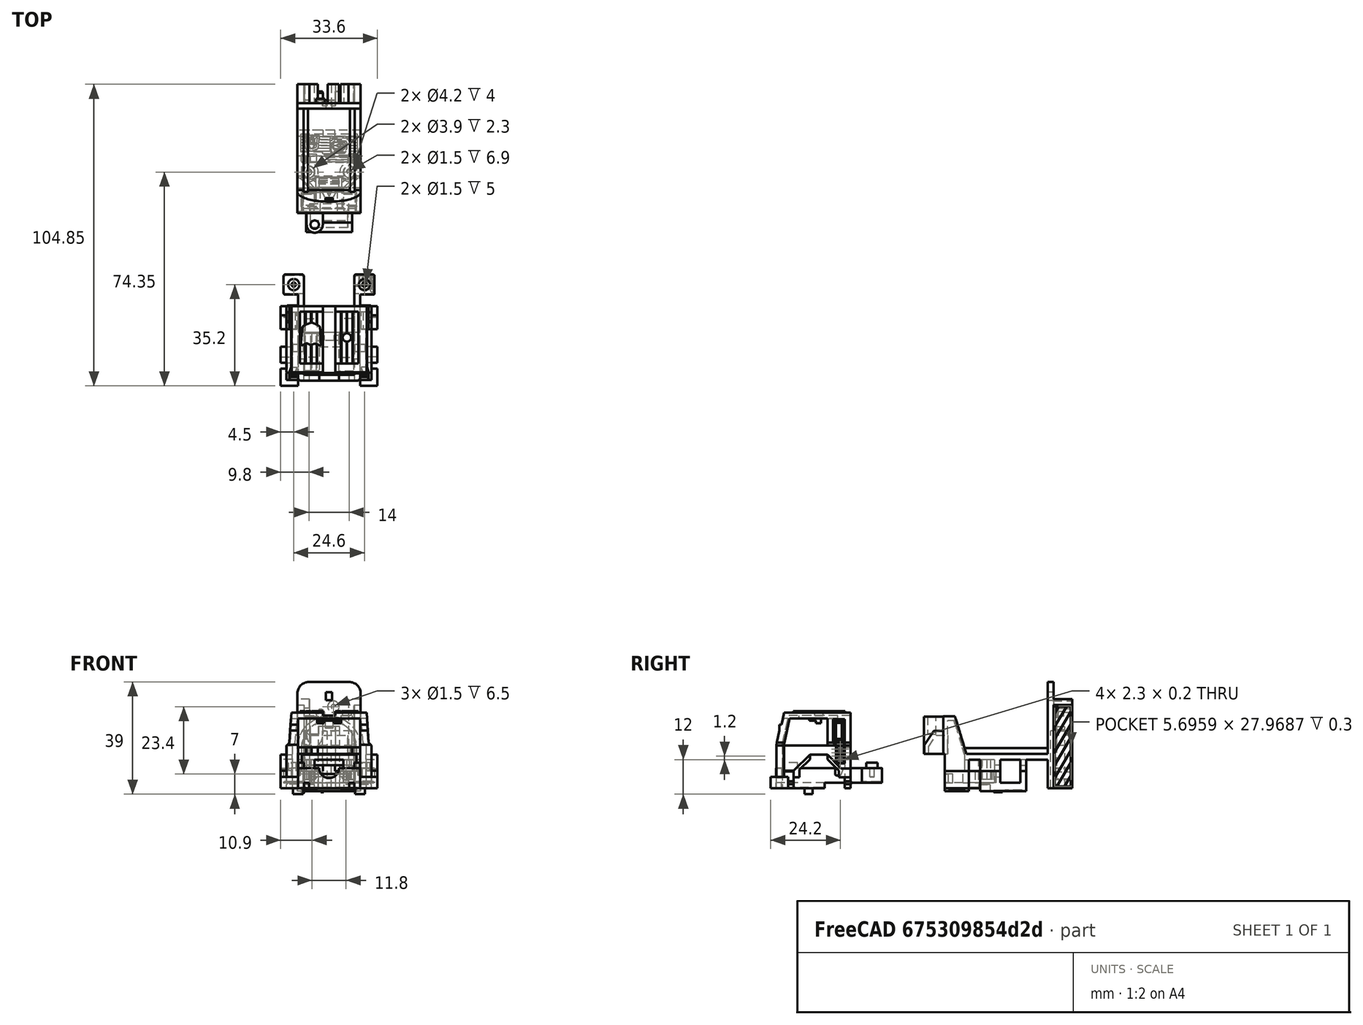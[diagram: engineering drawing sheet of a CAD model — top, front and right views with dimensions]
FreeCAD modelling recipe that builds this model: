
FCSTD DOCUMENT  (FreeCAD 1.0R39319 (Git))
Label: Stickered_Parts
License: All rights reserved
LicenseURL: https://en.wikipedia.org/wiki/All_rights_reserved
objects: Sketcher::SketchObject×30, PartDesign::Pocket×22, PartDesign::Body×12, Image::ImagePlane×8, PartDesign::SubShapeBinder×8, PartDesign::Pad×8, Part::Feature×4, PartDesign::FeatureBase×4, Mesh::Feature×1, App::Part×1
note: 182 computed .brp shape members not serialized (recipe doc carries the construction recipe); baked Part::Feature solids carry a one-line shape summary decoded from their .brp

FEATURE [Part::Feature] Part__Feature  label="Cab"
  shape: bbox 33.6 x 27.95 x 26.8 mm, 325 faces (baked)
FEATURE [Image::ImagePlane] Sticker1
  Placement = pos=(3.1,-61,11) rot=(0,0,1;3.14159rad)
  XSize = 17.2965
  YSize = 14.868
FEATURE [PartDesign::FeatureBase] BaseFeature
  BaseFeature = -> Part__Feature
  Suppressed = false
FEATURE [Sketcher::SketchObject] Sketch
  ArcFitTolerance = 1e-06
  AttachmentOffset = pos=(9.6,-133,0) rot=(0,0,1;3.14159rad)
  AttachmentSupport = -> [BaseFeature]
  FullyConstrained = false
  MakeInternals = false
  MapMode = 5
  Placement = pos=(9.6,-133,15.8) rot=(0,0,1;3.14159rad)
  sketch-geometry (55):
    g0-g23: Circle [constr] x24 (B-spline internal-alignment scaffolding for g24; pole/knot coordinates omitted)
    g24: BSplineCurve PolesCount=28 KnotsCount=26 Degree=3 IsPeriodic=0
    g25-g48: GeomPoint [constr] x24 (B-spline internal-alignment scaffolding for g24; pole/knot coordinates omitted)
    g49: Circle [constr] CenterX=7.95561 CenterY=-71.4183 CenterZ=0 NormalX=0 NormalY=0 NormalZ=1 AngleXU=0 Radius=1
    g50: GeomPoint [constr] X=8.29878 Y=-66.6782 Z=0
    g51: Circle [constr] CenterX=8.16417 CenterY=-68.0435 CenterZ=0 NormalX=0 NormalY=0 NormalZ=1 AngleXU=0 Radius=1
    g52: Circle [constr] CenterX=8.36822 CenterY=-65.9535 CenterZ=0 NormalX=0 NormalY=0 NormalZ=1 AngleXU=0 Radius=1
    g53: Circle [constr] CenterX=8.41747 CenterY=-65.4884 CenterZ=0 NormalX=0 NormalY=0 NormalZ=1 AngleXU=0 Radius=1
    g54: GeomPoint [constr] X=8.36699 Y=-65.9691 Z=0
  constraints (15):
    c: Weight(g0) = 1
    c: Equal(g0, g1-g23) x23
    c: InternalAlignment(g0-g23 -> g24) x24
    c: InternalAlignment(g25-g48 -> g24) x24
    c: Coincident(g23,g0)
    c: InternalAlignment(g49,g24)
    c: Equal(g49,g0)
    c: InternalAlignment(g50,g24)
    c: InternalAlignment(g51,g24)
    c: Equal(g51,g0)
    c: InternalAlignment(g52,g24)
    c: Equal(g52,g0)
    c: InternalAlignment(g53,g24)
    c: Equal(g53,g0)
    c: InternalAlignment(g54,g24)
FEATURE [PartDesign::Pocket] Pocket
  BaseFeature = -> BaseFeature
  Direction = (5.8e-15,0,-1)
  Length = 0.3
  Length2 = 5
  Profile = -> Sketch
  ReferenceAxis = -> Sketch [N_Axis]
  Refine = true
  Suppressed = false
  Type = 0
FEATURE [PartDesign::Body] Body  label="Cab_Stickered1"
  AllowCompound = false
  BaseFeature = -> Part__Feature
  Group = -> [BaseFeature,Sketch,Pocket]
  Origin = -> Origin
  Tip = -> Pocket
FEATURE [Part::Feature] Part__Feature001  label="Rear_Torso"
  shape: bbox 22 x 51.6 x 37 mm, 145 faces (baked)
FEATURE [Image::ImagePlane] Sticker002
  Placement = pos=(19,17.35,3.5) rot=(0,1,0;1.5708rad)
  XSize = 29.34
  YSize = 11.4
FEATURE [PartDesign::FeatureBase] BaseFeature001
  BaseFeature = -> Part__Feature001
  Suppressed = false
FEATURE [Sketcher::SketchObject] Sketch001
  ArcFitTolerance = 1e-06
  AttachmentSupport = -> [BaseFeature001]
  FullyConstrained = false
  MakeInternals = false
  MapMode = 5
  Placement = pos=(19.8,-2.42e-14,8.7e-15) rot=(0.57735,0.57735,0.57735;2.0944rad)
  sketch-geometry (4):
    g0: LineSegment StartX=16.8703 StartY=17.597 StartZ=0 EndX=16.8703 EndY=-10.3717 EndZ=0
    g1: LineSegment StartX=16.8703 StartY=-10.3717 StartZ=0 EndX=22.5662 EndY=-10.3717 EndZ=0
    g2: LineSegment StartX=22.5662 StartY=-10.3717 StartZ=0 EndX=22.5662 EndY=17.597 EndZ=0
    g3: LineSegment StartX=22.5662 StartY=17.597 StartZ=0 EndX=16.8703 EndY=17.597 EndZ=0
  constraints (8):
    c: Coincident(g0,g1)
    c: Coincident(g1,g2)
    c: Coincident(g2,g3)
    c: Coincident(g3,g0)
    c: Vertical(g0)
    c: Vertical(g2)
    c: Horizontal(g1)
    c: Horizontal(g3)
FEATURE [PartDesign::Pocket] Pocket001
  BaseFeature = -> BaseFeature001
  Direction = (-1,1e-15,1e-16)
  Length = 0.3
  Length2 = 5
  Profile = -> Sketch001
  ReferenceAxis = -> Sketch001 [N_Axis]
  Refine = true
  Suppressed = false
  Type = 0
FEATURE [Sketcher::SketchObject] Sketch002
  ArcFitTolerance = 1e-06
  AttachmentSupport = -> [Pocket001]
  FullyConstrained = false
  MakeInternals = false
  MapMode = 5
  Placement = pos=(2.2,-2.1e-15,1.8e-15) rot=(0.57735,-0.57735,-0.57735;2.0944rad)
  sketch-geometry (4):
    g0: LineSegment StartX=-22.5917 StartY=8.98465 StartZ=0 EndX=-22.5917 EndY=-10.3482 EndZ=0
    g1: LineSegment StartX=-22.5917 StartY=-10.3482 StartZ=0 EndX=-16.9211 EndY=-10.3482 EndZ=0
    g2: LineSegment StartX=-16.9211 StartY=-10.3482 StartZ=0 EndX=-16.9211 EndY=8.98465 EndZ=0
    g3: LineSegment StartX=-16.9211 StartY=8.98465 StartZ=0 EndX=-22.5917 EndY=8.98465 EndZ=0
  constraints (8):
    c: Coincident(g0,g1)
    c: Coincident(g1,g2)
    c: Coincident(g2,g3)
    c: Coincident(g3,g0)
    c: Vertical(g0)
    c: Vertical(g2)
    c: Horizontal(g1)
    c: Horizontal(g3)
FEATURE [PartDesign::Pocket] Pocket002
  BaseFeature = -> Pocket001
  Direction = (1,0,0)
  Length = 0.3
  Length2 = 5
  Profile = -> Sketch002
  ReferenceAxis = -> Sketch002 [N_Axis]
  Refine = true
  Suppressed = false
  Type = 0
FEATURE [PartDesign::Body] Body001  label="Rear_Torso_Stickered"
  AllowCompound = false
  BaseFeature = -> Part__Feature001
  Group = -> [BaseFeature001,Sketch001,Pocket001,Sketch002,Pocket002]
  Origin = -> Origin001
  Tip = -> Pocket002
FEATURE [Mesh::Feature] Cab_Sticker  label="Mixmaster_Sticker1"
FEATURE [App::Part] Part  label="Cab_Stickered"
  Group = -> [Sticker1,Part__Feature,Body]
  Origin = -> Origin002
FEATURE [PartDesign::SubShapeBinder] Binder
  BindCopyOnChange = 0
  BindMode = 0
  ClaimChildren = false
  Context = -> Body002 [Binder.]
  Fuse = false
  MakeFace = true
  OffsetFill = false
  OffsetIntersection = false
  OffsetJoinType = 0
  OffsetOpenResult = false
  PartialLoad = false
  Refine = true
  Relative = true
  Support = -> [Body001[Pocket002.Face153]]
  _Version = 2
FEATURE [Sketcher::SketchObject] Sketch003
  ArcFitTolerance = 1e-06
  AttachmentSupport = -> [Binder]
  ExternalGeometry = -> [Binder]
  FullyConstrained = true
  MakeInternals = false
  MapMode = 5
  Placement = pos=(19.5,-1.21e-14,0) rot=(0.57735,0.57735,0.57735;2.0944rad)
  sketch-geometry (4):
    g0: LineSegment StartX=16.9203 StartY=17.547 StartZ=0 EndX=16.9203 EndY=-10.3217 EndZ=0
    g1: LineSegment StartX=16.9203 StartY=-10.3217 StartZ=0 EndX=22.5162 EndY=-10.3217 EndZ=0
    g2: LineSegment StartX=22.5162 StartY=-10.3217 StartZ=0 EndX=22.5162 EndY=17.547 EndZ=0
    g3: LineSegment StartX=22.5162 StartY=17.547 StartZ=0 EndX=16.9203 EndY=17.547 EndZ=0
  constraints (12):
    c: Coincident(g0,g1)
    c: Coincident(g1,g2)
    c: Coincident(g2,g3)
    c: Coincident(g3,g0)
    c: Vertical(g0)
    c: Vertical(g2)
    c: Horizontal(g1)
    c: Horizontal(g3)
    c: DistanceX(g1,g-6) = 0.05
    c: DistanceX(g-6,g0) = 0.05
    c: DistanceY(g-6,g0) = 0.05
    c: DistanceY(g0,g-5) = 0.05
FEATURE [PartDesign::Pad] Pad
  Direction = (1,0,0)
  Length = 0.3
  Length2 = 10
  Profile = -> Sketch003
  ReferenceAxis = -> Sketch003 [N_Axis]
  Refine = true
  Suppressed = false
  Type = 0
FEATURE [Sketcher::SketchObject] Sketch004
  ArcFitTolerance = 1e-06
  AttachmentSupport = -> [Pad]
  ExternalGeometry = -> [Pad]
  FullyConstrained = false
  MakeInternals = false
  MapMode = 5
  Placement = pos=(19.8,0,0) rot=(0.57735,0.57735,0.57735;2.0944rad)
  sketch-geometry (48):
    g0: ArcOfCircle CenterX=18.3173 CenterY=17.547 CenterZ=0 NormalX=0 NormalY=0 NormalZ=-1 AngleXU=-1.04214 Radius=0.0145147 StartAngle=1.5708 EndAngle=4.71239
    g1: LineSegment StartX=18.3299 StartY=17.5397 StartZ=0 EndX=17.8642 EndY=16.7425 EndZ=0
    g2: LineSegment StartX=17.8642 StartY=16.7425 StartZ=0 EndX=16.9329 EndY=15.148 EndZ=0
    g3: ArcOfCircle CenterX=16.9203 CenterY=15.1554 CenterZ=0 NormalX=0 NormalY=0 NormalZ=-1 AngleXU=2.09946 Radius=0.0145147 StartAngle=1.5708 EndAngle=4.71239
    g4: LineSegment StartX=17.8391 StartY=16.7571 StartZ=0 EndX=16.9078 EndY=15.1627 EndZ=0
    g5: LineSegment StartX=18.3048 StartY=17.5543 StartZ=0 EndX=17.8391 EndY=16.7571 EndZ=0
    g6: ArcOfCircle CenterX=16.9203 CenterY=10.4908 CenterZ=0 NormalX=0 NormalY=0 NormalZ=-1 AngleXU=2.09946 Radius=0.0109509 StartAngle=1.5708 EndAngle=4.71239
    g7: LineSegment StartX=16.9109 StartY=10.4963 StartZ=0 EndX=18.2848 EndY=12.8484 EndZ=0
    g8: LineSegment StartX=18.2848 StartY=12.8484 StartZ=0 EndX=21.0325 EndY=17.5525 EndZ=0
    g9: ArcOfCircle CenterX=21.042 CenterY=17.547 CenterZ=0 NormalX=0 NormalY=0 NormalZ=-1 AngleXU=-1.04214 Radius=0.0109509 StartAngle=1.5708 EndAngle=4.71239
    g10: LineSegment StartX=18.3037 StartY=12.8374 StartZ=0 EndX=21.0515 EndY=17.5415 EndZ=0
    g11: LineSegment StartX=16.9298 StartY=10.4853 StartZ=0 EndX=18.3037 EndY=12.8374 EndZ=0
    g12: ArcOfCircle CenterX=22.5162 CenterY=15.7222 CenterZ=0 NormalX=0 NormalY=0 NormalZ=-1 AngleXU=-1.04214 Radius=0.0134354 StartAngle=1.5708 EndAngle=4.71239
    g13: LineSegment StartX=22.5278 StartY=15.7154 StartZ=0 EndX=20.6625 EndY=12.5221 EndZ=0
    g14: LineSegment StartX=20.6625 StartY=12.5221 StartZ=0 EndX=16.9319 EndY=6.13545 EndZ=0
    g15: ArcOfCircle CenterX=16.9203 CenterY=6.14222 CenterZ=0 NormalX=0 NormalY=0 NormalZ=-1 AngleXU=2.09946 Radius=0.0134354 StartAngle=1.5708 EndAngle=4.71239
    g16: LineSegment StartX=20.6393 StartY=12.5357 StartZ=0 EndX=16.9087 EndY=6.149 EndZ=0
    g17: LineSegment StartX=22.5046 StartY=15.729 StartZ=0 EndX=20.6393 EndY=12.5357 EndZ=0
    g18: ArcOfCircle CenterX=16.9203 CenterY=1.66014 CenterZ=0 NormalX=0 NormalY=0 NormalZ=-1 AngleXU=2.09946 Radius=0.0160115 StartAngle=1.5708 EndAngle=4.71239
    g19: LineSegment StartX=16.9065 StartY=1.66822 StartZ=0 EndX=18.7718 EndY=4.86155 EndZ=0
    g20: LineSegment StartX=18.7718 StartY=4.86155 StartZ=0 EndX=22.5024 EndY=11.2482 EndZ=0
    g21: ArcOfCircle CenterX=22.5162 CenterY=11.2401 CenterZ=0 NormalX=0 NormalY=0 NormalZ=-1 AngleXU=-1.04214 Radius=0.0160115 StartAngle=1.5708 EndAngle=4.71239
    g22: LineSegment StartX=18.7994 StartY=4.8454 StartZ=0 EndX=22.53 EndY=11.2321 EndZ=0
    g23: LineSegment StartX=16.9342 StartY=1.65207 StartZ=0 EndX=18.7994 EndY=4.8454 EndZ=0
    g24: ArcOfCircle CenterX=22.5162 CenterY=6.66465 CenterZ=0 NormalX=0 NormalY=0 NormalZ=-1 AngleXU=-1.04214 Radius=0.0135921 StartAngle=1.5708 EndAngle=4.71239
    g25: LineSegment StartX=22.5279 StartY=6.6578 StartZ=0 EndX=20.6626 EndY=3.46446 EndZ=0
    g26: LineSegment StartX=20.6626 StartY=3.46446 StartZ=0 EndX=16.9321 EndY=-2.9222 EndZ=0
    g27: ArcOfCircle CenterX=16.9203 CenterY=-2.91535 CenterZ=0 NormalX=0 NormalY=0 NormalZ=-1 AngleXU=2.09946 Radius=0.0135921 StartAngle=1.5708 EndAngle=4.71239
    g28: LineSegment StartX=20.6392 StartY=3.47818 StartZ=0 EndX=16.9086 EndY=-2.90849 EndZ=0
    g29: LineSegment StartX=22.5045 StartY=6.67151 StartZ=0 EndX=20.6392 EndY=3.47818 EndZ=0
    g30: ArcOfCircle CenterX=16.9203 CenterY=-7.40363 CenterZ=0 NormalX=0 NormalY=0 NormalZ=-1 AngleXU=2.09946 Radius=0.0209294 StartAngle=1.5708 EndAngle=4.71239
    g31: LineSegment StartX=16.9023 StartY=-7.39308 StartZ=0 EndX=18.7675 EndY=-4.19974 EndZ=0
    g32: LineSegment StartX=18.7675 StartY=-4.19974 StartZ=0 EndX=22.4981 EndY=2.18692 EndZ=0
    g33: ArcOfCircle CenterX=22.5162 CenterY=2.17637 CenterZ=0 NormalX=0 NormalY=0 NormalZ=-1 AngleXU=-1.04214 Radius=0.0209294 StartAngle=1.5708 EndAngle=4.71239
    g34: LineSegment StartX=18.8037 StartY=-4.22086 StartZ=0 EndX=22.5343 EndY=2.16581 EndZ=0
    g35: LineSegment StartX=16.9384 StartY=-7.41419 StartZ=0 EndX=18.8037 EndY=-4.22086 EndZ=0
    g36: ArcOfCircle CenterX=17.658 CenterY=-10.3217 CenterZ=0 NormalX=0 NormalY=0 NormalZ=-1 AngleXU=2.09946 Radius=0.0171942 StartAngle=1.5708 EndAngle=4.71239
    g37: LineSegment StartX=17.6431 StartY=-10.313 StartZ=0 EndX=19.2625 EndY=-7.54064 EndZ=0
    g38: LineSegment StartX=19.2625 StartY=-7.54064 StartZ=0 EndX=22.5013 EndY=-1.99585 EndZ=0
    g39: ArcOfCircle CenterX=22.5162 CenterY=-2.00452 CenterZ=0 NormalX=0 NormalY=0 NormalZ=-1 AngleXU=-1.04214 Radius=0.0171942 StartAngle=1.5708 EndAngle=4.71239
    g40: LineSegment StartX=19.2922 StartY=-7.55799 StartZ=0 EndX=22.531 EndY=-2.0132 EndZ=0
    g41: LineSegment StartX=17.6728 StartY=-10.3304 StartZ=0 EndX=19.2922 EndY=-7.55799 EndZ=0
    g42: ArcOfCircle CenterX=22.5162 CenterY=-6.55989 CenterZ=0 NormalX=0 NormalY=0 NormalZ=-1 AngleXU=-1.04214 Radius=0.013888 StartAngle=1.5708 EndAngle=4.71239
    g43: LineSegment StartX=22.5282 StartY=-6.56689 StartZ=0 EndX=21.7957 EndY=-7.82084 EndZ=0
    g44: LineSegment StartX=21.7957 StartY=-7.82084 StartZ=0 EndX=20.3308 EndY=-10.3287 EndZ=0
    g45: ArcOfCircle CenterX=20.3188 CenterY=-10.3217 CenterZ=0 NormalX=0 NormalY=0 NormalZ=-1 AngleXU=2.09946 Radius=0.013888 StartAngle=1.5708 EndAngle=4.71239
    g46: LineSegment StartX=21.7717 StartY=-7.80683 StartZ=0 EndX=20.3068 EndY=-10.3147 EndZ=0
    g47: LineSegment StartX=22.5042 StartY=-6.55289 StartZ=0 EndX=21.7717 EndY=-7.80683 EndZ=0
  constraints (48):
    c: Tangent(g0,g1) = 1.5708
    c: Tangent(g0,g5) = -1.5708
    c: Coincident(g1,g2)
    c: Tangent(g2,g3) = 1.5708
    c: Tangent(g3,g4) = -1.5708
    c: Coincident(g4,g5)
    c: Tangent(g6,g7) = 1.5708
    c: Tangent(g6,g11) = -1.5708
    c: Coincident(g7,g8)
    c: Tangent(g8,g9) = 1.5708
    c: Tangent(g9,g10) = -1.5708
    c: Coincident(g10,g11)
    c: Tangent(g12,g13) = 1.5708
    c: Tangent(g12,g17) = -1.5708
    c: Coincident(g13,g14)
    c: Tangent(g14,g15) = 1.5708
    c: Tangent(g15,g16) = -1.5708
    c: Coincident(g16,g17)
    c: Tangent(g18,g19) = 1.5708
    c: Tangent(g18,g23) = -1.5708
    c: Coincident(g19,g20)
    c: Tangent(g20,g21) = 1.5708
    c: Tangent(g21,g22) = -1.5708
    c: Coincident(g22,g23)
    c: Tangent(g24,g25) = 1.5708
    c: Tangent(g24,g29) = -1.5708
    c: Coincident(g25,g26)
    c: Tangent(g26,g27) = 1.5708
    c: Tangent(g27,g28) = -1.5708
    c: Coincident(g28,g29)
    c: Tangent(g30,g31) = 1.5708
    c: Tangent(g30,g35) = -1.5708
    c: Coincident(g31,g32)
    c: Tangent(g32,g33) = 1.5708
    c: Tangent(g33,g34) = -1.5708
    c: Coincident(g34,g35)
    c: Tangent(g36,g37) = 1.5708
    c: Tangent(g36,g41) = -1.5708
    c: Coincident(g37,g38)
    c: Tangent(g38,g39) = 1.5708
    c: Tangent(g39,g40) = -1.5708
    c: Coincident(g40,g41)
    c: Tangent(g42,g43) = 1.5708
    c: Tangent(g42,g47) = -1.5708
    c: Coincident(g43,g44)
    c: Tangent(g44,g45) = 1.5708
    c: Tangent(g45,g46) = -1.5708
    c: Coincident(g46,g47)
FEATURE [PartDesign::Pocket] Pocket003
  BaseFeature = -> Pad
  Direction = (-1,0,0)
  Length = 0.15
  Length2 = 5
  Profile = -> Sketch004
  ReferenceAxis = -> Sketch004 [N_Axis]
  Refine = true
  Suppressed = false
  Type = 0
FEATURE [PartDesign::Body] Body002  label="Mikmaster_Sticker2"
  AllowCompound = false
  Group = -> [Binder,Sketch003,Pad,Sketch004,Pocket003]
  Origin = -> Origin003
  Tip = -> Pocket003
FEATURE [PartDesign::SubShapeBinder] Binder001
  BindCopyOnChange = 0
  BindMode = 0
  ClaimChildren = false
  Context = -> Body003 [Binder001.]
  Fuse = false
  MakeFace = true
  OffsetFill = false
  OffsetIntersection = false
  OffsetJoinType = 0
  OffsetOpenResult = false
  PartialLoad = false
  Refine = true
  Relative = true
  Support = -> [Body001[Pocket002.Face151]]
  _Version = 2
FEATURE [Sketcher::SketchObject] Sketch005
  ArcFitTolerance = 1e-06
  AttachmentSupport = -> [Binder001]
  ExternalGeometry = -> [Binder001]
  FullyConstrained = true
  MakeInternals = false
  MapMode = 5
  Placement = pos=(2.5,0,0) rot=(0.57735,-0.57735,-0.57735;2.0944rad)
  sketch-geometry (4):
    g0: LineSegment StartX=-16.9711 StartY=-10.2982 StartZ=0 EndX=-16.9711 EndY=8.93465 EndZ=0
    g1: LineSegment StartX=-16.9711 StartY=8.93465 StartZ=0 EndX=-22.5417 EndY=8.93465 EndZ=0
    g2: LineSegment StartX=-22.5417 StartY=8.93465 StartZ=0 EndX=-22.5417 EndY=-10.2982 EndZ=0
    g3: LineSegment StartX=-22.5417 StartY=-10.2982 StartZ=0 EndX=-16.9711 EndY=-10.2982 EndZ=0
  constraints (12):
    c: Coincident(g0,g1)
    c: Coincident(g1,g2)
    c: Coincident(g2,g3)
    c: Coincident(g3,g0)
    c: Vertical(g0)
    c: Vertical(g2)
    c: Horizontal(g1)
    c: Horizontal(g3)
    c: DistanceY(g1,g-4) = 0.05
    c: DistanceY(g-6,g2) = 0.05
    c: DistanceX(g-6,g2) = 0.05
    c: DistanceX(g0,g-6) = 0.05
FEATURE [PartDesign::Pad] Pad001
  Direction = (-1,0,0)
  Length = 0.3
  Length2 = 10
  Profile = -> Sketch005
  ReferenceAxis = -> Sketch005 [N_Axis]
  Refine = true
  Suppressed = false
  Type = 0
FEATURE [Sketcher::SketchObject] Sketch006
  ArcFitTolerance = 1e-06
  AttachmentSupport = -> [Pad001]
  ExternalGeometry = -> [Pad001]
  FullyConstrained = false
  MakeInternals = false
  MapMode = 5
  Placement = pos=(2.2,0,0) rot=(0.57735,-0.57735,-0.57735;2.0944rad)
  sketch-geometry (36):
    g0: ArcOfCircle CenterX=-16.9711 CenterY=6.33799 CenterZ=0 NormalX=0 NormalY=0 NormalZ=-1 AngleXU=1.03621 Radius=0.0132627 StartAngle=1.5708 EndAngle=4.71239
    g1: LineSegment StartX=-16.9825 StartY=6.33124 StartZ=0 EndX=-17.495 EndY=7.19679 EndZ=0
    g2: LineSegment StartX=-17.495 StartY=7.19679 StartZ=0 EndX=-18.52 EndY=8.92789 EndZ=0
    g3: ArcOfCircle CenterX=-18.5086 CenterY=8.93464 CenterZ=0 NormalX=0 NormalY=0 NormalZ=-1 AngleXU=-2.10538 Radius=0.0132627 StartAngle=1.5708 EndAngle=4.71239
    g4: LineSegment StartX=-17.4722 StartY=7.2103 StartZ=0 EndX=-18.4972 EndY=8.9414 EndZ=0
    g5: LineSegment StartX=-16.9597 StartY=6.34475 StartZ=0 EndX=-17.4722 EndY=7.2103 EndZ=0
    g6: ArcOfCircle CenterX=-16.9711 CenterY=1.64099 CenterZ=0 NormalX=0 NormalY=0 NormalZ=-1 AngleXU=1.04711 Radius=0.0110148 StartAngle=1.5708 EndAngle=4.71239
    g7: LineSegment StartX=-16.9807 StartY=1.63549 StartZ=0 EndX=-18.3846 EndY=4.0667 EndZ=0
    g8: LineSegment StartX=-18.3846 StartY=4.0667 StartZ=0 EndX=-21.1925 EndY=8.92914 EndZ=0
    g9: ArcOfCircle CenterX=-21.183 CenterY=8.93464 CenterZ=0 NormalX=0 NormalY=0 NormalZ=-1 AngleXU=-2.09448 Radius=0.0110148 StartAngle=1.5708 EndAngle=4.71239
    g10: LineSegment StartX=-18.3655 StartY=4.07772 StartZ=0 EndX=-21.1734 EndY=8.94015 EndZ=0
    g11: LineSegment StartX=-16.9616 StartY=1.6465 StartZ=0 EndX=-18.3655 EndY=4.07772 EndZ=0
    g12: ArcOfCircle CenterX=-16.9711 CenterY=-2.62735 CenterZ=0 NormalX=0 NormalY=0 NormalZ=-1 AngleXU=1.03412 Radius=0.00589792 StartAngle=1.5708 EndAngle=4.71239
    g13: LineSegment StartX=-16.9762 StartY=-2.63036 StartZ=0 EndX=-18.833 EndY=0.490791 EndZ=0
    g14: LineSegment StartX=-18.833 StartY=0.490791 StartZ=0 EndX=-22.5468 EndY=6.7331 EndZ=0
    g15: ArcOfCircle CenterX=-22.5417 CenterY=6.73611 CenterZ=0 NormalX=0 NormalY=0 NormalZ=-1 AngleXU=-2.10748 Radius=0.00589792 StartAngle=1.5708 EndAngle=4.71239
    g16: LineSegment StartX=-18.8229 StartY=0.496822 StartZ=0 EndX=-22.5366 EndY=6.73913 EndZ=0
    g17: LineSegment StartX=-16.9661 StartY=-2.62433 StartZ=0 EndX=-18.8229 EndY=0.496822 EndZ=0
    g18: ArcOfCircle CenterX=-16.9711 CenterY=-7.3636 CenterZ=0 NormalX=0 NormalY=0 NormalZ=-1 AngleXU=1.0451 Radius=0.00620277 StartAngle=1.5708 EndAngle=4.71239
    g19: LineSegment StartX=-16.9765 StartY=-7.36671 StartZ=0 EndX=-18.8333 EndY=-4.16605 EndZ=0
    g20: LineSegment StartX=-18.8333 StartY=-4.16605 StartZ=0 EndX=-22.547 EndY=2.23528 EndZ=0
    g21: ArcOfCircle CenterX=-22.5417 CenterY=2.23839 CenterZ=0 NormalX=0 NormalY=0 NormalZ=-1 AngleXU=-2.09649 Radius=0.00620277 StartAngle=1.5708 EndAngle=4.71239
    g22: LineSegment StartX=-18.8226 StartY=-4.15982 StartZ=0 EndX=-22.5363 EndY=2.2415 EndZ=0
    g23: LineSegment StartX=-16.9658 StartY=-7.36048 StartZ=0 EndX=-18.8226 EndY=-4.15982 EndZ=0
    g24: ArcOfCircle CenterX=-17.6283 CenterY=-10.2982 CenterZ=0 NormalX=0 NormalY=0 NormalZ=-1 AngleXU=1.03582 Radius=0.0159745 StartAngle=1.5708 EndAngle=4.71239
    g25: LineSegment StartX=-17.6421 StartY=-10.3064 StartZ=0 EndX=-19.2799 EndY=-7.5428 EndZ=0
    g26: LineSegment StartX=-19.2799 StartY=-7.5428 StartZ=0 EndX=-22.5554 EndY=-2.01561 EndZ=0
    g27: ArcOfCircle CenterX=-22.5417 CenterY=-2.00747 CenterZ=0 NormalX=0 NormalY=0 NormalZ=-1 AngleXU=-2.10578 Radius=0.0159745 StartAngle=1.5708 EndAngle=4.71239
    g28: LineSegment StartX=-19.2524 StartY=-7.52651 StartZ=0 EndX=-22.5279 EndY=-1.99932 EndZ=0
    g29: LineSegment StartX=-17.6146 StartY=-10.2901 StartZ=0 EndX=-19.2524 EndY=-7.52651 EndZ=0
    g30: ArcOfCircle CenterX=-20.3185 CenterY=-10.2982 CenterZ=0 NormalX=0 NormalY=0 NormalZ=-1 AngleXU=1.039 Radius=0.0166288 StartAngle=1.5708 EndAngle=4.71239
    g31: LineSegment StartX=-20.3328 StartY=-10.3067 StartZ=0 EndX=-21.0739 EndY=-9.04709 EndZ=0
    g32: LineSegment StartX=-21.0739 StartY=-9.04709 StartZ=0 EndX=-22.556 EndY=-6.52793 EndZ=0
    g33: ArcOfCircle CenterX=-22.5417 CenterY=-6.51949 CenterZ=0 NormalX=0 NormalY=0 NormalZ=-1 AngleXU=-2.1026 Radius=0.0166288 StartAngle=1.5708 EndAngle=4.71239
    g34: LineSegment StartX=-21.0452 StartY=-9.03023 StartZ=0 EndX=-22.5274 EndY=-6.51106 EndZ=0
    g35: LineSegment StartX=-20.3042 StartY=-10.2898 StartZ=0 EndX=-21.0452 EndY=-9.03023 EndZ=0
  constraints (36):
    c: Tangent(g0,g1) = 1.5708
    c: Tangent(g0,g5) = -1.5708
    c: Coincident(g1,g2)
    c: Tangent(g2,g3) = 1.5708
    c: Tangent(g3,g4) = -1.5708
    c: Coincident(g4,g5)
    c: Tangent(g6,g7) = 1.5708
    c: Tangent(g6,g11) = -1.5708
    c: Coincident(g7,g8)
    c: Tangent(g8,g9) = 1.5708
    c: Tangent(g9,g10) = -1.5708
    c: Coincident(g10,g11)
    c: Tangent(g12,g13) = 1.5708
    c: Tangent(g12,g17) = -1.5708
    c: Coincident(g13,g14)
    c: Tangent(g14,g15) = 1.5708
    c: Tangent(g15,g16) = -1.5708
    c: Coincident(g16,g17)
    c: Tangent(g18,g19) = 1.5708
    c: Tangent(g18,g23) = -1.5708
    c: Coincident(g19,g20)
    c: Tangent(g20,g21) = 1.5708
    c: Tangent(g21,g22) = -1.5708
    c: Coincident(g22,g23)
    c: Tangent(g24,g25) = 1.5708
    c: Tangent(g24,g29) = -1.5708
    c: Coincident(g25,g26)
    c: Tangent(g26,g27) = 1.5708
    c: Tangent(g27,g28) = -1.5708
    c: Coincident(g28,g29)
    c: Tangent(g30,g31) = 1.5708
    c: Tangent(g30,g35) = -1.5708
    c: Coincident(g31,g32)
    c: Tangent(g32,g33) = 1.5708
    c: Tangent(g33,g34) = -1.5708
    c: Coincident(g34,g35)
FEATURE [PartDesign::Pocket] Pocket004
  BaseFeature = -> Pad001
  Direction = (1,0,0)
  Length = 0.15
  Length2 = 5
  Profile = -> Sketch006
  ReferenceAxis = -> Sketch006 [N_Axis]
  Refine = true
  Suppressed = false
  Type = 0
FEATURE [PartDesign::Body] Body003  label="Mikmaster_Sticker3"
  AllowCompound = false
  Group = -> [Binder001,Sketch005,Pad001,Sketch006,Pocket004]
  Origin = -> Origin004
  Tip = -> Pocket004
FEATURE [Part::Feature] Part__Feature002  label="Front Feet"
  shape: bbox 31.6 x 36.9 x 11 mm, 86 faces (baked)
FEATURE [Image::ImagePlane] Sticker4
  Placement = pos=(5.1,-70.2,0) rot=(0,0,-1;1.5708rad)
  XSize = 13.8574
  YSize = 5.58085
FEATURE [Image::ImagePlane] Sticker5
  Placement = pos=(23.3,-46.7,0) rot=(0,0,1;0rad)
  XSize = 7.32421
  YSize = 7.51695
FEATURE [PartDesign::FeatureBase] BaseFeature002
  BaseFeature = -> Part__Feature002
  Suppressed = false
FEATURE [Sketcher::SketchObject] Sketch007
  ArcFitTolerance = 1e-06
  AttachmentSupport = -> [BaseFeature002]
  ExternalGeometry = -> [BaseFeature002]
  FullyConstrained = true
  MakeInternals = false
  MapMode = 5
  Placement = pos=(1.023e-13,0,-11) rot=(1,0,0;3.14159rad)
  sketch-geometry (36):
    g0: LineSegment StartX=14.4 StartY=76.75 StartZ=0 EndX=14.4 EndY=64.05 EndZ=0
    g1: LineSegment StartX=14.9 StartY=63.55 StartZ=0 EndX=19 EndY=63.55 EndZ=0
    g2: LineSegment StartX=19.5 StartY=64.05 StartZ=0 EndX=19.5 EndY=76.75 EndZ=0
    g3: LineSegment StartX=19.5 StartY=76.75 StartZ=0 EndX=14.4 EndY=76.75 EndZ=0
    g4: LineSegment StartX=2.5 StartY=76.75 StartZ=0 EndX=2.5 EndY=64.05 EndZ=0
    g5: LineSegment StartX=3 StartY=63.55 StartZ=0 EndX=7.1 EndY=63.55 EndZ=0
    g6: LineSegment StartX=7.6 StartY=64.05 StartZ=0 EndX=7.6 EndY=76.75 EndZ=0
    g7: LineSegment StartX=7.6 StartY=76.75 StartZ=0 EndX=2.5 EndY=76.75 EndZ=0
    g8: ArcOfCircle CenterX=14.9 CenterY=64.05 CenterZ=0 NormalX=0 NormalY=0 NormalZ=1 AngleXU=0 Radius=0.5 StartAngle=3.14159 EndAngle=4.71239
    g9: GeomPoint [constr] X=14.4 Y=63.55 Z=0
    g10: ArcOfCircle CenterX=19 CenterY=64.05 CenterZ=0 NormalX=0 NormalY=0 NormalZ=1 AngleXU=0 Radius=0.5 StartAngle=4.71239 EndAngle=6.28319
    g11: GeomPoint [constr] X=19.5 Y=63.55 Z=0
    g12: ArcOfCircle CenterX=3 CenterY=64.05 CenterZ=0 NormalX=0 NormalY=0 NormalZ=1 AngleXU=0 Radius=0.5 StartAngle=3.14159 EndAngle=4.71239
    g13: GeomPoint [constr] X=2.5 Y=63.55 Z=0
    g14: ArcOfCircle CenterX=7.1 CenterY=64.05 CenterZ=0 NormalX=0 NormalY=0 NormalZ=1 AngleXU=0 Radius=0.5 StartAngle=4.71239 EndAngle=6.28319
    g15: GeomPoint [constr] X=7.6 Y=63.55 Z=0
    g16: LineSegment StartX=20.05 StartY=49.9 StartZ=0 EndX=20.05 EndY=43.9 EndZ=0
    g17: LineSegment StartX=20.55 StartY=43.4 StartZ=0 EndX=26.05 EndY=43.4 EndZ=0
    g18: LineSegment StartX=26.55 StartY=43.9 StartZ=0 EndX=26.55 EndY=49.4 EndZ=0
    g19: LineSegment StartX=26.05 StartY=49.9 StartZ=0 EndX=20.05 EndY=49.9 EndZ=0
    g20: ArcOfCircle CenterX=26.05 CenterY=49.4 CenterZ=0 NormalX=0 NormalY=0 NormalZ=1 AngleXU=0 Radius=0.5 StartAngle=-2.7e-15 EndAngle=1.5708
    g21: GeomPoint [constr] X=26.55 Y=49.9 Z=0
    g22: ArcOfCircle CenterX=26.05 CenterY=43.9 CenterZ=0 NormalX=0 NormalY=0 NormalZ=1 AngleXU=0 Radius=0.5 StartAngle=4.71239 EndAngle=6.28319
    g23: GeomPoint [constr] X=26.55 Y=43.4 Z=0
    g24: ArcOfCircle CenterX=20.55 CenterY=43.9 CenterZ=0 NormalX=0 NormalY=0 NormalZ=1 AngleXU=0 Radius=0.5 StartAngle=3.14159 EndAngle=4.71239
    g25: GeomPoint [constr] X=20.05 Y=43.4 Z=0
    g26: LineSegment StartX=-4.55 StartY=49.4 StartZ=0 EndX=-4.55 EndY=43.9 EndZ=0
    g27: LineSegment StartX=-4.05 StartY=43.4 StartZ=0 EndX=1.45 EndY=43.4 EndZ=0
    g28: LineSegment StartX=1.95 StartY=43.9 StartZ=0 EndX=1.95 EndY=49.9 EndZ=0
    g29: LineSegment StartX=1.95 StartY=49.9 StartZ=0 EndX=-4.05 EndY=49.9 EndZ=0
    g30: ArcOfCircle CenterX=1.45 CenterY=43.9 CenterZ=0 NormalX=0 NormalY=0 NormalZ=1 AngleXU=0 Radius=0.5 StartAngle=4.71239 EndAngle=6.28319
    g31: GeomPoint [constr] X=1.95 Y=43.4 Z=0
    g32: ArcOfCircle CenterX=-4.05 CenterY=43.9 CenterZ=0 NormalX=0 NormalY=0 NormalZ=1 AngleXU=0 Radius=0.5 StartAngle=3.14159 EndAngle=4.71239
    g33: GeomPoint [constr] X=-4.55 Y=43.4 Z=0
    g34: ArcOfCircle CenterX=-4.05 CenterY=49.4 CenterZ=0 NormalX=0 NormalY=0 NormalZ=1 AngleXU=0 Radius=0.5 StartAngle=1.5708 EndAngle=3.14159
    g35: GeomPoint [constr] X=-4.55 Y=49.9 Z=0
  constraints (88):
    c: Coincident(g2,g3)
    c: Coincident(g3,g0)
    c: Vertical(g0)
    c: Vertical(g2)
    c: Horizontal(g1)
    c: Horizontal(g3)
    c: DistanceX(g11,g-4) = 0.3
    c: DistanceY(g-4,g11) = 0.4
    c: DistanceX(g9,g11) = 5.1
    c: DistanceY(g9,g0) = 13.2
    c: Coincident(g6,g7)
    c: Coincident(g7,g4)
    c: Vertical(g4)
    c: Vertical(g6)
    c: Horizontal(g5)
    c: Horizontal(g7)
    c: DistanceY(g15,g6) = 13.2
    c: DistanceY(g-5,g13) = 0.4
    c: DistanceX(g13,g15) = 5.1
    c: PointOnObject(g9,g0)
    c: PointOnObject(g9,g1)
    c: Tangent(g0,g8) = -1.5708
    c: Tangent(g1,g8) = -1.5708
    c: PointOnObject(g11,g1)
    c: PointOnObject(g11,g2)
    c: Tangent(g1,g10) = -1.5708
    c: Tangent(g2,g10) = -1.5708
    c: Radius(g10) = 0.5
    c: Radius(g8) = 0.5
    c: DistanceX(g-5,g13) = 0.3
    c: PointOnObject(g13,g4)
    c: PointOnObject(g13,g5)
    c: Tangent(g4,g12) = -1.5708
    c: Tangent(g5,g12) = -1.5708
    c: PointOnObject(g15,g5)
    c: PointOnObject(g15,g6)
    c: Tangent(g5,g14) = -1.5708
    c: Tangent(g6,g14) = -1.5708
    c: Radius(g14) = 0.5
    c: Radius(g12) = 0.5
    c: Coincident(g19,g16)
    c: Vertical(g16)
    c: Vertical(g18)
    c: Horizontal(g17)
    c: Horizontal(g19)
    c: PointOnObject(g21,g18)
    c: PointOnObject(g21,g19)
    c: Tangent(g18,g20) = -1.5708
    c: Tangent(g19,g20) = -1.5708
    c: PointOnObject(g23,g17)
    c: PointOnObject(g23,g18)
    c: Tangent(g17,g22) = -1.5708
    c: Tangent(g18,g22) = -1.5708
    c: PointOnObject(g25,g16)
    c: PointOnObject(g25,g17)
    c: Tangent(g16,g24) = -1.5708
    c: Tangent(g17,g24) = -1.5708
    c: Radius(g24) = 0.5
    c: Radius(g22) = 0.5
    c: Radius(g20) = 0.5
    c: DistanceX(g-4,g16) = 0.25
    c: DistanceX(g18,g-7) = 0.25
    c: DistanceY(g19,g-8) = 0.25
    c: DistanceY(g-6,g17) = 0.25
    c: Coincident(g28,g29)
    c: Vertical(g26)
    c: Vertical(g28)
    c: Horizontal(g27)
    c: Horizontal(g29)
    c: PointOnObject(g31,g27)
    c: PointOnObject(g31,g28)
    c: Tangent(g27,g30) = -1.5708
    c: Tangent(g28,g30) = -1.5708
    c: PointOnObject(g33,g26)
    c: PointOnObject(g33,g27)
    c: Tangent(g26,g32) = -1.5708
    c: Tangent(g27,g32) = -1.5708
    c: PointOnObject(g35,g26)
    c: PointOnObject(g35,g29)
    c: Tangent(g26,g34) = -1.5708
    c: Tangent(g29,g34) = -1.5708
    c: Radius(g34) = 0.5
    c: Radius(g32) = 0.5
    c: Radius(g30) = 0.5
    c: DistanceY(g29,g-11) = 0.25
    c: DistanceY(g-9,g27) = 0.25
    c: DistanceX(g-10,g26) = 0.25
    c: DistanceX(g28,g-5) = 0.25
FEATURE [PartDesign::Pocket] Pocket005
  BaseFeature = -> BaseFeature002
  Direction = (-9.3e-15,0,1)
  Length = 0.3
  Length2 = 5
  Profile = -> Sketch007
  ReferenceAxis = -> Sketch007 [N_Axis]
  Refine = true
  Suppressed = false
  Type = 0
FEATURE [Sketcher::SketchObject] Sketch008
  ArcFitTolerance = 1e-06
  AttachmentSupport = -> [Pocket005]
  ExternalGeometry = -> [Pocket005]
  FullyConstrained = true
  MakeInternals = false
  MapMode = 5
  Placement = pos=(8.4e-14,0,-9) rot=(1,0,0;3.14159rad)
  sketch-geometry (20):
    g0: LineSegment StartX=20.05 StartY=49.9 StartZ=0 EndX=20.05 EndY=43.9 EndZ=0
    g1: LineSegment StartX=20.55 StartY=43.4 StartZ=0 EndX=26.05 EndY=43.4 EndZ=0
    g2: LineSegment StartX=26.55 StartY=43.9 StartZ=0 EndX=26.55 EndY=49.4 EndZ=0
    g3: LineSegment StartX=26.05 StartY=49.9 StartZ=0 EndX=20.05 EndY=49.9 EndZ=0
    g4: LineSegment StartX=-4.55 StartY=49.4 StartZ=0 EndX=-4.55 EndY=43.9 EndZ=0
    g5: LineSegment StartX=-4.05 StartY=43.4 StartZ=0 EndX=1.45 EndY=43.4 EndZ=0
    g6: LineSegment StartX=1.95 StartY=43.9 StartZ=0 EndX=1.95 EndY=49.9 EndZ=0
    g7: LineSegment StartX=1.95 StartY=49.9 StartZ=0 EndX=-4.05 EndY=49.9 EndZ=0
    g8: ArcOfCircle CenterX=-4.05 CenterY=49.4 CenterZ=0 NormalX=0 NormalY=0 NormalZ=1 AngleXU=0 Radius=0.5 StartAngle=1.5708 EndAngle=3.14159
    g9: GeomPoint [constr] X=-4.55 Y=49.9 Z=0
    g10: ArcOfCircle CenterX=-4.05 CenterY=43.9 CenterZ=0 NormalX=0 NormalY=0 NormalZ=1 AngleXU=0 Radius=0.5 StartAngle=3.14159 EndAngle=4.71239
    g11: GeomPoint [constr] X=-4.55 Y=43.4 Z=0
    g12: ArcOfCircle CenterX=1.45 CenterY=43.9 CenterZ=0 NormalX=0 NormalY=0 NormalZ=1 AngleXU=0 Radius=0.5 StartAngle=4.71239 EndAngle=6.28319
    g13: GeomPoint [constr] X=1.95 Y=43.4 Z=0
    g14: ArcOfCircle CenterX=20.55 CenterY=43.9 CenterZ=0 NormalX=0 NormalY=0 NormalZ=1 AngleXU=0 Radius=0.5 StartAngle=3.14159 EndAngle=4.71239
    g15: GeomPoint [constr] X=20.05 Y=43.4 Z=0
    g16: ArcOfCircle CenterX=26.05 CenterY=43.9 CenterZ=0 NormalX=0 NormalY=0 NormalZ=1 AngleXU=0 Radius=0.5 StartAngle=4.71239 EndAngle=6.28319
    g17: GeomPoint [constr] X=26.55 Y=43.4 Z=0
    g18: ArcOfCircle CenterX=26.05 CenterY=49.4 CenterZ=0 NormalX=0 NormalY=0 NormalZ=1 AngleXU=0 Radius=0.5 StartAngle=6.4e-15 EndAngle=1.5708
    g19: GeomPoint [constr] X=26.55 Y=49.9 Z=0
  constraints (48):
    c: Coincident(g3,g0)
    c: Vertical(g0)
    c: Vertical(g2)
    c: Horizontal(g1)
    c: Horizontal(g3)
    c: Coincident(g6,g7)
    c: Vertical(g4)
    c: Vertical(g6)
    c: Horizontal(g5)
    c: Horizontal(g7)
    c: PointOnObject(g9,g4)
    c: PointOnObject(g9,g7)
    c: Tangent(g4,g8) = -1.5708
    c: Tangent(g7,g8) = -1.5708
    c: PointOnObject(g11,g4)
    c: PointOnObject(g11,g5)
    c: Tangent(g4,g10) = -1.5708
    c: Tangent(g5,g10) = -1.5708
    c: PointOnObject(g13,g5)
    c: PointOnObject(g13,g6)
    c: Tangent(g5,g12) = -1.5708
    c: Tangent(g6,g12) = -1.5708
    c: PointOnObject(g15,g0)
    c: PointOnObject(g15,g1)
    c: Tangent(g0,g14) = -1.5708
    c: Tangent(g1,g14) = -1.5708
    c: PointOnObject(g17,g1)
    c: PointOnObject(g17,g2)
    c: Tangent(g1,g16) = -1.5708
    c: Tangent(g2,g16) = -1.5708
    c: PointOnObject(g19,g2)
    c: PointOnObject(g19,g3)
    c: Tangent(g2,g18) = -1.5708
    c: Tangent(g3,g18) = -1.5708
    c: Radius(g16) = 0.5
    c: Radius(g14) = 0.5
    c: Radius(g18) = 0.5
    c: Radius(g12) = 0.5
    c: Radius(g10) = 0.5
    c: Radius(g8) = 0.5
    c: DistanceY(g-9,g1) = 0.25
    c: DistanceY(g3,g-7) = 0.25
    c: DistanceY(g7,g-5) = 0.25
    c: DistanceY(g-3,g5) = 0.25
    c: DistanceX(g-4,g4) = 0.25
    c: DistanceX(g6,g-10) = 0.25
    c: DistanceX(g-6,g0) = 0.25
    c: DistanceX(g2,g-8) = 0.25
FEATURE [PartDesign::Pocket] Pocket006
  BaseFeature = -> Pocket005
  Direction = (-9.3e-15,0,1)
  Length = 0.3
  Length2 = 5
  Profile = -> Sketch008
  ReferenceAxis = -> Sketch008 [N_Axis]
  Refine = true
  Suppressed = false
  Type = 0
FEATURE [PartDesign::Body] Body004  label="Front_Feet_Stickered"
  AllowCompound = false
  BaseFeature = -> Part__Feature002
  Group = -> [BaseFeature002,Sketch007,Pocket005,Sketch008,Pocket006]
  Origin = -> Origin005
  Tip = -> Pocket006
FEATURE [PartDesign::SubShapeBinder] Binder002
  BindCopyOnChange = 0
  BindMode = 0
  ClaimChildren = false
  Context = -> Body005 [Binder002.]
  Fuse = false
  MakeFace = true
  OffsetFill = false
  OffsetIntersection = false
  OffsetJoinType = 0
  OffsetOpenResult = false
  PartialLoad = false
  Refine = true
  Relative = true
  Support = -> [Body004[Pocket006.Face112]]
  _Version = 2
FEATURE [Sketcher::SketchObject] Sketch009
  ArcFitTolerance = 1e-06
  AttachmentSupport = -> [Binder002]
  ExternalGeometry = -> [Binder002]
  FullyConstrained = true
  MakeInternals = false
  MapMode = 5
  Placement = pos=(8.11e-14,0,-8.7) rot=(1,0,0;3.14159rad)
  sketch-geometry (10):
    g0: LineSegment StartX=20.1 StartY=49.85 StartZ=0 EndX=20.1 EndY=43.95 EndZ=0
    g1: LineSegment StartX=20.6 StartY=43.45 StartZ=0 EndX=26 EndY=43.45 EndZ=0
    g2: LineSegment StartX=26.5 StartY=43.95 StartZ=0 EndX=26.5 EndY=49.35 EndZ=0
    g3: LineSegment StartX=26 StartY=49.85 StartZ=0 EndX=20.1 EndY=49.85 EndZ=0
    g4: ArcOfCircle CenterX=26 CenterY=49.35 CenterZ=0 NormalX=0 NormalY=0 NormalZ=1 AngleXU=0 Radius=0.5 StartAngle=-4.4e-15 EndAngle=1.5708
    g5: GeomPoint [constr] X=26.5 Y=49.85 Z=0
    g6: ArcOfCircle CenterX=26 CenterY=43.95 CenterZ=0 NormalX=0 NormalY=0 NormalZ=1 AngleXU=0 Radius=0.5 StartAngle=4.71239 EndAngle=6.28319
    g7: GeomPoint [constr] X=26.5 Y=43.45 Z=0
    g8: ArcOfCircle CenterX=20.6 CenterY=43.95 CenterZ=0 NormalX=0 NormalY=0 NormalZ=1 AngleXU=0 Radius=0.5 StartAngle=3.14159 EndAngle=4.71239
    g9: GeomPoint [constr] X=20.1 Y=43.45 Z=0
  constraints (24):
    c: Coincident(g3,g0)
    c: Vertical(g0)
    c: Vertical(g2)
    c: Horizontal(g1)
    c: Horizontal(g3)
    c: PointOnObject(g5,g2)
    c: PointOnObject(g5,g3)
    c: Tangent(g2,g4) = -1.5708
    c: Tangent(g3,g4) = -1.5708
    c: PointOnObject(g7,g1)
    c: PointOnObject(g7,g2)
    c: Tangent(g1,g6) = -1.5708
    c: Tangent(g2,g6) = -1.5708
    c: PointOnObject(g9,g0)
    c: PointOnObject(g9,g1)
    c: Tangent(g0,g8) = -1.5708
    c: Tangent(g1,g8) = -1.5708
    c: Radius(g8) = 0.5
    c: Radius(g6) = 0.5
    c: Radius(g4) = 0.5
    c: DistanceY(g-6,g1) = 0.05
    c: DistanceY(g0,g-5) = 0.05
    c: DistanceX(g-5,g0) = 0.05
    c: DistanceX(g2,g-4) = 0.05
FEATURE [PartDesign::Pad] Pad002
  Direction = (9.3e-15,0,-1)
  Length = 0.3
  Length2 = 10
  Profile = -> Sketch009
  ReferenceAxis = -> Sketch009 [N_Axis]
  Refine = true
  Suppressed = false
  Type = 0
FEATURE [Sketcher::SketchObject] Sketch010
  ArcFitTolerance = 1e-06
  AttachmentSupport = -> [Pad002]
  ExternalGeometry = -> [Pad002]
  FullyConstrained = false
  MakeInternals = false
  MapMode = 5
  Placement = pos=(8.43e-14,0,-9) rot=(1,0,0;3.14159rad)
  sketch-geometry (83):
    g0: Circle CenterX=25.873 CenterY=48.7093 CenterZ=0 NormalX=0 NormalY=0 NormalZ=1 AngleXU=0 Radius=0.504766
    g1: Circle CenterX=25.873 CenterY=48.7093 CenterZ=0 NormalX=0 NormalY=0 NormalZ=1 AngleXU=0 Radius=0.514911
    g2: ArcOfCircle CenterX=20.1 CenterY=48.3907 CenterZ=0 NormalX=0 NormalY=0 NormalZ=-1 AngleXU=-3.14159 Radius=0.0038017 StartAngle=1.5708 EndAngle=4.71217
    g3: LineSegment StartX=24.9553 StartY=48.3956 StartZ=0 EndX=20.1 EndY=48.3945 EndZ=0
    g4: ArcOfCircle CenterX=24.8647 CenterY=46.9018 CenterZ=0 NormalX=0 NormalY=0 NormalZ=1 AngleXU=0 Radius=1.49652 StartAngle=0.124658 EndAngle=1.51027
    g5: ArcOfCircle CenterX=26.3454 CenterY=47.0873 CenterZ=0 NormalX=0 NormalY=0 NormalZ=-1 AngleXU=1.44615 Radius=0.00433199 StartAngle=1.57078 EndAngle=1.69577
    g6: LineSegment StartX=26.3487 StartY=44.0798 StartZ=0 EndX=26.3497 EndY=47.0873 EndZ=0
    g7: LineSegment StartX=26.4696 StartY=43.7703 StartZ=0 EndX=26.3487 EndY=44.0798 EndZ=0
    g8: ArcOfCircle CenterX=26.4661 CenterY=43.7689 CenterZ=0 NormalX=0 NormalY=0 NormalZ=-1 AngleXU=1.19836 Radius=0.00382092 StartAngle=1.57082 EndAngle=4.71239
    g9: LineSegment StartX=26.4625 StartY=43.7675 StartZ=0 EndX=26.3413 EndY=44.0777 EndZ=0
    g10: ArcOfCircle CenterX=26.3448 CenterY=44.0791 CenterZ=0 NormalX=0 NormalY=0 NormalZ=-1 AngleXU=-1.94324 Radius=0.0038017 StartAngle=1.5708 EndAngle=1.94324
    g11: LineSegment StartX=26.341 StartY=44.0791 StartZ=0 EndX=26.341 EndY=47.087 EndZ=0
    g12: ArcOfCircle CenterX=24.8647 CenterY=46.9018 CenterZ=0 NormalX=0 NormalY=0 NormalZ=1 AngleXU=0 Radius=1.48786 StartAngle=0.124804 EndAngle=1.51019
    g13: LineSegment StartX=24.9549 StartY=48.3869 StartZ=0 EndX=20.1 EndY=48.3869 EndZ=0
    g14: ArcOfCircle CenterX=25.6782 CenterY=46.2434 CenterZ=0 NormalX=0 NormalY=0 NormalZ=-1 AngleXU=1.15945 Radius=0.0038017 StartAngle=1.5708 EndAngle=1.67505
    g15: ArcOfCircle CenterX=24.1756 CenterY=45.5879 CenterZ=0 NormalX=0 NormalY=0 NormalZ=1 AngleXU=0 Radius=1.64323 StartAngle=0.411349 EndAngle=1.50814
    g16: LineSegment StartX=20.1 StartY=47.2279 StartZ=0 EndX=24.2785 EndY=47.2279 EndZ=0
    g17: ArcOfCircle CenterX=20.1 CenterY=47.2241 CenterZ=0 NormalX=0 NormalY=0 NormalZ=-1 AngleXU=-3.14159 Radius=0.0038017 StartAngle=1.5708 EndAngle=4.71239
    g18: LineSegment StartX=20.1 StartY=47.2203 StartZ=0 EndX=24.2781 EndY=47.2203 EndZ=0
    g19: ArcOfCircle CenterX=24.1756 CenterY=45.5879 CenterZ=0 NormalX=0 NormalY=0 NormalZ=1 AngleXU=0 Radius=1.63562 StartAngle=0.41147 EndAngle=1.50807
    g20: LineSegment StartX=25.6747 StartY=46.2421 StartZ=0 EndX=26.0588 EndY=45.0307 EndZ=0
    g21: ArcOfCircle CenterX=26.0625 CenterY=45.0318 CenterZ=0 NormalX=0 NormalY=0 NormalZ=-1 AngleXU=1.5708 Radius=0.0038017 StartAngle=1.5708 EndAngle=4.40529
    g22: LineSegment StartX=26.0663 StartY=45.0318 StartZ=0 EndX=26.0663 EndY=47.0161 EndZ=0
    g23: ArcOfCircle CenterX=26.0625 CenterY=47.0161 CenterZ=0 NormalX=0 NormalY=0 NormalZ=-1 AngleXU=1.43371 Radius=0.0038017 StartAngle=1.5708 EndAngle=1.70789
    g24: ArcOfCircle CenterX=24.708 CenterY=46.8292 CenterZ=0 NormalX=0 NormalY=0 NormalZ=1 AngleXU=0 Radius=1.37107 StartAngle=0.13709 EndAngle=1.48292
    g25: ArcOfCircle CenterX=24.828 CenterY=48.1912 CenterZ=0 NormalX=0 NormalY=0 NormalZ=-1 AngleXU=0 Radius=0.0038017 StartAngle=1.5708 EndAngle=1.65868
    g26: LineSegment StartX=24.828 StartY=48.195 StartZ=0 EndX=20.1 EndY=48.195 EndZ=0
    g27: ArcOfCircle CenterX=20.1 CenterY=48.1912 CenterZ=0 NormalX=0 NormalY=0 NormalZ=-1 AngleXU=-3.14159 Radius=0.0038017 StartAngle=1.5708 EndAngle=4.71239
    g28: LineSegment StartX=24.8279 StartY=48.1874 StartZ=0 EndX=20.1 EndY=48.1874 EndZ=0
    g29: ArcOfCircle CenterX=24.708 CenterY=46.8292 CenterZ=0 NormalX=0 NormalY=0 NormalZ=1 AngleXU=0 Radius=1.36347 StartAngle=0.137281 EndAngle=1.48279
    g30: LineSegment StartX=26.0587 StartY=45.0564 StartZ=0 EndX=26.0587 EndY=47.0158 EndZ=0
    g31: LineSegment StartX=25.6818 StartY=46.2446 StartZ=0 EndX=26.0587 EndY=45.0564 EndZ=0
    g32: LineSegment StartX=21.5447 StartY=43.45 StartZ=0 EndX=21.5447 EndY=47.0012 EndZ=0
    g33: ArcOfCircle CenterX=21.5485 CenterY=43.45 CenterZ=0 NormalX=0 NormalY=0 NormalZ=-1 AngleXU=1.5708 Radius=0.0038017 StartAngle=1.5708 EndAngle=4.71239
    g34: LineSegment StartX=21.5523 StartY=43.45 StartZ=0 EndX=21.5523 EndY=46.9974 EndZ=0
    g35: LineSegment StartX=21.5523 StartY=46.9974 StartZ=0 EndX=22.6188 EndY=46.9974 EndZ=0
    g36: LineSegment StartX=22.6188 StartY=46.9974 StartZ=0 EndX=22.6188 EndY=43.45 EndZ=0
    g37: ArcOfCircle CenterX=22.6226 CenterY=43.45 CenterZ=0 NormalX=0 NormalY=0 NormalZ=-1 AngleXU=1.5708 Radius=0.0038017 StartAngle=1.5708 EndAngle=4.71239
    g38: LineSegment StartX=22.6264 StartY=47.0012 StartZ=0 EndX=22.6264 EndY=43.45 EndZ=0
    g39: ArcOfCircle CenterX=22.6226 CenterY=47.0012 CenterZ=0 NormalX=0 NormalY=0 NormalZ=-1 AngleXU=0 Radius=0.0038017 StartAngle=1.5708 EndAngle=3.14159
    g40: LineSegment StartX=21.5485 StartY=47.005 StartZ=0 EndX=22.6226 EndY=47.005 EndZ=0
    g41: ArcOfCircle CenterX=21.5485 CenterY=47.0012 CenterZ=0 NormalX=0 NormalY=0 NormalZ=-1 AngleXU=-1.5708 Radius=0.0038017 StartAngle=1.5708 EndAngle=3.14159
    g42: LineSegment StartX=22.7972 StartY=43.4599 StartZ=0 EndX=22.7972 EndY=46.9987 EndZ=0
    g43: ArcOfCircle CenterX=22.801 CenterY=43.4599 CenterZ=0 NormalX=0 NormalY=0 NormalZ=-1 AngleXU=1.5708 Radius=0.0038017 StartAngle=1.5708 EndAngle=4.71239
    g44: LineSegment StartX=22.8048 StartY=43.4599 StartZ=0 EndX=22.8048 EndY=46.9949 EndZ=0
    g45: LineSegment StartX=22.8048 StartY=46.9949 StartZ=0 EndX=23.8716 EndY=46.9949 EndZ=0
    g46: LineSegment StartX=23.8716 StartY=46.9949 StartZ=0 EndX=23.8716 EndY=43.45 EndZ=0
    g47: ArcOfCircle CenterX=23.8755 CenterY=43.45 CenterZ=0 NormalX=0 NormalY=0 NormalZ=-1 AngleXU=1.5708 Radius=0.0038017 StartAngle=1.5708 EndAngle=4.71239
    g48: LineSegment StartX=23.8793 StartY=46.9987 StartZ=0 EndX=23.8793 EndY=43.45 EndZ=0
    g49: ArcOfCircle CenterX=23.8755 CenterY=46.9987 CenterZ=0 NormalX=0 NormalY=0 NormalZ=-1 AngleXU=0 Radius=0.0038017 StartAngle=1.5708 EndAngle=3.14159
    g50: LineSegment StartX=22.801 StartY=47.0025 StartZ=0 EndX=23.8755 EndY=47.0025 EndZ=0
    g51: ArcOfCircle CenterX=22.801 CenterY=46.9987 CenterZ=0 NormalX=0 NormalY=0 NormalZ=-1 AngleXU=-1.5708 Radius=0.0038017 StartAngle=1.5708 EndAngle=3.14159
    g52: LineSegment StartX=24.1784 StartY=46.9965 StartZ=0 EndX=24.6306 EndY=46.9414 EndZ=0
    g53: ArcOfCircle CenterX=24.1779 CenterY=46.9927 CenterZ=0 NormalX=0 NormalY=0 NormalZ=-1 AngleXU=-1.5708 Radius=0.0038017 StartAngle=1.5708 EndAngle=3.26281
    g54: LineSegment StartX=24.1741 StartY=43.45 StartZ=0 EndX=24.1741 EndY=46.9927 EndZ=0
    g55: ArcOfCircle CenterX=24.1779 CenterY=43.45 CenterZ=0 NormalX=0 NormalY=0 NormalZ=-1 AngleXU=1.5708 Radius=0.0038017 StartAngle=1.5708 EndAngle=4.71239
    g56: LineSegment StartX=24.1817 StartY=43.45 StartZ=0 EndX=24.1817 EndY=46.9884 EndZ=0
    g57: LineSegment StartX=24.1817 StartY=46.9884 StartZ=0 EndX=24.6292 EndY=46.9339 EndZ=0
    g58: ArcOfCircle CenterX=24.189 CenterY=45.8161 CenterZ=0 NormalX=0 NormalY=0 NormalZ=1 AngleXU=0 Radius=1.20138 StartAngle=0.492064 EndAngle=1.19567
    g59: LineSegment StartX=25.2479 StartY=46.3836 StartZ=0 EndX=25.2479 EndY=43.45 EndZ=0
    g60: ArcOfCircle CenterX=25.2517 CenterY=43.45 CenterZ=0 NormalX=0 NormalY=0 NormalZ=-1 AngleXU=1.5708 Radius=0.0038017 StartAngle=1.5708 EndAngle=4.71239
    g61: LineSegment StartX=25.2555 StartY=46.3846 StartZ=0 EndX=25.2555 EndY=43.45 EndZ=0
    g62: ArcOfCircle CenterX=25.2517 CenterY=46.3846 CenterZ=0 NormalX=0 NormalY=0 NormalZ=-1 AngleXU=1.07953 Radius=0.0038017 StartAngle=1.5708 EndAngle=2.06207
    g63: ArcOfCircle CenterX=24.189 CenterY=45.8161 CenterZ=0 NormalX=0 NormalY=0 NormalZ=1 AngleXU=0 Radius=1.20899 StartAngle=0.491271 EndAngle=1.19607
    g64: ArcOfCircle CenterX=24.6301 CenterY=46.9376 CenterZ=0 NormalX=0 NormalY=0 NormalZ=-1 AngleXU=0.121218 Radius=0.0038017 StartAngle=1.5708 EndAngle=1.8243
    g65: ArcOfCircle CenterX=25.4921 CenterY=43.45 CenterZ=0 NormalX=0 NormalY=0 NormalZ=-1 AngleXU=1.5708 Radius=0.0038017 StartAngle=1.5708 EndAngle=4.71239
    g66: LineSegment StartX=25.4959 StartY=43.45 StartZ=0 EndX=25.4959 EndY=45.716 EndZ=0
    g67: LineSegment StartX=25.4959 StartY=45.716 StartZ=0 EndX=25.8809 EndY=44.6345 EndZ=0
    g68: LineSegment StartX=25.8809 StartY=44.6345 StartZ=0 EndX=26.2733 EndY=43.5324 EndZ=0
    g69: ArcOfCircle CenterX=26.2769 CenterY=43.5337 CenterZ=0 NormalX=0 NormalY=0 NormalZ=-1 AngleXU=1.22877 Radius=0.0038017 StartAngle=1.5708 EndAngle=4.71239
    g70: LineSegment StartX=25.8881 StartY=44.6371 StartZ=0 EndX=26.2805 EndY=43.5349 EndZ=0
    g71: LineSegment StartX=25.4957 StartY=45.7392 StartZ=0 EndX=25.8881 EndY=44.6371 EndZ=0
    g72: ArcOfCircle CenterX=25.4921 CenterY=45.738 CenterZ=0 NormalX=0 NormalY=0 NormalZ=-1 AngleXU=-1.5708 Radius=0.0038017 StartAngle=1.5708 EndAngle=4.37037
    g73: LineSegment StartX=25.4883 StartY=43.45 StartZ=0 EndX=25.4883 EndY=45.738 EndZ=0
    g74: ArcOfCircle CenterX=20.103 CenterY=46.9936 CenterZ=0 NormalX=0 NormalY=0 NormalZ=-1 AngleXU=-3.14159 Radius=0.0038017 StartAngle=1.5708 EndAngle=4.71239
    g75: LineSegment StartX=21.365 StartY=46.9974 StartZ=0 EndX=20.103 EndY=46.9974 EndZ=0
    g76: ArcOfCircle CenterX=21.365 CenterY=46.9936 CenterZ=0 NormalX=0 NormalY=0 NormalZ=-1 AngleXU=0 Radius=0.0038017 StartAngle=1.5708 EndAngle=3.14159
    g77: LineSegment StartX=21.3688 StartY=45.2218 StartZ=0 EndX=21.3688 EndY=46.9936 EndZ=0
    g78: LineSegment StartX=21.3688 StartY=43.45 StartZ=0 EndX=21.3688 EndY=45.2218 EndZ=0
    g79: ArcOfCircle CenterX=21.365 CenterY=43.45 CenterZ=0 NormalX=0 NormalY=0 NormalZ=-1 AngleXU=1.5708 Radius=0.0038017 StartAngle=1.5708 EndAngle=4.71239
    g80: LineSegment StartX=21.3611 StartY=43.45 StartZ=0 EndX=21.3611 EndY=45.2218 EndZ=0
    g81: LineSegment StartX=21.3611 StartY=45.2218 StartZ=0 EndX=21.3611 EndY=46.9898 EndZ=0
    g82: LineSegment StartX=21.3611 StartY=46.9898 StartZ=0 EndX=20.103 EndY=46.9898 EndZ=0
  constraints (81):
    c: Tangent(g2,g3) = -1.5708
    c: Tangent(g2,g13) = 1.5708
    c: Tangent(g4,g5) = -1.5708
    c: Tangent(g5,g6) = -1.5708
    c: Coincident(g6,g7)
    c: Tangent(g7,g8) = -1.5708
    c: Tangent(g8,g9) = 1.5708
    c: Tangent(g9,g10) = 1.5708
    c: Tangent(g10,g11) = 1.5708
    c: Coincident(g11,g12)
    c: Coincident(g12,g13)
    c: Tangent(g14,g15) = -1.5708
    c: Tangent(g14,g31) = 1.5708
    c: Tangent(g16,g17) = 1.5708
    c: Tangent(g17,g18) = -1.5708
    c: Coincident(g18,g19)
    c: Coincident(g19,g20)
    c: Tangent(g20,g21) = -1.5708
    c: Tangent(g21,g22) = -1.5708
    c: Tangent(g22,g23) = -1.5708
    c: Tangent(g23,g24) = -1.5708
    c: Tangent(g24,g25) = -1.5708
    c: Tangent(g25,g26) = -1.5708
    c: Tangent(g26,g27) = -1.5708
    c: Tangent(g27,g28) = 1.5708
    c: Coincident(g28,g29)
    c: Coincident(g29,g30)
    c: Coincident(g30,g31)
    c: Tangent(g32,g33) = 1.5708
    c: Tangent(g32,g41) = 1.5708
    c: Tangent(g33,g34) = -1.5708
    c: Coincident(g34,g35)
    c: Coincident(g35,g36)
    c: Tangent(g36,g37) = -1.5708
    c: Tangent(g37,g38) = 1.5708
    c: Tangent(g38,g39) = 1.5708
    c: Tangent(g39,g40) = 1.5708
    c: Tangent(g40,g41) = 1.5708
    c: Tangent(g42,g43) = 1.5708
    c: Tangent(g42,g51) = 1.5708
    c: Tangent(g43,g44) = -1.5708
    c: Coincident(g44,g45)
    c: Coincident(g45,g46)
    c: Tangent(g46,g47) = -1.5708
    c: Tangent(g47,g48) = 1.5708
    c: Tangent(g48,g49) = 1.5708
    c: Tangent(g49,g50) = 1.5708
    c: Tangent(g50,g51) = 1.5708
    c: Tangent(g52,g53) = 1.5708
    c: Tangent(g52,g64) = 1.5708
    c: Tangent(g53,g54) = 1.5708
    c: Tangent(g54,g55) = 1.5708
    c: Tangent(g55,g56) = -1.5708
    c: Coincident(g56,g57)
    c: Coincident(g57,g58)
    c: Coincident(g58,g59)
    c: Tangent(g59,g60) = -1.5708
    c: Tangent(g60,g61) = 1.5708
    c: Tangent(g61,g62) = 1.5708
    c: Tangent(g62,g63) = -1.5708
    c: Tangent(g63,g64) = -1.5708
    c: Tangent(g65,g66) = -1.5708
    c: Tangent(g65,g73) = 1.5708
    c: Coincident(g66,g67)
    c: Coincident(g67,g68)
    c: Tangent(g68,g69) = -1.5708
    c: Tangent(g69,g70) = 1.5708
    c: Coincident(g70,g71)
    c: Tangent(g71,g72) = 1.5708
    c: Tangent(g72,g73) = 1.5708
    c: Tangent(g74,g75) = -1.5708
    c: Tangent(g74,g82) = 1.5708
    c: Tangent(g75,g76) = -1.5708
    c: Tangent(g76,g77) = -1.5708
    c: Coincident(g77,g78)
    c: Tangent(g78,g79) = -1.5708
    c: Tangent(g79,g80) = 1.5708
    c: Coincident(g80,g81)
    c: Coincident(g81,g82)
    c: Coincident(g4,g3)
    c: Coincident(g15,g16)
FEATURE [PartDesign::Pocket] Pocket007
  BaseFeature = -> Pad002
  Direction = (-9.4e-15,0,1)
  Length = 0.15
  Length2 = 5
  Profile = -> Sketch010
  ReferenceAxis = -> Sketch010 [N_Axis]
  Refine = true
  Suppressed = false
  Type = 0
FEATURE [PartDesign::Body] Body005  label="Mixmaster_Sticker4"
  AllowCompound = false
  Group = -> [Binder002,Sketch009,Pad002,Sketch010,Pocket007]
  Origin = -> Origin006
  Tip = -> Pocket007
FEATURE [PartDesign::SubShapeBinder] Binder003
  BindCopyOnChange = 0
  BindMode = 0
  ClaimChildren = false
  Context = -> Body006 [Binder003.]
  Fuse = false
  MakeFace = true
  OffsetFill = false
  OffsetIntersection = false
  OffsetJoinType = 0
  OffsetOpenResult = false
  PartialLoad = false
  Refine = true
  Relative = true
  Support = -> [Body004[Pocket006.Face102]]
  _Version = 2
FEATURE [Sketcher::SketchObject] Sketch011
  ArcFitTolerance = 1e-06
  AttachmentSupport = -> [Binder003]
  ExternalGeometry = -> [Binder003]
  FullyConstrained = true
  MakeInternals = false
  MapMode = 5
  Placement = pos=(9.94e-14,0,-10.7) rot=(1,0,0;3.14159rad)
  sketch-geometry (8):
    g0: LineSegment StartX=2.55 StartY=76.7 StartZ=0 EndX=2.55 EndY=64.05 EndZ=0
    g1: LineSegment StartX=3 StartY=63.6 StartZ=0 EndX=7.1 EndY=63.6 EndZ=0
    g2: LineSegment StartX=7.55 StartY=64.05 StartZ=0 EndX=7.55 EndY=76.7 EndZ=0
    g3: LineSegment StartX=7.55 StartY=76.7 StartZ=0 EndX=2.55 EndY=76.7 EndZ=0
    g4: ArcOfCircle CenterX=7.1 CenterY=64.05 CenterZ=0 NormalX=0 NormalY=0 NormalZ=1 AngleXU=0 Radius=0.45 StartAngle=4.71239 EndAngle=6.28319
    g5: GeomPoint [constr] X=7.55 Y=63.6 Z=0
    g6: ArcOfCircle CenterX=3 CenterY=64.05 CenterZ=0 NormalX=0 NormalY=0 NormalZ=1 AngleXU=0 Radius=0.45 StartAngle=3.14159 EndAngle=4.71239
    g7: GeomPoint [constr] X=2.55 Y=63.6 Z=0
  constraints (21):
    c: Coincident(g2,g3)
    c: Coincident(g3,g0)
    c: Vertical(g0)
    c: Vertical(g2)
    c: Horizontal(g1)
    c: Horizontal(g3)
    c: PointOnObject(g5,g1)
    c: PointOnObject(g5,g2)
    c: Tangent(g1,g4) = -1.5708
    c: Tangent(g2,g4) = -1.5708
    c: PointOnObject(g7,g0)
    c: PointOnObject(g7,g1)
    c: Tangent(g0,g6) = -1.5708
    c: Tangent(g1,g6) = -1.5708
    c: Radius(g6) = 0.45
    c: Radius(g4) = 0.45
    c: DistanceY(g-4,g1) = 0.05
    c: DistanceX(g-5,g0) = 0.05
    c: Radius(g-6) = 0.5
    c: DistanceX(g2,g-3) = 0.05
    c: DistanceY(g0,g-5) = 0.05
FEATURE [PartDesign::Pad] Pad003
  Direction = (9.3e-15,0,-1)
  Length = 0.3
  Length2 = 10
  Profile = -> Sketch011
  ReferenceAxis = -> Sketch011 [N_Axis]
  Refine = true
  Suppressed = false
  Type = 0
FEATURE [Sketcher::SketchObject] Sketch012
  ArcFitTolerance = 1e-06
  AttachmentSupport = -> [Pad003]
  ExternalGeometry = -> [Pad003]
  FullyConstrained = false
  MakeInternals = false
  MapMode = 5
  Placement = pos=(1.014e-13,0,-11) rot=(1,0,0;3.14159rad)
  sketch-geometry (24):
    g0: ArcOfCircle CenterX=4.73475 CenterY=76.7 CenterZ=0 NormalX=0 NormalY=0 NormalZ=-1 AngleXU=-1.5708 Radius=0.0027241 StartAngle=1.5708 EndAngle=4.71239
    g1: LineSegment StartX=4.73747 StartY=76.7 StartZ=0 EndX=4.73747 EndY=72.3333 EndZ=0
    g2: LineSegment StartX=4.73747 StartY=72.3333 StartZ=0 EndX=4.73747 EndY=63.6 EndZ=0
    g3: ArcOfCircle CenterX=4.73475 CenterY=63.6 CenterZ=0 NormalX=0 NormalY=0 NormalZ=-1 AngleXU=1.5708 Radius=0.0027241 StartAngle=1.5708 EndAngle=4.71239
    g4: LineSegment StartX=4.73202 StartY=72.3333 StartZ=0 EndX=4.73202 EndY=63.6 EndZ=0
    g5: LineSegment StartX=4.73202 StartY=76.7 StartZ=0 EndX=4.73202 EndY=72.3333 EndZ=0
    g6: ArcOfCircle CenterX=4.90103 CenterY=63.5924 CenterZ=0 NormalX=0 NormalY=0 NormalZ=-1 AngleXU=1.5708 Radius=0.00255024 StartAngle=1.5708 EndAngle=4.71239
    g7: LineSegment StartX=4.89848 StartY=63.5924 StartZ=0 EndX=4.89848 EndY=67.9616 EndZ=0
    g8: LineSegment StartX=4.89848 StartY=67.9616 StartZ=0 EndX=4.89848 EndY=76.7 EndZ=0
    g9: ArcOfCircle CenterX=4.90103 CenterY=76.7 CenterZ=0 NormalX=0 NormalY=0 NormalZ=-1 AngleXU=-1.5708 Radius=0.00255024 StartAngle=1.5708 EndAngle=4.71239
    g10: LineSegment StartX=4.90358 StartY=67.9616 StartZ=0 EndX=4.90358 EndY=76.7 EndZ=0
    g11: LineSegment StartX=4.90358 StartY=63.5924 StartZ=0 EndX=4.90358 EndY=67.9616 EndZ=0
    g12: ArcOfCircle CenterX=6.68963 CenterY=63.6 CenterZ=0 NormalX=0 NormalY=0 NormalZ=-1 AngleXU=1.5708 Radius=0.00187771 StartAngle=1.5708 EndAngle=4.71239
    g13: LineSegment StartX=6.68775 StartY=63.6 StartZ=0 EndX=6.68775 EndY=67.9667 EndZ=0
    g14: LineSegment StartX=6.68775 StartY=67.9667 StartZ=0 EndX=6.68775 EndY=76.7 EndZ=0
    g15: ArcOfCircle CenterX=6.68963 CenterY=76.7 CenterZ=0 NormalX=0 NormalY=0 NormalZ=-1 AngleXU=-1.5708 Radius=0.00187771 StartAngle=1.5708 EndAngle=4.71239
    g16: LineSegment StartX=6.69151 StartY=67.9667 StartZ=0 EndX=6.69151 EndY=76.7 EndZ=0
    g17: LineSegment StartX=6.69151 StartY=63.6 StartZ=0 EndX=6.69151 EndY=67.9667 EndZ=0
    g18: ArcOfCircle CenterX=6.53045 CenterY=76.7 CenterZ=0 NormalX=0 NormalY=0 NormalZ=-1 AngleXU=-1.5708 Radius=0.00187771 StartAngle=1.5708 EndAngle=4.71239
    g19: LineSegment StartX=6.53233 StartY=76.7 StartZ=0 EndX=6.53233 EndY=72.3333 EndZ=0
    g20: LineSegment StartX=6.53233 StartY=72.3333 StartZ=0 EndX=6.53233 EndY=63.6 EndZ=0
    g21: ArcOfCircle CenterX=6.53045 CenterY=63.6 CenterZ=0 NormalX=0 NormalY=0 NormalZ=-1 AngleXU=1.5708 Radius=0.00187771 StartAngle=1.5708 EndAngle=4.71239
    g22: LineSegment StartX=6.52857 StartY=72.3333 StartZ=0 EndX=6.52857 EndY=63.6 EndZ=0
    g23: LineSegment StartX=6.52857 StartY=76.7 StartZ=0 EndX=6.52857 EndY=72.3333 EndZ=0
  constraints (24):
    c: Tangent(g0,g1) = 1.5708
    c: Tangent(g0,g5) = -1.5708
    c: Coincident(g1,g2)
    c: Tangent(g2,g3) = 1.5708
    c: Tangent(g3,g4) = -1.5708
    c: Coincident(g4,g5)
    c: Tangent(g6,g7) = 1.5708
    c: Tangent(g6,g11) = -1.5708
    c: Coincident(g7,g8)
    c: Tangent(g8,g9) = 1.5708
    c: Tangent(g9,g10) = -1.5708
    c: Coincident(g10,g11)
    c: Tangent(g12,g13) = 1.5708
    c: Tangent(g12,g17) = -1.5708
    c: Coincident(g13,g14)
    c: Tangent(g14,g15) = 1.5708
    c: Tangent(g15,g16) = -1.5708
    c: Coincident(g16,g17)
    c: Tangent(g18,g19) = 1.5708
    c: Tangent(g18,g23) = -1.5708
    c: Coincident(g19,g20)
    c: Tangent(g20,g21) = 1.5708
    c: Tangent(g21,g22) = -1.5708
    c: Coincident(g22,g23)
FEATURE [PartDesign::Pocket] Pocket008
  BaseFeature = -> Pad003
  Direction = (-9.2e-15,0,1)
  Length = 0.15
  Length2 = 5
  Profile = -> Sketch012
  ReferenceAxis = -> Sketch012 [N_Axis]
  Refine = true
  Suppressed = false
  Type = 0
FEATURE [PartDesign::Body] Body006  label="Mixmaster_Sticker5"
  AllowCompound = false
  Group = -> [Binder003,Sketch011,Pad003,Sketch012,Pocket008]
  Origin = -> Origin007
  Tip = -> Pocket008
FEATURE [Part::Feature] Part__Feature003  label="Front Torso"
  shape: bbox 22 x 28.3 x 9.3 mm, 170 faces (baked)
FEATURE [PartDesign::FeatureBase] BaseFeature003
  BaseFeature = -> Part__Feature003
  Suppressed = false
FEATURE [Image::ImagePlane] Sticker003  label="FTS1"
  Placement = pos=(10.9,-11,0) rot=(0,0,1;3.14159rad)
  XSize = 20.16
  YSize = 4
FEATURE [Image::ImagePlane] Sticker2  label="FTS2"
  Placement = pos=(14.85,1,0) rot=(0,0,1;3.14159rad)
  XSize = 7.29539
  YSize = 6.76774
FEATURE [Image::ImagePlane] Sticker3  label="FTS3"
  Placement = pos=(5,2.6,0) rot=(0,0,1;0rad)
  XSize = 5.74113
  YSize = 6.5163
FEATURE [Image::ImagePlane] Sticker004  label="FTS4"
  Placement = pos=(11.05,-15.8,0) rot=(0,0,1;0rad)
  XSize = 5.8
  YSize = 4.91
FEATURE [Sketcher::SketchObject] Sketch013
  ArcFitTolerance = 1e-06
  AttachmentSupport = -> [BaseFeature003]
  ExternalGeometry = -> [BaseFeature003]
  FullyConstrained = true
  MakeInternals = false
  MapMode = 5
  Placement = pos=(1.11e-13,0,-12) rot=(1,0,0;3.14159rad)
  sketch-geometry (14):
    g0: LineSegment StartX=11.75 StartY=0.158333 StartZ=0 EndX=11.75 EndY=-3.2 EndZ=0
    g1: ArcOfCircle CenterX=12.5 CenterY=-3.2 CenterZ=0 NormalX=0 NormalY=0 NormalZ=1 AngleXU=0 Radius=0.75 StartAngle=3.14159 EndAngle=4.71239
    g2: ArcOfCircle CenterX=17.3 CenterY=-3.2 CenterZ=0 NormalX=0 NormalY=0 NormalZ=1 AngleXU=0 Radius=0.75 StartAngle=4.71239 EndAngle=6.28319
    g3: LineSegment StartX=12.5 StartY=-3.95 StartZ=0 EndX=17.3 EndY=-3.95 EndZ=0
    g4: LineSegment StartX=18.05 StartY=-3.2 StartZ=0 EndX=18.05 EndY=1 EndZ=0
    g5: ArcOfCircle CenterX=17.3 CenterY=1 CenterZ=0 NormalX=0 NormalY=0 NormalZ=1 AngleXU=0 Radius=0.75 StartAngle=0 EndAngle=1.5708
    g6: LineSegment StartX=17.3 StartY=1.75 StartZ=0 EndX=13.0405 EndY=1.75 EndZ=0
    g7: LineSegment StartX=13.0405 StartY=1.75 StartZ=0 EndX=11.75 EndY=0.158333 EndZ=0
    g8: LineSegment [constr] StartX=12.5 StartY=-3.2 StartZ=0 EndX=12.5 EndY=-3.95 EndZ=0
    g9: LineSegment [constr] StartX=12.5 StartY=-3.2 StartZ=0 EndX=11.75 EndY=-3.2 EndZ=0
    g10: LineSegment [constr] StartX=18.05 StartY=-3.2 StartZ=0 EndX=17.3 EndY=-3.2 EndZ=0
    g11: LineSegment [constr] StartX=17.3 StartY=-3.2 StartZ=0 EndX=17.3 EndY=-3.95 EndZ=0
    g12: LineSegment [constr] StartX=17.3 StartY=1.75 StartZ=0 EndX=17.3 EndY=1 EndZ=0
    g13: LineSegment [constr] StartX=17.3 StartY=1 StartZ=0 EndX=18.05 EndY=1 EndZ=0
  constraints (39):
    c: Vertical(g0)
    c: Coincident(g1,g0)
    c: Coincident(g3,g1)
    c: Coincident(g3,g2)
    c: Horizontal(g3)
    c: Coincident(g4,g2)
    c: Vertical(g4)
    c: Coincident(g5,g4)
    c: Coincident(g6,g5)
    c: Horizontal(g6)
    c: Coincident(g7,g6)
    c: Coincident(g7,g0)
    c: Radius(g1) = 0.75
    c: Coincident(g8,g1)
    c: Coincident(g8,g1)
    c: Coincident(g9,g1)
    c: Coincident(g9,g0)
    c: Horizontal(g9)
    c: Vertical(g8)
    c: DistanceX(g-7,g0) = 0.5
    c: Distance(g1,g-6) = 0.3
    c: Coincident(g10,g2)
    c: Coincident(g11,g2)
    c: Coincident(g11,g2)
    c: Horizontal(g10)
    c: Vertical(g11)
    c: Coincident(g10,g2)
    c: Radius(g2) = 0.75
    c: DistanceX(g2,g-6) = 0.5
    c: DistanceY(g5,g-5) = 0.3
    c: Coincident(g12,g5)
    c: Coincident(g12,g5)
    c: Coincident(g13,g5)
    c: Coincident(g13,g4)
    c: Vertical(g12)
    c: Horizontal(g13)
    c: Parallel(g-3,g7)
    c: Radius(g5) = 0.75
    c: DistanceX(g-4,g6) = 0.25
FEATURE [PartDesign::Pocket] Pocket009
  BaseFeature = -> BaseFeature003
  Direction = (-9.3e-15,0,1)
  Length = 0.3
  Length2 = 5
  Profile = -> Sketch013
  ReferenceAxis = -> Sketch013 [N_Axis]
  Refine = true
  Suppressed = false
  Type = 0
FEATURE [Sketcher::SketchObject] Sketch014
  ArcFitTolerance = 1e-06
  AttachmentSupport = -> [Pocket009]
  FullyConstrained = false
  MakeInternals = false
  MapMode = 5
  Placement = pos=(1.106e-13,0,-11.9) rot=(1,0,0;3.14159rad)
  sketch-geometry (45):
    g0-g22: Circle [constr] x23 (B-spline internal-alignment scaffolding for g23; pole/knot coordinates omitted)
    g23: BSplineCurve PolesCount=23 KnotsCount=21 Degree=3 IsPeriodic=0
    g24-g44: GeomPoint [constr] x21 (B-spline internal-alignment scaffolding for g23; pole/knot coordinates omitted)
  constraints (5):
    c: Weight(g0) = 1
    c: Equal(g0, g1-g22) x22
    c: InternalAlignment(g0-g22 -> g23) x23
    c: InternalAlignment(g24-g44 -> g23) x21
    c: Coincident(g22,g0)
FEATURE [PartDesign::Pocket] Pocket010
  BaseFeature = -> Pocket009
  Direction = (-9.3e-15,0,1)
  Length = 0.3
  Length2 = 5
  Profile = -> Sketch014
  ReferenceAxis = -> Sketch014 [N_Axis]
  Refine = true
  Suppressed = false
  Type = 0
FEATURE [Sketcher::SketchObject] Sketch015
  ArcFitTolerance = 1e-06
  AttachmentSupport = -> [Pocket010]
  ExternalGeometry = -> [Pocket010]
  FullyConstrained = true
  MakeInternals = false
  MapMode = 5
  Placement = pos=(1.114e-13,0,-12) rot=(1,0,0;3.14159rad)
  sketch-geometry (10):
    g0: ArcOfCircle CenterX=11 CenterY=17.2 CenterZ=0 NormalX=0 NormalY=0 NormalZ=1 AngleXU=0 Radius=0.9 StartAngle=0.522315 EndAngle=2.61928
    g1: LineSegment StartX=10.22 StartY=17.649 StartZ=0 EndX=8.33 EndY=14 EndZ=0
    g2: LineSegment StartX=11.78 StartY=17.649 StartZ=0 EndX=13.67 EndY=14 EndZ=0
    g3: LineSegment StartX=13.3 StartY=13.5 StartZ=0 EndX=8.7 EndY=13.5 EndZ=0
    g4: ArcOfCircle CenterX=8.7 CenterY=13.8869 CenterZ=0 NormalX=0 NormalY=0 NormalZ=1 AngleXU=0 Radius=0.3869 StartAngle=2.84494 EndAngle=4.71239
    g5: ArcOfCircle CenterX=13.3 CenterY=13.8869 CenterZ=0 NormalX=0 NormalY=0 NormalZ=1 AngleXU=0 Radius=0.3869 StartAngle=4.71239 EndAngle=6.57984
    g6: LineSegment [constr] StartX=8.7 StartY=13.8869 StartZ=0 EndX=8.7 EndY=13.5 EndZ=0
    g7: LineSegment [constr] StartX=13.3 StartY=13.8869 StartZ=0 EndX=13.3 EndY=13.5 EndZ=0
    g8: LineSegment [constr] StartX=10.22 StartY=17.649 StartZ=0 EndX=11.78 EndY=17.649 EndZ=0
    g9: LineSegment [constr] StartX=8.33 StartY=14 StartZ=0 EndX=13.67 EndY=14 EndZ=0
  constraints (30):
    c: Coincident(g1,g0)
    c: Coincident(g2,g0)
    c: Horizontal(g3)
    c: Coincident(g4,g1)
    c: Coincident(g4,g3)
    c: Coincident(g5,g3)
    c: Coincident(g5,g2)
    c: Coincident(g6,g4)
    c: Coincident(g6,g3)
    c: Coincident(g7,g5)
    c: Coincident(g7,g3)
    c: Coincident(g8,g0)
    c: Coincident(g8,g0)
    c: Coincident(g9,g1)
    c: Coincident(g9,g2)
    c: Horizontal(g9)
    c: Vertical(g6)
    c: Vertical(g7)
    c: Horizontal(g8)
    c: Radius(g0) = 0.9
    c: DistanceX(g-5,g3) = 0.7
    c: DistanceX(g3,g-4) = 0.7
    c: DistanceX(g-5,g-4) = 6
    c: DistanceX(g-5,g0) = 3
    c: DistanceX(g8,g8) = 1.56
    c: DistanceX(g9,g9) = 5.34
    c: DistanceY(g-5,g3) = 0.5
    c: DistanceY(g-5,g0) = 4.2
    c: DistanceY(g-4,g2) = 1
    c: DistanceX(g2,g-4) = 0.33
FEATURE [PartDesign::Pocket] Pocket011
  BaseFeature = -> Pocket010
  Direction = (-9.3e-15,0,1)
  Length = 0.3
  Length2 = 5
  Profile = -> Sketch015
  ReferenceAxis = -> Sketch015 [N_Axis]
  Refine = true
  Suppressed = false
  Type = 0
FEATURE [Sketcher::SketchObject] Sketch016
  ArcFitTolerance = 1e-06
  AttachmentSupport = -> [Pocket011]
  FullyConstrained = false
  MakeInternals = false
  MapMode = 5
  Placement = pos=(1.021e-13,0,-11) rot=(1,0,0;3.14159rad)
  sketch-geometry (55):
    g0-g24: Circle [constr] x25 (B-spline internal-alignment scaffolding for g25; pole/knot coordinates omitted)
    g25: BSplineCurve PolesCount=28 KnotsCount=26 Degree=3 IsPeriodic=0
    g26-g50: GeomPoint [constr] x25 (B-spline internal-alignment scaffolding for g25; pole/knot coordinates omitted)
    g51: Circle [constr] CenterX=3.9924 CenterY=12.5212 CenterZ=0 NormalX=0 NormalY=0 NormalZ=1 AngleXU=0 Radius=1
    g52: Circle [constr] CenterX=2.20859 CenterY=10.8676 CenterZ=0 NormalX=0 NormalY=0 NormalZ=1 AngleXU=0 Radius=1
    g53: Circle [constr] CenterX=1.12059 CenterY=9.90968 CenterZ=0 NormalX=0 NormalY=0 NormalZ=1 AngleXU=0 Radius=1
    g54: GeomPoint [constr] X=1.73499 Y=10.4508 Z=0
  constraints (13):
    c: Weight(g0) = 1
    c: Equal(g0, g1-g24) x24
    c: InternalAlignment(g0-g24 -> g25) x25
    c: InternalAlignment(g26-g50 -> g25) x25
    c: PointOnObject(g16,g14)
    c: Coincident(g24,g0)
    c: InternalAlignment(g51,g25)
    c: Equal(g51,g0)
    c: InternalAlignment(g52,g25)
    c: Equal(g52,g0)
    c: InternalAlignment(g53,g25)
    c: Equal(g53,g0)
    c: InternalAlignment(g54,g25)
FEATURE [PartDesign::Pocket] Pocket012
  BaseFeature = -> Pocket011
  Direction = (-9.3e-15,0,1)
  Length = 0.3
  Length2 = 5
  Profile = -> Sketch016
  ReferenceAxis = -> Sketch016 [N_Axis]
  Refine = true
  Suppressed = false
  Type = 0
FEATURE [PartDesign::Body] Body007  label="Front_Torso_Stickered"
  AllowCompound = false
  BaseFeature = -> Part__Feature003
  Group = -> [BaseFeature003,Sketch013,Pocket009,Sketch014,Pocket010,Sketch015,Pocket011,Sketch016,Pocket012]
  Origin = -> Origin008
  Tip = -> Pocket012
FEATURE [PartDesign::SubShapeBinder] Binder004
  BindCopyOnChange = 0
  BindMode = 0
  ClaimChildren = false
  Context = -> Body008 [Binder004.]
  Fuse = false
  MakeFace = true
  OffsetFill = false
  OffsetIntersection = false
  OffsetJoinType = 0
  OffsetOpenResult = false
  PartialLoad = false
  Refine = true
  Relative = true
  Support = -> [Body007[Pocket012.Face99]]
  _Version = 2
FEATURE [Sketcher::SketchObject] Sketch017
  ArcFitTolerance = 1e-06
  AttachmentSupport = -> [Binder004]
  FullyConstrained = false
  MakeInternals = false
  MapMode = 5
  Placement = pos=(9.93e-14,0,-10.7) rot=(1,0,0;3.14159rad)
  sketch-geometry (71):
    g0-g12: Circle [constr] x13 (B-spline internal-alignment scaffolding for g13; pole/knot coordinates omitted)
    g13: BSplineCurve PolesCount=36 KnotsCount=34 Degree=3 IsPeriodic=0
    g14-g35: GeomPoint [constr] x22 (B-spline internal-alignment scaffolding for g13; pole/knot coordinates omitted)
    g36: Circle [constr] CenterX=5.28856 CenterY=12.8117 CenterZ=0 NormalX=0 NormalY=0 NormalZ=1 AngleXU=0 Radius=1
    g37: Circle [constr] CenterX=7.09082 CenterY=12.8395 CenterZ=0 NormalX=0 NormalY=0 NormalZ=1 AngleXU=0 Radius=1
    g38: Circle [constr] CenterX=12.5195 CenterY=12.8094 CenterZ=0 NormalX=0 NormalY=0 NormalZ=1 AngleXU=0 Radius=1
    g39: GeomPoint [constr] X=7.57557 Y=12.8305 Z=0
    g40: Circle [constr] CenterX=14.8486 CenterY=12.7959 CenterZ=0 NormalX=0 NormalY=0 NormalZ=1 AngleXU=0 Radius=1
    g41: GeomPoint [constr] X=16.1871 Y=12.7907 Z=0
    g42: Circle [constr] CenterX=16.4566 CenterY=12.7877 CenterZ=0 NormalX=0 NormalY=0 NormalZ=1 AngleXU=0 Radius=1
    g43: Circle [constr] CenterX=17.385 CenterY=12.8042 CenterZ=0 NormalX=0 NormalY=0 NormalZ=1 AngleXU=0 Radius=1
    g44: Circle [constr] CenterX=17.6447 CenterY=12.638 CenterZ=0 NormalX=0 NormalY=0 NormalZ=1 AngleXU=0 Radius=1
    g45: GeomPoint [constr] X=16.9221 Y=12.7921 Z=0
    g46: GeomPoint [constr] X=19.0983 Y=11.3761 Z=0
    g47: Circle [constr] CenterX=17.7466 CenterY=12.6138 CenterZ=0 NormalX=0 NormalY=0 NormalZ=1 AngleXU=0 Radius=1
    g48: Circle [constr] CenterX=18.5018 CenterY=11.9181 CenterZ=0 NormalX=0 NormalY=0 NormalZ=1 AngleXU=0 Radius=1
    g49: GeomPoint [constr] X=18.3802 Y=12.0303 Z=0
    g50: Circle [constr] CenterX=19.1956 CenterY=11.2884 CenterZ=0 NormalX=0 NormalY=0 NormalZ=1 AngleXU=0 Radius=1
    g51: Circle [constr] CenterX=19.9575 CenterY=10.5926 CenterZ=0 NormalX=0 NormalY=0 NormalZ=1 AngleXU=0 Radius=1
    g52: GeomPoint [constr] X=20.1413 Y=10.4249 Z=0
    g53: Circle [constr] CenterX=20.3447 CenterY=10.2393 CenterZ=0 NormalX=0 NormalY=0 NormalZ=1 AngleXU=0 Radius=1
    g54: Circle [constr] CenterX=20.8315 CenterY=9.75469 CenterZ=0 NormalX=0 NormalY=0 NormalZ=1 AngleXU=0 Radius=1
    g55: Circle [constr] CenterX=20.6474 CenterY=9.42428 CenterZ=0 NormalX=0 NormalY=0 NormalZ=1 AngleXU=0 Radius=1
    g56: GeomPoint [constr] X=20.4676 Y=10.1152 Z=0
    g57: GeomPoint [constr] X=6.41821 Y=9.38868 Z=0
    g58: Circle [constr] CenterX=10.8629 CenterY=9.29987 CenterZ=0 NormalX=0 NormalY=0 NormalZ=1 AngleXU=0 Radius=1
    g59: Circle [constr] CenterX=8.22907 CenterY=9.45441 CenterZ=0 NormalX=0 NormalY=0 NormalZ=1 AngleXU=0 Radius=1
    g60: GeomPoint [constr] X=12.4549 Y=9.3346 Z=0
    g61: Circle [constr] CenterX=6.30432 CenterY=9.28511 CenterZ=0 NormalX=0 NormalY=0 NormalZ=1 AngleXU=0 Radius=1
    g62: Circle [constr] CenterX=5.7363 CenterY=9.6956 CenterZ=0 NormalX=0 NormalY=0 NormalZ=1 AngleXU=0 Radius=1
    g63: Circle [constr] CenterX=4.86375 CenterY=10.0525 CenterZ=0 NormalX=0 NormalY=0 NormalZ=1 AngleXU=0 Radius=1
    g64: GeomPoint [constr] X=5.65963 Y=9.71139 Z=0
    g65: Circle [constr] CenterX=13.9328 CenterY=9.35097 CenterZ=0 NormalX=0 NormalY=0 NormalZ=1 AngleXU=0 Radius=1
    g66: GeomPoint [constr] X=14.7771 Y=9.34856 Z=0
    g67: Circle [constr] CenterX=16.78 CenterY=9.9994 CenterZ=0 NormalX=0 NormalY=0 NormalZ=1 AngleXU=0 Radius=1
    g68: Circle [constr] CenterX=15.6147 CenterY=9.33878 CenterZ=0 NormalX=0 NormalY=0 NormalZ=1 AngleXU=0 Radius=1
    g69: Circle [constr] CenterX=14.997 CenterY=9.34803 CenterZ=0 NormalX=0 NormalY=0 NormalZ=1 AngleXU=0 Radius=1
    g70: GeomPoint [constr] X=15.1631 Y=9.35026 Z=0
  constraints (66):
    c: Weight(g0) = 1
    c: Equal(g0, g1-g7) x7
    c: Equal(g0, g9-g12) x4
    c: InternalAlignment(g0-g12 -> g13) x13
    c: InternalAlignment(g14-g34 -> g13) x21
    c: PointOnObject(g11,g8)
    c: Coincident(g12,g0)
    c: InternalAlignment(g35,g13)
    c: InternalAlignment(g36,g13)
    c: Equal(g36,g0)
    c: InternalAlignment(g37,g13)
    c: Equal(g37,g0)
    c: InternalAlignment(g38,g13)
    c: Equal(g38,g0)
    c: InternalAlignment(g39,g13)
    c: InternalAlignment(g40,g13)
    c: Equal(g40,g0)
    c: InternalAlignment(g41,g13)
    c: InternalAlignment(g42,g13)
    c: Equal(g42,g0)
    c: InternalAlignment(g43,g13)
    c: Equal(g43,g0)
    c: InternalAlignment(g44,g13)
    c: Equal(g44,g0)
    c: InternalAlignment(g45,g13)
    c: InternalAlignment(g46,g13)
    c: InternalAlignment(g47,g13)
    c: Equal(g47,g0)
    c: InternalAlignment(g48,g13)
    c: Equal(g48,g0)
    c: InternalAlignment(g49,g13)
    c: InternalAlignment(g50,g13)
    c: Equal(g50,g0)
    c: InternalAlignment(g51,g13)
    c: Equal(g51,g0)
    c: InternalAlignment(g52,g13)
    c: InternalAlignment(g53,g13)
    c: Equal(g53,g0)
    c: InternalAlignment(g54,g13)
    c: Equal(g54,g0)
    c: InternalAlignment(g55,g13)
    c: Equal(g55,g0)
    c: InternalAlignment(g56,g13)
    c: InternalAlignment(g57,g13)
    c: InternalAlignment(g58,g13)
    c: Equal(g58,g0)
    c: InternalAlignment(g59,g13)
    c: Equal(g59,g0)
    c: InternalAlignment(g60,g13)
    c: InternalAlignment(g61,g13)
    c: Equal(g61,g0)
    c: InternalAlignment(g62,g13)
    c: Equal(g62,g0)
    c: InternalAlignment(g63,g13)
    c: Equal(g63,g0)
    c: InternalAlignment(g64,g13)
    c: InternalAlignment(g65,g13)
    c: Equal(g65,g0)
    c: InternalAlignment(g66,g13)
    c: InternalAlignment(g67,g13)
    c: Equal(g67,g0)
    c: InternalAlignment(g68,g13)
    c: Equal(g68,g0)
    c: InternalAlignment(g69,g13)
    c: Equal(g69,g0)
    c: InternalAlignment(g70,g13)
FEATURE [PartDesign::Pad] Pad004
  Direction = (9.3e-15,0,-1)
  Length = 0.3
  Length2 = 10
  Profile = -> Sketch017
  ReferenceAxis = -> Sketch017 [N_Axis]
  Refine = true
  Suppressed = false
  Type = 0
FEATURE [Sketcher::SketchObject] Sketch018
  ArcFitTolerance = 1e-06
  AttachmentSupport = -> [Pad004]
  FullyConstrained = false
  MakeInternals = false
  MapMode = 5
  Placement = pos=(1.021e-13,0,-11) rot=(1,0,0;3.14159rad)
  sketch-geometry (60):
    g0: LineSegment StartX=14.4477 StartY=10.305 StartZ=0 EndX=14.4477 EndY=9.81898 EndZ=0
    g1: LineSegment StartX=14.4477 StartY=9.81898 StartZ=0 EndX=7.47834 EndY=9.81898 EndZ=0
    g2: LineSegment StartX=7.47834 StartY=9.81898 StartZ=0 EndX=7.47834 EndY=10.305 EndZ=0
    g3: LineSegment StartX=7.47834 StartY=10.305 StartZ=0 EndX=14.4477 EndY=10.305 EndZ=0
    g4: LineSegment StartX=7.4916 StartY=10.9714 StartZ=0 EndX=7.4916 EndY=10.4587 EndZ=0
    g5: LineSegment StartX=7.4916 StartY=10.4587 StartZ=0 EndX=14.4761 EndY=10.4587 EndZ=0
    g6: LineSegment StartX=14.4761 StartY=10.4587 StartZ=0 EndX=14.4761 EndY=10.9714 EndZ=0
    g7: LineSegment StartX=14.4761 StartY=10.9714 StartZ=0 EndX=7.4916 EndY=10.9714 EndZ=0
    g8: LineSegment StartX=14.4478 StartY=11.5771 StartZ=0 EndX=7.49572 EndY=11.5771 EndZ=0
    g9: LineSegment StartX=7.49572 StartY=11.5771 StartZ=0 EndX=7.49572 EndY=11.1376 EndZ=0
    g10: LineSegment StartX=7.49572 StartY=11.1376 StartZ=0 EndX=14.4478 EndY=11.1376 EndZ=0
    g11: LineSegment StartX=14.4478 StartY=11.1376 StartZ=0 EndX=14.4478 EndY=11.5771 EndZ=0
    g12: LineSegment StartX=14.4356 StartY=11.1498 StartZ=0 EndX=14.4356 EndY=11.5649 EndZ=0
    g13: LineSegment StartX=14.4356 StartY=11.5649 StartZ=0 EndX=7.508 EndY=11.5649 EndZ=0
    g14: LineSegment StartX=7.508 StartY=11.5649 StartZ=0 EndX=7.508 EndY=11.1498 EndZ=0
    g15: LineSegment StartX=7.508 StartY=11.1498 StartZ=0 EndX=14.4356 EndY=11.1498 EndZ=0
    g16: LineSegment StartX=7.50388 StartY=10.9591 StartZ=0 EndX=7.50388 EndY=10.471 EndZ=0
    g17: LineSegment StartX=7.50388 StartY=10.471 StartZ=0 EndX=14.4638 EndY=10.471 EndZ=0
    g18: LineSegment StartX=14.4638 StartY=10.471 StartZ=0 EndX=14.4638 EndY=10.9591 EndZ=0
    g19: LineSegment StartX=14.4638 StartY=10.9591 StartZ=0 EndX=7.50388 EndY=10.9591 EndZ=0
    g20: LineSegment StartX=14.46 StartY=10.305 StartZ=0 EndX=14.46 EndY=9.81898 EndZ=0
    g21: ArcOfCircle CenterX=14.4477 CenterY=9.81898 CenterZ=0 NormalX=0 NormalY=0 NormalZ=-1 AngleXU=1.5708 Radius=0.0122806 StartAngle=1.5708 EndAngle=3.14159
    g22: LineSegment StartX=14.4477 StartY=9.8067 StartZ=0 EndX=7.47834 EndY=9.8067 EndZ=0
    g23: ArcOfCircle CenterX=7.47834 CenterY=9.81898 CenterZ=0 NormalX=0 NormalY=0 NormalZ=-1 AngleXU=-3.14159 Radius=0.0122806 StartAngle=1.5708 EndAngle=3.14159
    g24: LineSegment StartX=7.46606 StartY=9.81898 StartZ=0 EndX=7.46606 EndY=10.305 EndZ=0
    g25: ArcOfCircle CenterX=7.47834 CenterY=10.305 CenterZ=0 NormalX=0 NormalY=0 NormalZ=-1 AngleXU=-1.5708 Radius=0.0122806 StartAngle=1.5708 EndAngle=3.14159
    g26: LineSegment StartX=7.47834 StartY=10.3173 StartZ=0 EndX=14.4477 EndY=10.3173 EndZ=0
    g27: ArcOfCircle CenterX=14.4477 CenterY=10.305 CenterZ=0 NormalX=0 NormalY=0 NormalZ=-1 AngleXU=0 Radius=0.0122806 StartAngle=1.5708 EndAngle=3.14159
    g28: LineSegment StartX=14.4466 StartY=12.8396 StartZ=0 EndX=14.4466 EndY=11.7489 EndZ=0
    g29: ArcOfCircle CenterX=14.4343 CenterY=12.8396 CenterZ=0 NormalX=0 NormalY=0 NormalZ=-1 AngleXU=-1.5708 Radius=0.0122806 StartAngle=1.5708 EndAngle=4.71239
    g30: LineSegment StartX=14.422 StartY=12.8396 StartZ=0 EndX=14.422 EndY=11.7612 EndZ=0
    g31: LineSegment StartX=14.422 StartY=11.7612 StartZ=0 EndX=7.52468 EndY=11.7612 EndZ=0
    g32: LineSegment StartX=7.52468 StartY=11.7612 StartZ=0 EndX=7.52468 EndY=12.8368 EndZ=0
    g33: ArcOfCircle CenterX=7.5124 CenterY=12.8368 CenterZ=0 NormalX=0 NormalY=0 NormalZ=-1 AngleXU=-1.5708 Radius=0.0122806 StartAngle=1.5708 EndAngle=4.71239
    g34: LineSegment StartX=7.50012 StartY=11.7489 StartZ=0 EndX=7.50012 EndY=12.8368 EndZ=0
    g35: ArcOfCircle CenterX=7.5124 CenterY=11.7489 CenterZ=0 NormalX=0 NormalY=0 NormalZ=-1 AngleXU=-3.14159 Radius=0.0122806 StartAngle=1.5708 EndAngle=3.14159
    g36: LineSegment StartX=14.4343 StartY=11.7366 StartZ=0 EndX=7.5124 EndY=11.7366 EndZ=0
    g37: ArcOfCircle CenterX=14.4343 CenterY=11.7489 CenterZ=0 NormalX=0 NormalY=0 NormalZ=-1 AngleXU=1.5708 Radius=0.0122806 StartAngle=1.5708 EndAngle=3.14159
    g38: LineSegment StartX=7.47481 StartY=9.32025 StartZ=0 EndX=7.47481 EndY=9.6376 EndZ=0
    g39: ArcOfCircle CenterX=7.48709 CenterY=9.32025 CenterZ=0 NormalX=0 NormalY=0 NormalZ=-1 AngleXU=1.5708 Radius=0.0122806 StartAngle=1.5708 EndAngle=4.71239
    g40: LineSegment StartX=7.49937 StartY=9.32025 StartZ=0 EndX=7.49937 EndY=9.62532 EndZ=0
    g41: LineSegment StartX=7.49937 StartY=9.62532 StartZ=0 EndX=14.4649 EndY=9.62532 EndZ=0
    g42: LineSegment StartX=14.4649 StartY=9.62532 StartZ=0 EndX=14.4649 EndY=9.31011 EndZ=0
    g43: ArcOfCircle CenterX=14.4771 CenterY=9.31011 CenterZ=0 NormalX=0 NormalY=0 NormalZ=-1 AngleXU=1.5708 Radius=0.0122806 StartAngle=1.5708 EndAngle=4.71239
    g44: LineSegment StartX=14.4894 StartY=9.6376 StartZ=0 EndX=14.4894 EndY=9.31011 EndZ=0
    g45: ArcOfCircle CenterX=14.4771 CenterY=9.6376 CenterZ=0 NormalX=0 NormalY=0 NormalZ=-1 AngleXU=0 Radius=0.0122806 StartAngle=1.5708 EndAngle=3.14159
    g46: LineSegment StartX=7.48709 StartY=9.64988 StartZ=0 EndX=14.4771 EndY=9.64988 EndZ=0
    g47: ArcOfCircle CenterX=7.48709 CenterY=9.6376 CenterZ=0 NormalX=0 NormalY=0 NormalZ=-1 AngleXU=-1.5708 Radius=0.0122806 StartAngle=1.5708 EndAngle=3.14159
    g48: ArcOfCircle CenterX=17.0353 CenterY=9.94517 CenterZ=0 NormalX=0 NormalY=0 NormalZ=-1 AngleXU=0.680774 Radius=0.0154749 StartAngle=1.5708 EndAngle=4.71239
    g49: LineSegment StartX=17.0256 StartY=9.93314 StartZ=0 EndX=16.5204 EndY=10.3423 EndZ=0
    g50: LineSegment StartX=16.5204 StartY=10.3423 StartZ=0 EndX=15.5099 EndY=11.1607 EndZ=0
    g51: ArcOfCircle CenterX=15.5197 CenterY=11.1728 CenterZ=0 NormalX=0 NormalY=0 NormalZ=-1 AngleXU=-2.46082 Radius=0.0154749 StartAngle=1.5708 EndAngle=4.71239
    g52: LineSegment StartX=16.5399 StartY=10.3664 StartZ=0 EndX=15.5294 EndY=11.1848 EndZ=0
    g53: LineSegment StartX=17.0451 StartY=9.9572 StartZ=0 EndX=16.5399 EndY=10.3664 EndZ=0
    g54: ArcOfCircle CenterX=6.45146 CenterY=11.156 CenterZ=0 NormalX=0 NormalY=0 NormalZ=-1 AngleXU=-0.677472 Radius=0.0154749 StartAngle=1.5708 EndAngle=4.71239
    g55: LineSegment StartX=6.46116 StartY=11.144 StartZ=0 EndX=5.95567 EndY=10.7373 EndZ=0
    g56: LineSegment StartX=5.95567 StartY=10.7373 StartZ=0 EndX=4.94471 EndY=9.924 EndZ=0
    g57: ArcOfCircle CenterX=4.93501 CenterY=9.93606 CenterZ=0 NormalX=0 NormalY=0 NormalZ=-1 AngleXU=2.46412 Radius=0.0154749 StartAngle=1.5708 EndAngle=4.71239
    g58: LineSegment StartX=5.93627 StartY=10.7614 StartZ=0 EndX=4.92531 EndY=9.94812 EndZ=0
    g59: LineSegment StartX=6.44176 StartY=11.1681 StartZ=0 EndX=5.93627 EndY=10.7614 EndZ=0
  constraints (72):
    c: Vertical(g0)
    c: Coincident(g1,g0)
    c: Horizontal(g1)
    c: Coincident(g2,g1)
    c: Vertical(g2)
    c: Coincident(g3,g2)
    c: Coincident(g3,g0)
    c: Horizontal(g3)
    c: Coincident(g4,g5)
    c: Coincident(g5,g6)
    c: Coincident(g6,g7)
    c: Coincident(g7,g4)
    c: Vertical(g4)
    c: Vertical(g6)
    c: Horizontal(g5)
    c: Horizontal(g7)
    c: Coincident(g8,g9)
    c: Coincident(g9,g10)
    c: Coincident(g10,g11)
    c: Coincident(g11,g8)
    c: Horizontal(g8)
    c: Horizontal(g10)
    c: Vertical(g9)
    c: Vertical(g11)
    c: Coincident(g12,g13)
    c: Coincident(g12,g15)
    c: Coincident(g13,g14)
    c: Coincident(g14,g15)
    c: Coincident(g16,g17)
    c: Coincident(g16,g19)
    c: Coincident(g17,g18)
    c: Coincident(g18,g19)
    c: Tangent(g20,g21) = 1.5708
    c: Tangent(g20,g27) = 1.5708
    c: Tangent(g21,g22) = 1.5708
    c: Tangent(g22,g23) = 1.5708
    c: Tangent(g23,g24) = 1.5708
    c: Tangent(g24,g25) = 1.5708
    c: Tangent(g25,g26) = 1.5708
    c: Tangent(g26,g27) = 1.5708
    c: Tangent(g28,g29) = 1.5708
    c: Tangent(g28,g37) = 1.5708
    c: Tangent(g29,g30) = -1.5708
    c: Coincident(g30,g31)
    c: Coincident(g31,g32)
    c: Tangent(g32,g33) = -1.5708
    c: Tangent(g33,g34) = 1.5708
    c: Tangent(g34,g35) = 1.5708
    c: Tangent(g35,g36) = 1.5708
    c: Tangent(g36,g37) = 1.5708
    c: Tangent(g38,g39) = 1.5708
    c: Tangent(g38,g47) = 1.5708
    c: Tangent(g39,g40) = -1.5708
    c: Coincident(g40,g41)
    c: Coincident(g41,g42)
    c: Tangent(g42,g43) = -1.5708
    c: Tangent(g43,g44) = 1.5708
    c: Tangent(g44,g45) = 1.5708
    c: Tangent(g45,g46) = 1.5708
    c: Tangent(g46,g47) = 1.5708
    c: Tangent(g48,g49) = 1.5708
    c: Tangent(g48,g53) = -1.5708
    c: Coincident(g49,g50)
    c: Tangent(g50,g51) = 1.5708
    c: Tangent(g51,g52) = -1.5708
    c: Coincident(g52,g53)
    c: Tangent(g54,g55) = 1.5708
    c: Tangent(g54,g59) = -1.5708
    c: Coincident(g55,g56)
    c: Tangent(g56,g57) = 1.5708
    c: Tangent(g57,g58) = -1.5708
    c: Coincident(g58,g59)
FEATURE [PartDesign::Pocket] Pocket013
  BaseFeature = -> Pad004
  Direction = (-9.3e-15,0,1)
  Length = 0.15
  Length2 = 5
  Profile = -> Sketch018
  ReferenceAxis = -> Sketch018 [N_Axis]
  Refine = true
  Suppressed = false
  Type = 0
FEATURE [Sketcher::SketchObject] Sketch019
  ArcFitTolerance = 1e-06
  AttachmentSupport = -> [Pocket013]
  FullyConstrained = false
  MakeInternals = false
  MapMode = 5
  Placement = pos=(1.021e-13,0,-11) rot=(1,0,0;3.14159rad)
  sketch-geometry (12):
    g0: ArcOfCircle CenterX=6.45108 CenterY=12.8571 CenterZ=0 NormalX=0 NormalY=0 NormalZ=-1 AngleXU=-1.5708 Radius=0.0138681 StartAngle=1.5708 EndAngle=4.71239
    g1: LineSegment StartX=6.46495 StartY=12.8571 StartZ=0 EndX=6.46495 EndY=11.6712 EndZ=0
    g2: LineSegment StartX=6.46495 StartY=11.6712 StartZ=0 EndX=6.46495 EndY=9.29935 EndZ=0
    g3: ArcOfCircle CenterX=6.45108 CenterY=9.29935 CenterZ=0 NormalX=0 NormalY=0 NormalZ=-1 AngleXU=1.5708 Radius=0.0138681 StartAngle=1.5708 EndAngle=4.71239
    g4: LineSegment StartX=6.43721 StartY=11.6712 StartZ=0 EndX=6.43721 EndY=9.29935 EndZ=0
    g5: LineSegment StartX=6.43721 StartY=12.8571 StartZ=0 EndX=6.43721 EndY=11.6712 EndZ=0
    g6: ArcOfCircle CenterX=15.5086 CenterY=12.8552 CenterZ=0 NormalX=0 NormalY=0 NormalZ=-1 AngleXU=-1.5708 Radius=0.0138681 StartAngle=1.5708 EndAngle=4.71239
    g7: LineSegment StartX=15.5224 StartY=12.8552 StartZ=0 EndX=15.5224 EndY=11.6711 EndZ=0
    g8: LineSegment StartX=15.5224 StartY=11.6711 StartZ=0 EndX=15.5224 EndY=9.30268 EndZ=0
    g9: ArcOfCircle CenterX=15.5086 CenterY=9.30268 CenterZ=0 NormalX=0 NormalY=0 NormalZ=-1 AngleXU=1.5708 Radius=0.0138681 StartAngle=1.5708 EndAngle=4.71239
    g10: LineSegment StartX=15.4947 StartY=11.6711 StartZ=0 EndX=15.4947 EndY=9.30268 EndZ=0
    g11: LineSegment StartX=15.4947 StartY=12.8552 StartZ=0 EndX=15.4947 EndY=11.6711 EndZ=0
  constraints (12):
    c: Tangent(g0,g1) = 1.5708
    c: Tangent(g0,g5) = -1.5708
    c: Coincident(g1,g2)
    c: Tangent(g2,g3) = 1.5708
    c: Tangent(g3,g4) = -1.5708
    c: Coincident(g4,g5)
    c: Tangent(g6,g7) = 1.5708
    c: Tangent(g6,g11) = -1.5708
    c: Coincident(g7,g8)
    c: Tangent(g8,g9) = 1.5708
    c: Tangent(g9,g10) = -1.5708
    c: Coincident(g10,g11)
FEATURE [PartDesign::Pocket] Pocket014
  BaseFeature = -> Pocket013
  Direction = (-9.3e-15,0,1)
  Length = 0.15
  Length2 = 5
  Profile = -> Sketch019
  ReferenceAxis = -> Sketch019 [N_Axis]
  Refine = true
  Suppressed = false
  Type = 0
FEATURE [PartDesign::Body] Body008  label="Mixmaster_Sticker6"
  AllowCompound = false
  Group = -> [Binder004,Sketch017,Pad004,Sketch018,Pocket013,Sketch019,Pocket014]
  Origin = -> Origin009
  Tip = -> Pocket014
FEATURE [PartDesign::SubShapeBinder] Binder005
  BindCopyOnChange = 0
  BindMode = 0
  ClaimChildren = false
  Context = -> Body009 [Binder005.]
  Fuse = false
  MakeFace = true
  OffsetFill = false
  OffsetIntersection = false
  OffsetJoinType = 0
  OffsetOpenResult = false
  PartialLoad = false
  Refine = true
  Relative = true
  Support = -> [Body007[Pocket012.Face201]]
  _Version = 2
FEATURE [Sketcher::SketchObject] Sketch020
  ArcFitTolerance = 1e-06
  AttachmentSupport = -> [Binder005]
  FullyConstrained = false
  MakeInternals = false
  MapMode = 5
  Placement = pos=(1.08e-13,0,-11.6) rot=(1,0,0;3.14159rad)
  sketch-geometry (61):
    g0-g17: Circle [constr] x18 (B-spline internal-alignment scaffolding for g18; pole/knot coordinates omitted)
    g18: BSplineCurve PolesCount=31 KnotsCount=29 Degree=3 IsPeriodic=0
    g19-g41: GeomPoint [constr] x23 (B-spline internal-alignment scaffolding for g18; pole/knot coordinates omitted)
    g42: Circle [constr] CenterX=7.24435 CenterY=-0.978281 CenterZ=0 NormalX=0 NormalY=0 NormalZ=1 AngleXU=0 Radius=1
    g43: GeomPoint [constr] X=7.3855 Y=-3.02527 Z=0
    g44: Circle [constr] CenterX=7.48894 CenterY=-3.9589 CenterZ=0 NormalX=0 NormalY=0 NormalZ=1 AngleXU=0 Radius=1
    g45: Circle [constr] CenterX=7.35974 CenterY=-2.89558 CenterZ=0 NormalX=0 NormalY=0 NormalZ=1 AngleXU=0 Radius=1
    g46: GeomPoint [constr] X=7.49456 Y=-4.11161 Z=0
    g47: Circle [constr] CenterX=7.51524 CenterY=-4.42192 CenterZ=0 NormalX=0 NormalY=0 NormalZ=1 AngleXU=0 Radius=1
    g48: GeomPoint [constr] X=7.55336 Y=-4.75985 Z=0
    g49: Circle [constr] CenterX=7.34662 CenterY=-5.42191 CenterZ=0 NormalX=0 NormalY=0 NormalZ=1 AngleXU=0 Radius=1
    g50: Circle [constr] CenterX=7.55541 CenterY=-5.20469 CenterZ=0 NormalX=0 NormalY=0 NormalZ=1 AngleXU=0 Radius=1
    g51: Circle [constr] CenterX=7.58303 CenterY=-5.00914 CenterZ=0 NormalX=0 NormalY=0 NormalZ=1 AngleXU=0 Radius=1
    g52: GeomPoint [constr] X=7.55773 Y=-5.12963 Z=0
    g53: Circle [constr] CenterX=2.40184 CenterY=-5.43704 CenterZ=0 NormalX=0 NormalY=0 NormalZ=1 AngleXU=0 Radius=1
    g54: Circle [constr] CenterX=2.83457 CenterY=-5.52942 CenterZ=0 NormalX=0 NormalY=0 NormalZ=1 AngleXU=0 Radius=1
    g55: Circle [constr] CenterX=3.19933 CenterY=-5.36019 CenterZ=0 NormalX=0 NormalY=0 NormalZ=1 AngleXU=0 Radius=1
    g56: GeomPoint [constr] X=2.93409 Y=-5.47155 Z=0
    g57: Circle [constr] CenterX=2.91089 CenterY=-0.618469 CenterZ=0 NormalX=0 NormalY=0 NormalZ=1 AngleXU=0 Radius=1
    g58: Circle [constr] CenterX=2.684 CenterY=-0.923846 CenterZ=0 NormalX=0 NormalY=0 NormalZ=1 AngleXU=0 Radius=1
    g59: Circle [constr] CenterX=2.6148 CenterY=-2.02775 CenterZ=0 NormalX=0 NormalY=0 NormalZ=1 AngleXU=0 Radius=1
    g60: GeomPoint [constr] X=2.74469 Y=-0.902397 Z=0
  constraints (37):
    c: Weight(g0) = 1
    c: Equal(g0, g1-g17) x17
    c: InternalAlignment(g0-g17 -> g18) x18
    c: InternalAlignment(g19-g41 -> g18) x23
    c: Coincident(g17,g0)
    c: InternalAlignment(g42,g18)
    c: Equal(g42,g0)
    c: InternalAlignment(g43,g18)
    c: InternalAlignment(g44,g18)
    c: Equal(g44,g0)
    c: InternalAlignment(g45,g18)
    c: Equal(g45,g0)
    c: InternalAlignment(g46,g18)
    c: InternalAlignment(g47,g18)
    c: Equal(g47,g0)
    c: InternalAlignment(g48,g18)
    c: InternalAlignment(g49,g18)
    c: Equal(g49,g0)
    c: InternalAlignment(g50,g18)
    c: Equal(g50,g0)
    c: InternalAlignment(g51,g18)
    c: Equal(g51,g0)
    c: InternalAlignment(g52,g18)
    c: InternalAlignment(g53,g18)
    c: Equal(g53,g0)
    c: InternalAlignment(g54,g18)
    c: Equal(g54,g0)
    c: InternalAlignment(g55,g18)
    c: Equal(g55,g0)
    c: InternalAlignment(g56,g18)
    c: InternalAlignment(g57,g18)
    c: Equal(g57,g0)
    c: InternalAlignment(g58,g18)
    c: Equal(g58,g0)
    c: InternalAlignment(g59,g18)
    c: Equal(g59,g0)
    c: InternalAlignment(g60,g18)
FEATURE [PartDesign::Pad] Pad005
  Direction = (9.3e-15,0,-1)
  Length = 0.3
  Length2 = 10
  Profile = -> Sketch020
  ReferenceAxis = -> Sketch020 [N_Axis]
  Refine = true
  Suppressed = false
  Type = 0
FEATURE [Sketcher::SketchObject] Sketch021
  ArcFitTolerance = 1e-06
  AttachmentSupport = -> [Pad005]
  FullyConstrained = false
  MakeInternals = false
  MapMode = 5
  Placement = pos=(1.109e-13,0,-11.9) rot=(1,0,0;3.14159rad)
  sketch-geometry (122):
    g0: LineSegment StartX=3.34387 StartY=-1.12498 StartZ=0 EndX=3.23147 EndY=-2.57289 EndZ=0
    g1: LineSegment StartX=3.23147 StartY=-2.57289 StartZ=0 EndX=4.67656 EndY=-0.485803 EndZ=0
    g2: LineSegment StartX=4.67656 StartY=-0.485803 StartZ=0 EndX=3.34387 EndY=-1.12498 EndZ=0
    g3: LineSegment StartX=5.11953 StartY=-0.489108 StartZ=0 EndX=6.66042 EndY=-2.55923 EndZ=0
    g4: LineSegment StartX=6.66042 StartY=-2.55923 StartZ=0 EndX=6.49843 EndY=-1.10802 EndZ=0
    g5: LineSegment StartX=6.49843 StartY=-1.10802 StartZ=0 EndX=5.11953 EndY=-0.489108 EndZ=0
    g6: LineSegment StartX=4.55449 StartY=-1.8659 StartZ=0 EndX=3.60575 EndY=-2.88075 EndZ=0
    g7: LineSegment StartX=3.60575 StartY=-2.88075 StartZ=0 EndX=4.82886 EndY=-2.45101 EndZ=0
    g8: LineSegment StartX=4.82886 StartY=-2.45101 StartZ=0 EndX=4.55449 EndY=-1.8659 EndZ=0
    g9: LineSegment StartX=5.35116 StartY=-1.85929 StartZ=0 EndX=5.07679 EndY=-2.45101 EndZ=0
    g10: LineSegment StartX=5.07679 StartY=-2.45101 StartZ=0 EndX=6.2999 EndY=-2.89728 EndZ=0
    g11: LineSegment StartX=6.2999 StartY=-2.89728 StartZ=0 EndX=5.35116 EndY=-1.85929 EndZ=0
    g12: LineSegment StartX=4.95432 StartY=-3.32494 StartZ=0 EndX=4.74276 EndY=-3.75137 EndZ=0
    g13: LineSegment StartX=4.74276 StartY=-3.75137 StartZ=0 EndX=5.21217 EndY=-3.75137 EndZ=0
    g14: LineSegment StartX=5.21217 StartY=-3.75137 StartZ=0 EndX=4.95432 EndY=-3.32494 EndZ=0
    g15: LineSegment StartX=4.76256 StartY=-3.73909 StartZ=0 EndX=5.19039 EndY=-3.73909 EndZ=0
    g16: LineSegment StartX=5.19039 StartY=-3.73909 StartZ=0 EndX=4.95539 EndY=-3.35043 EndZ=0
    g17: LineSegment StartX=4.95539 StartY=-3.35043 StartZ=0 EndX=4.76256 EndY=-3.73909 EndZ=0
    g18: LineSegment StartX=3.64891 StartY=-2.85257 StartZ=0 EndX=4.81197 EndY=-2.44393 EndZ=0
    g19: LineSegment StartX=4.81197 StartY=-2.44393 StartZ=0 EndX=4.55107 EndY=-1.88754 EndZ=0
    g20: LineSegment StartX=4.55107 StartY=-1.88754 StartZ=0 EndX=3.64891 EndY=-2.85257 EndZ=0
    g21: LineSegment StartX=5.09355 StartY=-2.44405 StartZ=0 EndX=6.25701 EndY=-2.86856 EndZ=0
    g22: LineSegment StartX=6.25701 StartY=-2.86856 StartZ=0 EndX=5.35454 EndY=-1.88119 EndZ=0
    g23: LineSegment StartX=5.35454 StartY=-1.88119 StartZ=0 EndX=5.09355 EndY=-2.44405 EndZ=0
    g24: LineSegment StartX=6.64318 StartY=-2.5155 StartZ=0 EndX=6.48701 EndY=-1.11635 EndZ=0
    g25: LineSegment StartX=6.48701 StartY=-1.11635 StartZ=0 EndX=5.15757 EndY=-0.519645 EndZ=0
    g26: LineSegment StartX=5.15757 StartY=-0.519645 StartZ=0 EndX=6.64318 EndY=-2.5155 EndZ=0
    g27: LineSegment StartX=4.64007 StartY=-0.516924 StartZ=0 EndX=3.35557 EndY=-1.133 EndZ=0
    g28: LineSegment StartX=3.35557 StartY=-1.133 StartZ=0 EndX=3.24723 EndY=-2.52855 EndZ=0
    g29: LineSegment StartX=3.24723 StartY=-2.52855 StartZ=0 EndX=4.64007 EndY=-0.516924 EndZ=0
    g30: LineSegment StartX=4.95165 StartY=-2.68886 StartZ=0 EndX=4.57003 EndY=-3.04882 EndZ=0
    g31: LineSegment StartX=4.57003 StartY=-3.04882 StartZ=0 EndX=4.40211 EndY=-4.76367 EndZ=0
    g32: LineSegment StartX=4.40211 StartY=-4.76367 StartZ=0 EndX=4.86222 EndY=-4.10058 EndZ=0
    g33: LineSegment StartX=4.86222 StartY=-4.10058 StartZ=0 EndX=5.05167 EndY=-4.10058 EndZ=0
    g34: LineSegment StartX=5.05167 StartY=-4.10058 StartZ=0 EndX=5.50676 EndY=-4.75884 EndZ=0
    g35: LineSegment StartX=5.50676 StartY=-4.75884 StartZ=0 EndX=5.34397 EndY=-3.04235 EndZ=0
    g36: LineSegment StartX=5.34397 StartY=-3.04235 StartZ=0 EndX=4.95165 EndY=-2.68886 EndZ=0
    g37: LineSegment StartX=4.40539 StartY=-4.76595 StartZ=0 EndX=4.8643 EndY=-4.10457 EndZ=0
    g38: LineSegment StartX=4.8643 StartY=-4.10457 StartZ=0 EndX=5.04958 EndY=-4.10457 EndZ=0
    g39: LineSegment StartX=5.04958 StartY=-4.10457 StartZ=0 EndX=5.50348 EndY=-4.76111 EndZ=0
    g40: ArcOfCircle CenterX=5.50676 CenterY=-4.75884 CenterZ=0 NormalX=0 NormalY=0 NormalZ=-1 AngleXU=1.47624 Radius=0.00398634 StartAngle=1.5708 EndAngle=4.20204
    g41: LineSegment StartX=5.51073 StartY=-4.75847 StartZ=0 EndX=5.34794 EndY=-3.04197 EndZ=0
    g42: ArcOfCircle CenterX=5.34397 CenterY=-3.04235 CenterZ=0 NormalX=0 NormalY=0 NormalZ=-1 AngleXU=0.733375 Radius=0.00398634 StartAngle=1.5708 EndAngle=2.31366
    g43: LineSegment StartX=5.34664 StartY=-3.03939 StartZ=0 EndX=4.95432 EndY=-2.6859 EndZ=0
    g44: ArcOfCircle CenterX=4.95165 CenterY=-2.68886 CenterZ=0 NormalX=0 NormalY=0 NormalZ=-1 AngleXU=-0.756209 Radius=0.00398634 StartAngle=1.5708 EndAngle=3.06038
    g45: LineSegment StartX=4.94891 StartY=-2.68596 StartZ=0 EndX=4.5673 EndY=-3.04592 EndZ=0
    g46: ArcOfCircle CenterX=4.57003 CenterY=-3.04882 CenterZ=0 NormalX=0 NormalY=0 NormalZ=-1 AngleXU=-1.47319 Radius=0.00398634 StartAngle=1.5708 EndAngle=2.28777
    g47: LineSegment StartX=4.56607 StartY=-3.04843 StartZ=0 EndX=4.39815 EndY=-4.76328 EndZ=0
    g48: ArcOfCircle CenterX=4.40211 CenterY=-4.76367 CenterZ=0 NormalX=0 NormalY=0 NormalZ=-1 AngleXU=2.1774 Radius=0.00398634 StartAngle=1.5708 EndAngle=4.20339
    g49: LineSegment StartX=4.90587 StartY=-0.44105 StartZ=0 EndX=3.15647 EndY=-2.86997 EndZ=0
    g50: LineSegment StartX=3.15647 StartY=-2.86997 StartZ=0 EndX=3.02005 EndY=-4.96098 EndZ=0
    g51: LineSegment StartX=3.02005 StartY=-4.96098 StartZ=0 EndX=3.31395 EndY=-4.47659 EndZ=0
    g52: LineSegment StartX=3.31395 StartY=-4.47659 StartZ=0 EndX=3.60242 EndY=-4.28247 EndZ=0
    g53: LineSegment StartX=3.60242 StartY=-4.28247 StartZ=0 EndX=4.36317 EndY=-3.99496 EndZ=0
    g54: LineSegment StartX=4.36317 StartY=-3.99496 StartZ=0 EndX=4.39945 EndY=-3.53415 EndZ=0
    g55: LineSegment StartX=4.39945 StartY=-3.53415 StartZ=0 EndX=3.81891 EndY=-3.84619 EndZ=0
    g56: LineSegment StartX=3.81891 StartY=-3.84619 StartZ=0 EndX=3.72457 EndY=-3.73371 EndZ=0
    g57: LineSegment StartX=3.72457 StartY=-3.73371 StartZ=0 EndX=4.40646 EndY=-3.39989 EndZ=0
    g58: LineSegment StartX=4.40646 StartY=-3.39989 StartZ=0 EndX=4.40646 EndY=-3.11901 EndZ=0
    g59: LineSegment StartX=4.40646 StartY=-3.11901 StartZ=0 EndX=3.80973 EndY=-3.42017 EndZ=0
    g60: LineSegment StartX=3.80973 StartY=-3.42017 StartZ=0 EndX=3.75556 EndY=-3.34269 EndZ=0
    g61: LineSegment StartX=3.75556 StartY=-3.34269 StartZ=0 EndX=4.57558 EndY=-2.91998 EndZ=0
    g62: LineSegment StartX=4.57558 StartY=-2.91998 StartZ=0 EndX=4.87856 EndY=-2.62608 EndZ=0
    g63: LineSegment StartX=4.87856 StartY=-2.62608 StartZ=0 EndX=5.02007 EndY=-2.62608 EndZ=0
    g64: LineSegment StartX=5.02007 StartY=-2.62608 StartZ=0 EndX=5.33755 EndY=-2.91273 EndZ=0
    g65: LineSegment StartX=5.33755 StartY=-2.91273 StartZ=0 EndX=6.15873 EndY=-3.33776 EndZ=0
    g66: LineSegment StartX=6.15873 StartY=-3.33776 StartZ=0 EndX=6.09341 EndY=-3.41577 EndZ=0
    g67: LineSegment StartX=6.09341 StartY=-3.41577 StartZ=0 EndX=5.49835 EndY=-3.12187 EndZ=0
    g68: LineSegment StartX=5.49835 StartY=-3.12187 StartZ=0 EndX=5.48565 EndY=-3.40126 EndZ=0
    g69: LineSegment StartX=5.48565 StartY=-3.40126 StartZ=0 EndX=6.1678 EndY=-3.74233 EndZ=0
    g70: LineSegment StartX=6.1678 StartY=-3.74233 StartZ=0 EndX=6.10067 EndY=-3.84392 EndZ=0
    g71: LineSegment StartX=6.10067 StartY=-3.84392 StartZ=0 EndX=5.51287 EndY=-3.54095 EndZ=0
    g72: LineSegment StartX=5.51287 StartY=-3.54095 StartZ=0 EndX=5.52919 EndY=-3.99995 EndZ=0
    g73: LineSegment StartX=5.52919 StartY=-3.99995 StartZ=0 EndX=6.28572 EndY=-4.28659 EndZ=0
    g74: LineSegment StartX=6.28572 StartY=-4.28659 StartZ=0 EndX=6.60337 EndY=-4.48864 EndZ=0
    g75: LineSegment StartX=6.60337 StartY=-4.48864 StartZ=0 EndX=6.88458 EndY=-4.9676 EndZ=0
    g76: LineSegment StartX=6.88458 StartY=-4.9676 StartZ=0 EndX=6.74487 EndY=-2.86374 EndZ=0
    g77: LineSegment StartX=6.74487 StartY=-2.86374 StartZ=0 EndX=4.90587 EndY=-0.44105 EndZ=0
    g78: LineSegment StartX=6.14866 StartY=-3.33978 StartZ=0 EndX=6.09173 EndY=-3.40778 EndZ=0
    g79: LineSegment StartX=6.09173 StartY=-3.40778 StartZ=0 EndX=5.5012 EndY=-3.11611 EndZ=0
    g80: ArcOfCircle CenterX=5.49835 CenterY=-3.12187 CenterZ=0 NormalX=0 NormalY=0 NormalZ=-1 AngleXU=-1.52537 Radius=0.00641869 StartAngle=1.5708 EndAngle=3.55493
    g81: LineSegment StartX=5.49194 StartY=-3.12158 StartZ=0 EndX=5.47924 EndY=-3.40096 EndZ=0
    g82: ArcOfCircle CenterX=5.48565 CenterY=-3.40126 CenterZ=0 NormalX=0 NormalY=0 NormalZ=-1 AngleXU=-2.67795 Radius=0.00641869 StartAngle=1.5708 EndAngle=2.72337
    g83: LineSegment StartX=5.48278 StartY=-3.407 StartZ=0 EndX=6.15845 EndY=-3.74483 EndZ=0
    g84: LineSegment StartX=6.15845 StartY=-3.74483 StartZ=0 EndX=6.09849 EndY=-3.83558 EndZ=0
    g85: LineSegment StartX=6.09849 StartY=-3.83558 StartZ=0 EndX=5.51581 EndY=-3.53524 EndZ=0
    g86: ArcOfCircle CenterX=5.51287 CenterY=-3.54095 CenterZ=0 NormalX=0 NormalY=0 NormalZ=-1 AngleXU=-1.60635 Radius=0.00641869 StartAngle=1.5708 EndAngle=3.65307
    g87: LineSegment StartX=5.50645 StartY=-3.54118 StartZ=0 EndX=5.52278 EndY=-4.00017 EndZ=0
    g88: ArcOfCircle CenterX=5.52919 CenterY=-3.99995 CenterZ=0 NormalX=0 NormalY=0 NormalZ=-1 AngleXU=-2.77941 Radius=0.00641869 StartAngle=1.5708 EndAngle=2.74385
    g89: LineSegment StartX=5.52692 StartY=-4.00595 StartZ=0 EndX=6.28283 EndY=-4.29236 EndZ=0
    g90: LineSegment StartX=6.28283 StartY=-4.29236 StartZ=0 EndX=6.59862 EndY=-4.49323 EndZ=0
    g91: LineSegment StartX=6.59862 StartY=-4.49323 StartZ=0 EndX=6.87904 EndY=-4.97085 EndZ=0
    g92: ArcOfCircle CenterX=6.88458 CenterY=-4.9676 CenterZ=0 NormalX=0 NormalY=0 NormalZ=-1 AngleXU=1.50449 Radius=0.00641869 StartAngle=1.5708 EndAngle=4.2478
    g93: LineSegment StartX=6.89098 StartY=-4.96717 StartZ=0 EndX=6.75127 EndY=-2.86332 EndZ=0
    g94: ArcOfCircle CenterX=6.74487 CenterY=-2.86374 CenterZ=0 NormalX=0 NormalY=0 NormalZ=-1 AngleXU=0.921515 Radius=0.00641869 StartAngle=1.5708 EndAngle=2.15377
    g95: LineSegment StartX=6.74998 StartY=-2.85986 StartZ=0 EndX=4.91098 EndY=-0.437169 EndZ=0
    g96: ArcOfCircle CenterX=4.90587 CenterY=-0.44105 CenterZ=0 NormalX=0 NormalY=0 NormalZ=-1 AngleXU=-0.946616 Radius=0.00641869 StartAngle=1.5708 EndAngle=3.43893
    g97: LineSegment StartX=4.90066 StartY=-0.437299 StartZ=0 EndX=3.15126 EndY=-2.86621 EndZ=0
    g98: ArcOfCircle CenterX=3.15647 CenterY=-2.86997 CenterZ=0 NormalX=0 NormalY=0 NormalZ=-1 AngleXU=-1.50565 Radius=0.00641869 StartAngle=1.5708 EndAngle=2.12983
    g99: LineSegment StartX=3.15006 StartY=-2.86955 StartZ=0 EndX=3.01365 EndY=-4.96056 EndZ=0
    g100: ArcOfCircle CenterX=3.02005 CenterY=-4.96098 CenterZ=0 NormalX=0 NormalY=0 NormalZ=-1 AngleXU=2.11616 Radius=0.00641869 StartAngle=1.5708 EndAngle=4.23217
    g101: LineSegment StartX=3.02554 StartY=-4.96431 StartZ=0 EndX=3.31871 EndY=-4.48112 EndZ=0
    g102: LineSegment StartX=3.31871 StartY=-4.48112 StartZ=0 EndX=3.60538 EndY=-4.28821 EndZ=0
    g103: LineSegment StartX=3.60538 StartY=-4.28821 StartZ=0 EndX=4.36544 EndY=-4.00096 EndZ=0
    g104: ArcOfCircle CenterX=4.36317 CenterY=-3.99496 CenterZ=0 NormalX=0 NormalY=0 NormalZ=-1 AngleXU=1.64937 Radius=0.00641869 StartAngle=1.5708 EndAngle=2.70168
    g105: LineSegment StartX=4.36957 StartY=-3.99546 StartZ=0 EndX=4.40585 EndY=-3.53465 EndZ=0
    g106: ArcOfCircle CenterX=4.39945 CenterY=-3.53415 CenterZ=0 NormalX=0 NormalY=0 NormalZ=-1 AngleXU=-0.493196 Radius=0.00641869 StartAngle=1.5708 EndAngle=3.71337
    g107: LineSegment StartX=4.39642 StartY=-3.52849 StartZ=0 EndX=3.82047 EndY=-3.83806 EndZ=0
    g108: LineSegment StartX=3.82047 StartY=-3.83806 StartZ=0 EndX=3.73476 EndY=-3.73587 EndZ=0
    g109: LineSegment StartX=3.73476 StartY=-3.73587 StartZ=0 EndX=4.40928 EndY=-3.40566 EndZ=0
    g110: ArcOfCircle CenterX=4.40646 CenterY=-3.39989 CenterZ=0 NormalX=0 NormalY=0 NormalZ=-1 AngleXU=1.5708 Radius=0.00641869 StartAngle=1.5708 EndAngle=2.68634
    g111: LineSegment StartX=4.41288 StartY=-3.39989 StartZ=0 EndX=4.41288 EndY=-3.11901 EndZ=0
    g112: ArcOfCircle CenterX=4.40646 CenterY=-3.11901 CenterZ=0 NormalX=0 NormalY=0 NormalZ=-1 AngleXU=-0.46739 Radius=0.00641869 StartAngle=1.5708 EndAngle=3.60898
    g113: LineSegment StartX=4.40357 StartY=-3.11328 StartZ=0 EndX=3.81181 EndY=-3.41193 EndZ=0
    g114: LineSegment StartX=3.81181 StartY=-3.41193 StartZ=0 EndX=3.76503 EndY=-3.34504 EndZ=0
    g115: LineSegment StartX=3.76503 StartY=-3.34504 StartZ=0 EndX=4.57852 EndY=-2.92569 EndZ=0
    g116: ArcOfCircle CenterX=4.57558 CenterY=-2.91998 CenterZ=0 NormalX=0 NormalY=0 NormalZ=-1 AngleXU=2.37139 Radius=0.00641869 StartAngle=1.5708 EndAngle=1.86504
    g117: LineSegment StartX=4.58005 StartY=-2.92459 StartZ=0 EndX=4.88116 EndY=-2.6325 EndZ=0
    g118: LineSegment StartX=4.88116 StartY=-2.6325 StartZ=0 EndX=5.0176 EndY=-2.6325 EndZ=0
    g119: LineSegment StartX=5.0176 StartY=-2.6325 StartZ=0 EndX=5.33325 EndY=-2.91749 EndZ=0
    g120: ArcOfCircle CenterX=5.33755 CenterY=-2.91273 CenterZ=0 NormalX=0 NormalY=0 NormalZ=-1 AngleXU=-2.66397 Radius=0.00641869 StartAngle=1.5708 EndAngle=1.82757
    g121: LineSegment StartX=5.3346 StartY=-2.91843 StartZ=0 EndX=6.14866 EndY=-3.33978 EndZ=0
  constraints (126):
    c: Coincident(g1,g0)
    c: Coincident(g2,g1)
    c: Coincident(g2,g0)
    c: Coincident(g4,g3)
    c: Coincident(g5,g4)
    c: Coincident(g5,g3)
    c: Coincident(g7,g6)
    c: Coincident(g8,g7)
    c: Coincident(g8,g6)
    c: Coincident(g10,g9)
    c: Coincident(g11,g10)
    c: Coincident(g11,g9)
    c: Coincident(g13,g12)
    c: Horizontal(g13)
    c: Coincident(g14,g13)
    c: Coincident(g14,g12)
    c: Coincident(g15,g16)
    c: Coincident(g15,g17)
    c: Coincident(g16,g17)
    c: Coincident(g18,g19)
    c: Coincident(g18,g20)
    c: Coincident(g19,g20)
    c: Coincident(g21,g22)
    c: Coincident(g21,g23)
    c: Coincident(g22,g23)
    c: Coincident(g24,g25)
    c: Coincident(g24,g26)
    c: Coincident(g25,g26)
    c: Coincident(g27,g28)
    c: Coincident(g27,g29)
    c: Coincident(g28,g29)
    c: Coincident(g31,g30)
    c: Coincident(g32,g31)
    c: Coincident(g33,g32)
    c: Horizontal(g33)
    c: Coincident(g34,g33)
    c: Coincident(g35,g34)
    c: Coincident(g36,g35)
    c: Coincident(g36,g30)
    c: Coincident(g37,g38)
    c: Tangent(g37,g48) = -1.5708
    c: Coincident(g38,g39)
    c: Tangent(g39,g40) = -1.5708
    c: Tangent(g40,g41) = -1.5708
    c: Tangent(g41,g42) = -1.5708
    c: Tangent(g42,g43) = -1.5708
    c: Tangent(g43,g44) = -1.5708
    c: Tangent(g44,g45) = -1.5708
    c: Tangent(g45,g46) = -1.5708
    c: Tangent(g46,g47) = -1.5708
    c: Tangent(g47,g48) = -1.5708
    c: Coincident(g50,g49)
    c: Coincident(g51,g50)
    c: Coincident(g52,g51)
    c: Coincident(g53,g52)
    c: Coincident(g54,g53)
    c: Coincident(g55,g54)
    c: Coincident(g56,g55)
    c: Coincident(g57,g56)
    c: Coincident(g58,g57)
    c: Vertical(g58)
    c: Coincident(g59,g58)
    c: Coincident(g60,g59)
    c: Coincident(g61,g60)
    c: Coincident(g62,g61)
    c: Coincident(g63,g62)
    c: Horizontal(g63)
    c: Coincident(g64,g63)
    c: Coincident(g65,g64)
    c: Coincident(g66,g65)
    c: Coincident(g67,g66)
    c: Coincident(g68,g67)
    c: Coincident(g69,g68)
    c: Coincident(g70,g69)
    c: Coincident(g71,g70)
    c: Coincident(g72,g71)
    c: Coincident(g73,g72)
    c: Coincident(g74,g73)
    c: Coincident(g75,g74)
    c: Coincident(g76,g75)
    c: Coincident(g77,g76)
    c: Coincident(g77,g49)
    c: Coincident(g78,g79)
    c: Coincident(g78,g121)
    c: Tangent(g79,g80) = -1.5708
    c: Tangent(g80,g81) = -1.5708
    c: Tangent(g81,g82) = -1.5708
    c: Tangent(g82,g83) = -1.5708
    c: Coincident(g83,g84)
    c: Coincident(g84,g85)
    c: Tangent(g85,g86) = -1.5708
    c: Tangent(g86,g87) = -1.5708
    c: Tangent(g87,g88) = -1.5708
    c: Tangent(g88,g89) = -1.5708
    c: Coincident(g89,g90)
    c: Coincident(g90,g91)
    c: Tangent(g91,g92) = -1.5708
    c: Tangent(g92,g93) = -1.5708
    c: Tangent(g93,g94) = -1.5708
    c: Tangent(g94,g95) = -1.5708
    c: Tangent(g95,g96) = -1.5708
    c: Tangent(g96,g97) = -1.5708
    c: Tangent(g97,g98) = -1.5708
    c: Tangent(g98,g99) = -1.5708
    c: Tangent(g99,g100) = -1.5708
    c: Tangent(g100,g101) = -1.5708
    c: Coincident(g101,g102)
    c: Coincident(g102,g103)
    c: Tangent(g103,g104) = -1.5708
    c: Tangent(g104,g105) = -1.5708
    c: Tangent(g105,g106) = -1.5708
    c: Tangent(g106,g107) = -1.5708
    c: Coincident(g107,g108)
    c: Coincident(g108,g109)
    c: Tangent(g109,g110) = -1.5708
    c: Tangent(g110,g111) = -1.5708
    c: Tangent(g111,g112) = -1.5708
    c: Tangent(g112,g113) = -1.5708
    c: Coincident(g113,g114)
    c: Coincident(g114,g115)
    c: Tangent(g115,g116) = -1.5708
    c: Tangent(g116,g117) = -1.5708
    c: Coincident(g117,g118)
    c: Coincident(g118,g119)
    c: Tangent(g119,g120) = -1.5708
    c: Tangent(g120,g121) = -1.5708
FEATURE [PartDesign::Pocket] Pocket015
  BaseFeature = -> Pad005
  Direction = (-9.3e-15,0,1)
  Length = 0.15
  Length2 = 5
  Profile = -> Sketch021
  ReferenceAxis = -> Sketch021 [N_Axis]
  Refine = true
  Suppressed = false
  Type = 0
FEATURE [PartDesign::Body] Body009  label="Mixmaster_Sticker7"
  AllowCompound = false
  Group = -> [Binder005,Sketch020,Pad005,Sketch021,Pocket015]
  Origin = -> Origin010
  Tip = -> Pocket015
FEATURE [PartDesign::SubShapeBinder] Binder006
  BindCopyOnChange = 0
  BindMode = 0
  ClaimChildren = false
  Context = -> Body010 [Binder006.]
  Fuse = false
  MakeFace = true
  OffsetFill = false
  OffsetIntersection = false
  OffsetJoinType = 0
  OffsetOpenResult = false
  PartialLoad = false
  Refine = true
  Relative = true
  Support = -> [Body007[Pocket012.Face74]]
  _Version = 2
FEATURE [Sketcher::SketchObject] Sketch022
  ArcFitTolerance = 1e-06
  AttachmentSupport = -> [Binder006]
  ExternalGeometry = -> [Binder006]
  FullyConstrained = true
  MakeInternals = false
  MapMode = 5
  Placement = pos=(1.073e-13,0,-11.7) rot=(1,0,0;3.14159rad)
  sketch-geometry (12):
    g0: LineSegment StartX=10.2716 StartY=17.64 StartZ=0 EndX=8.43639 EndY=14.0967 EndZ=0
    g1: LineSegment StartX=8.7 StartY=13.55 StartZ=0 EndX=13.3 EndY=13.55 EndZ=0
    g2: LineSegment StartX=13.5636 StartY=14.0967 StartZ=0 EndX=11.7284 EndY=17.64 EndZ=0
    g3: ArcOfCircle CenterX=11 CenterY=17.2 CenterZ=0 NormalX=0 NormalY=0 NormalZ=1 AngleXU=0 Radius=0.850939 StartAngle=0.543431 EndAngle=2.59816
    g4: ArcOfCircle CenterX=8.7 CenterY=13.8869 CenterZ=0 NormalX=0 NormalY=0 NormalZ=1 AngleXU=0 Radius=0.3369 StartAngle=2.46942 EndAngle=4.71239
    g5: ArcOfCircle CenterX=13.3 CenterY=13.8869 CenterZ=0 NormalX=0 NormalY=0 NormalZ=1 AngleXU=0 Radius=0.3369 StartAngle=4.71239 EndAngle=6.95536
    g6: LineSegment [constr] StartX=13.5636 StartY=14.0967 StartZ=0 EndX=8.43639 EndY=14.0967 EndZ=0
    g7: LineSegment [constr] StartX=10.2716 StartY=17.64 StartZ=0 EndX=11.7284 EndY=17.64 EndZ=0
    g8: LineSegment [constr] StartX=8.7 StartY=13.8869 StartZ=0 EndX=8.7 EndY=13.55 EndZ=0
    g9: LineSegment [constr] StartX=13.3 StartY=13.8869 StartZ=0 EndX=13.3 EndY=13.55 EndZ=0
    g10: LineSegment [constr] StartX=11.7743 StartY=17.5512 StartZ=0 EndX=11.8187 EndY=17.5742 EndZ=0
    g11: LineSegment [constr] StartX=10.1935 StartY=17.489 StartZ=0 EndX=10.1491 EndY=17.512 EndZ=0
  constraints (34):
    c: Horizontal(g1)
    c: Coincident(g3,g2)
    c: Coincident(g3,g0)
    c: Coincident(g4,g1)
    c: Coincident(g4,g0)
    c: Coincident(g5,g2)
    c: Coincident(g5,g1)
    c: Coincident(g6,g2)
    c: Coincident(g6,g0)
    c: Horizontal(g6)
    c: Coincident(g7,g0)
    c: Coincident(g7,g2)
    c: Horizontal(g7)
    c: Parallel(g2,g-3)
    c: Parallel(g0,g-4)
    c: Coincident(g4,g-7)
    c: Coincident(g-8,g5)
    c: Coincident(g3,g-5)
    c: Coincident(g8,g4)
    c: Coincident(g8,g1)
    c: Coincident(g9,g5)
    c: Coincident(g9,g1)
    c: Vertical(g9)
    c: DistanceY(g-7,g1) = 0.05
    c: PointOnObject(g10,g2)
    c: PointOnObject(g10,g-3)
    c: PointOnObject(g11,g0)
    c: PointOnObject(g11,g-4)
    c: Perpendicular(g11,g-4)
    c: Perpendicular(g10,g-3)
    c: Distance(g10) = 0.05
    c: Distance(g11,g0) = 0.17
    c: Distance(g10,g2) = 0.1
    c: DistanceY(g3,g0) = 0.44
FEATURE [PartDesign::Pad] Pad006
  Direction = (9.2e-15,0,-1)
  Length = 0.3
  Length2 = 10
  Profile = -> Sketch022
  ReferenceAxis = -> Sketch022 [N_Axis]
  Refine = true
  Suppressed = false
  Type = 0
FEATURE [Sketcher::SketchObject] Sketch023
  ArcFitTolerance = 1e-06
  AttachmentSupport = -> [Pad006]
  ExternalGeometry = -> [Pad006]
  FullyConstrained = false
  MakeInternals = false
  MapMode = 5
  Placement = pos=(1.098e-13,0,-12) rot=(1,0,0;3.14159rad)
  sketch-geometry (18):
    g0: ArcOfCircle CenterX=11.7636 CenterY=13.5088 CenterZ=0 NormalX=0 NormalY=0 NormalZ=-1 AngleXU=1.09289 Radius=0.00654463 StartAngle=1.5708 EndAngle=4.71239
    g1: LineSegment StartX=11.376 StartY=14.243 StartZ=0 EndX=11.7578 EndY=13.5058 EndZ=0
    g2: LineSegment StartX=11 StartY=14.9689 StartZ=0 EndX=11.376 EndY=14.243 EndZ=0
    g3: LineSegment StartX=10.2422 StartY=13.5058 StartZ=0 EndX=11 EndY=14.9689 EndZ=0
    g4: ArcOfCircle CenterX=10.2364 CenterY=13.5088 CenterZ=0 NormalX=0 NormalY=0 NormalZ=-1 AngleXU=2.0487 Radius=0.00654463 StartAngle=1.5708 EndAngle=4.71239
    g5: LineSegment StartX=10.2306 StartY=13.5118 StartZ=0 EndX=10.9942 EndY=14.9861 EndZ=0
    g6: ArcOfCircle CenterX=11 CenterY=14.9831 CenterZ=0 NormalX=0 NormalY=0 NormalZ=-1 AngleXU=-1.09289 Radius=0.00654463 StartAngle=1.5708 EndAngle=3.75658
    g7: LineSegment StartX=11.0058 StartY=14.9861 StartZ=0 EndX=11.3876 EndY=14.249 EndZ=0
    g8: LineSegment StartX=11.3876 StartY=14.249 StartZ=0 EndX=11.7694 EndY=13.5118 EndZ=0
    g9: ArcOfCircle CenterX=12.2636 CenterY=13.5088 CenterZ=0 NormalX=0 NormalY=0 NormalZ=-1 AngleXU=1.09289 Radius=0.00654463 StartAngle=1.5708 EndAngle=4.71239
    g10: LineSegment StartX=11.626 StartY=14.7256 StartZ=0 EndX=12.2578 EndY=13.5058 EndZ=0
    g11: LineSegment StartX=11 StartY=15.9343 StartZ=0 EndX=11.626 EndY=14.7256 EndZ=0
    g12: LineSegment StartX=9.7422 StartY=13.5058 StartZ=0 EndX=11 EndY=15.9343 EndZ=0
    g13: ArcOfCircle CenterX=9.73639 CenterY=13.5088 CenterZ=0 NormalX=0 NormalY=0 NormalZ=-1 AngleXU=2.0487 Radius=0.00654463 StartAngle=1.5708 EndAngle=4.71239
    g14: LineSegment StartX=9.73058 StartY=13.5118 StartZ=0 EndX=10.9942 EndY=15.9515 EndZ=0
    g15: ArcOfCircle CenterX=11 CenterY=15.9485 CenterZ=0 NormalX=0 NormalY=0 NormalZ=-1 AngleXU=-1.09289 Radius=0.00654463 StartAngle=1.5708 EndAngle=3.75658
    g16: LineSegment StartX=11.0058 StartY=15.9515 StartZ=0 EndX=11.6376 EndY=14.7317 EndZ=0
    g17: LineSegment StartX=11.6376 StartY=14.7317 StartZ=0 EndX=12.2694 EndY=13.5118 EndZ=0
  constraints (18):
    c: Tangent(g0,g1) = -1.5708
    c: Tangent(g0,g8) = 1.5708
    c: Coincident(g1,g2)
    c: Coincident(g2,g3)
    c: Tangent(g3,g4) = -1.5708
    c: Tangent(g4,g5) = 1.5708
    c: Tangent(g5,g6) = 1.5708
    c: Tangent(g6,g7) = 1.5708
    c: Coincident(g7,g8)
    c: Tangent(g9,g10) = -1.5708
    c: Tangent(g9,g17) = 1.5708
    c: Coincident(g10,g11)
    c: Coincident(g11,g12)
    c: Tangent(g12,g13) = -1.5708
    c: Tangent(g13,g14) = 1.5708
    c: Tangent(g14,g15) = 1.5708
    c: Tangent(g15,g16) = 1.5708
    c: Coincident(g16,g17)
FEATURE [PartDesign::Pocket] Pocket016
  BaseFeature = -> Pad006
  Direction = (-9.2e-15,0,1)
  Length = 0.15
  Length2 = 5
  Profile = -> Sketch023
  ReferenceAxis = -> Sketch023 [N_Axis]
  Refine = true
  Suppressed = false
  Type = 0
FEATURE [PartDesign::Body] Body010  label="Mixmaster_Sticker8"
  AllowCompound = false
  Group = -> [Binder006,Sketch022,Pad006,Sketch023,Pocket016]
  Origin = -> Origin011
  Tip = -> Pocket016
FEATURE [PartDesign::SubShapeBinder] Binder007
  BindCopyOnChange = 0
  BindMode = 0
  ClaimChildren = false
  Context = -> Body011 [Binder007.]
  Fuse = false
  MakeFace = true
  OffsetFill = false
  OffsetIntersection = false
  OffsetJoinType = 0
  OffsetOpenResult = false
  PartialLoad = false
  Refine = true
  Relative = true
  Support = -> [Body007[Pocket012.Face211]]
  _Version = 2
FEATURE [Sketcher::SketchObject] Sketch024
  ArcFitTolerance = 1e-06
  AttachmentSupport = -> [Binder007]
  ExternalGeometry = -> [Binder007]
  FullyConstrained = false
  MakeInternals = false
  MapMode = 5
  Placement = pos=(1.083e-13,0,-11.7) rot=(1,0,0;3.14159rad)
  sketch-geometry (14):
    g0: LineSegment StartX=12.5 StartY=-3.8726 StartZ=0 EndX=17.3 EndY=-3.8726 EndZ=0
    g1: LineSegment StartX=17.9726 StartY=-3.2 StartZ=0 EndX=17.9726 EndY=1 EndZ=0
    g2: LineSegment StartX=17.3 StartY=1.6726 StartZ=0 EndX=13.0931 EndY=1.6726 EndZ=0
    g3: LineSegment StartX=13.0931 StartY=1.6726 StartZ=0 EndX=11.8274 EndY=0.146316 EndZ=0
    g4: LineSegment StartX=11.8274 StartY=0.146316 StartZ=0 EndX=11.8274 EndY=-3.2 EndZ=0
    g5: ArcOfCircle CenterX=12.5 CenterY=-3.2 CenterZ=0 NormalX=0 NormalY=0 NormalZ=1 AngleXU=0 Radius=0.672602 StartAngle=3.14159 EndAngle=4.71239
    g6: ArcOfCircle CenterX=17.3 CenterY=-3.2 CenterZ=0 NormalX=0 NormalY=0 NormalZ=1 AngleXU=0 Radius=0.672602 StartAngle=4.71239 EndAngle=6.28319
    g7: ArcOfCircle CenterX=17.3 CenterY=1 CenterZ=0 NormalX=0 NormalY=0 NormalZ=1 AngleXU=0 Radius=0.672602 StartAngle=0 EndAngle=1.5708
    g8: LineSegment [constr] StartX=12.5 StartY=-3.8726 StartZ=0 EndX=12.5 EndY=-3.95 EndZ=0
    g9: LineSegment [constr] StartX=11.8274 StartY=-3.2 StartZ=0 EndX=11.75 EndY=-3.2 EndZ=0
    g10: LineSegment [constr] StartX=17.3 StartY=-3.8726 StartZ=0 EndX=17.3 EndY=-3.95 EndZ=0
    g11: LineSegment [constr] StartX=18.05 StartY=-3.2 StartZ=0 EndX=17.9726 EndY=-3.2 EndZ=0
    g12: LineSegment [constr] StartX=17.9726 StartY=1 StartZ=0 EndX=18.05 EndY=1 EndZ=0
    g13: LineSegment [constr] StartX=17.3 StartY=1.6726 StartZ=0 EndX=17.3 EndY=1.75 EndZ=0
  constraints (33):
    c: Horizontal(g0)
    c: Vertical(g1)
    c: Horizontal(g2)
    c: Coincident(g3,g2)
    c: Coincident(g4,g3)
    c: Vertical(g4)
    c: Coincident(g5,g4)
    c: Coincident(g5,g0)
    c: Coincident(g6,g0)
    c: Coincident(g6,g1)
    c: Coincident(g7,g2)
    c: Coincident(g7,g1)
    c: Coincident(g7,g-6)
    c: Coincident(g-4,g6)
    c: Coincident(g5,g-10)
    c: Coincident(g8,g0)
    c: Coincident(g8,g-10)
    c: Coincident(g9,g4)
    c: Coincident(g9,g-10)
    c: Coincident(g10,g0)
    c: Coincident(g10,g-5)
    c: Coincident(g11,g-4)
    c: Coincident(g11,g1)
    c: Coincident(g12,g1)
    c: Coincident(g12,g-6)
    c: Coincident(g13,g2)
    c: Coincident(g13,g-7)
    c: Vertical(g13)
    c: Horizontal(g12)
    c: Horizontal(g11)
    c: Vertical(g10)
    c: Vertical(g8)
    c: Horizontal(g9)
FEATURE [PartDesign::Pad] Pad007
  Direction = (9.3e-15,0,-1)
  Length = 0.3
  Length2 = 10
  Profile = -> Sketch024
  ReferenceAxis = -> Sketch024 [N_Axis]
  Refine = true
  Suppressed = false
  Type = 0
FEATURE [Sketcher::SketchObject] Sketch025
  ArcFitTolerance = 1e-06
  AttachmentOffset = pos=(0.5,0.5,0) rot=(0,0,1;0rad)
  AttachmentSupport = -> [Pad007]
  FullyConstrained = false
  MakeInternals = false
  MapMode = 5
  Placement = pos=(0.5,-0.5,-12) rot=(1,0,0;3.14159rad)
  sketch-geometry (40):
    g0: LineSegment StartX=12.6192 StartY=0.362747 StartZ=0 EndX=12.6192 EndY=-0.05384 EndZ=0
    g1: LineSegment StartX=12.6192 StartY=-0.05384 StartZ=0 EndX=13.8127 EndY=-0.05384 EndZ=0
    g2: LineSegment StartX=13.8127 StartY=-0.05384 StartZ=0 EndX=13.8127 EndY=0.362747 EndZ=0
    g3: LineSegment StartX=13.8127 StartY=0.362747 StartZ=0 EndX=12.6192 EndY=0.362747 EndZ=0
    g4: LineSegment StartX=14.064 StartY=0.360499 StartZ=0 EndX=14.064 EndY=-0.053873 EndZ=0
    g5: LineSegment StartX=14.064 StartY=-0.053873 StartZ=0 EndX=14.4156 EndY=-0.053873 EndZ=0
    g6: LineSegment StartX=14.4156 StartY=-0.053873 StartZ=0 EndX=14.4156 EndY=0.360499 EndZ=0
    g7: LineSegment StartX=14.4156 StartY=0.360499 StartZ=0 EndX=14.064 EndY=0.360499 EndZ=0
    g8: LineSegment StartX=14.6241 StartY=0.365185 StartZ=0 EndX=14.6241 EndY=-0.053618 EndZ=0
    g9: LineSegment StartX=14.6241 StartY=-0.053618 StartZ=0 EndX=14.9669 EndY=-0.053618 EndZ=0
    g10: LineSegment StartX=14.9669 StartY=-0.053618 StartZ=0 EndX=14.9669 EndY=0.365185 EndZ=0
    g11: LineSegment StartX=14.9669 StartY=0.365185 StartZ=0 EndX=14.6241 EndY=0.365185 EndZ=0
    g12: LineSegment StartX=15.176 StartY=0.350936 StartZ=0 EndX=15.176 EndY=-0.036534 EndZ=0
    g13: LineSegment StartX=15.176 StartY=-0.036534 StartZ=0 EndX=15.8144 EndY=-0.036534 EndZ=0
    g14: LineSegment StartX=15.8144 StartY=-0.036534 StartZ=0 EndX=15.5057 EndY=0.350936 EndZ=0
    g15: LineSegment StartX=15.5057 StartY=0.350936 StartZ=0 EndX=15.176 EndY=0.350936 EndZ=0
    g16: LineSegment StartX=15.7467 StartY=0.552788 StartZ=0 EndX=12.3521 EndY=0.552788 EndZ=0
    g17: LineSegment StartX=12.3521 StartY=0.552788 StartZ=0 EndX=12.3521 EndY=-0.2949 EndZ=0
    g18: LineSegment StartX=12.3521 StartY=-0.2949 StartZ=0 EndX=16.4223 EndY=-0.2949 EndZ=0
    g19: LineSegment StartX=16.4223 StartY=-0.2949 StartZ=0 EndX=15.7467 EndY=0.552788 EndZ=0
    g20: LineSegment StartX=14.6316 StartY=0.359369 StartZ=0 EndX=14.6316 EndY=-0.04604 EndZ=0
    g21: LineSegment StartX=14.6316 StartY=-0.04604 StartZ=0 EndX=14.9602 EndY=-0.04604 EndZ=0
    g22: LineSegment StartX=14.9602 StartY=-0.04604 StartZ=0 EndX=14.9602 EndY=0.358741 EndZ=0
    g23: LineSegment StartX=14.9602 StartY=0.358741 StartZ=0 EndX=14.6316 EndY=0.359369 EndZ=0
    g24: LineSegment StartX=15.1679 StartY=-0.041608 StartZ=0 EndX=15.8312 EndY=-0.041608 EndZ=0
    g25: LineSegment StartX=15.8312 StartY=-0.041608 StartZ=0 EndX=15.5135 EndY=0.357153 EndZ=0
    g26: LineSegment StartX=15.5135 StartY=0.357153 StartZ=0 EndX=15.1679 EndY=0.357153 EndZ=0
    g27: LineSegment StartX=15.1679 StartY=0.357153 StartZ=0 EndX=15.1679 EndY=-0.041608 EndZ=0
    g28: LineSegment StartX=12.6259 StartY=0.354045 StartZ=0 EndX=12.6259 EndY=-0.04692 EndZ=0
    g29: LineSegment StartX=12.6259 StartY=-0.04692 StartZ=0 EndX=13.803 EndY=-0.04692 EndZ=0
    g30: LineSegment StartX=13.803 StartY=-0.04692 StartZ=0 EndX=13.803 EndY=0.354045 EndZ=0
    g31: LineSegment StartX=13.803 StartY=0.354045 StartZ=0 EndX=12.6259 EndY=0.354045 EndZ=0
    g32: LineSegment StartX=14.0706 StartY=-0.043819 StartZ=0 EndX=14.406 EndY=-0.044948 EndZ=0
    g33: LineSegment StartX=14.406 StartY=-0.044948 StartZ=0 EndX=14.406 EndY=0.35603 EndZ=0
    g34: LineSegment StartX=14.406 StartY=0.35603 StartZ=0 EndX=14.0706 EndY=0.357159 EndZ=0
    g35: LineSegment StartX=14.0706 StartY=0.357159 StartZ=0 EndX=14.0706 EndY=-0.043819 EndZ=0
    g36: LineSegment StartX=16.4066 StartY=-0.286113 StartZ=0 EndX=15.7424 EndY=0.547403 EndZ=0
    g37: LineSegment StartX=15.7424 StartY=0.547403 StartZ=0 EndX=12.3669 EndY=0.547403 EndZ=0
    g38: LineSegment StartX=12.3669 StartY=0.547403 StartZ=0 EndX=12.3669 EndY=-0.286113 EndZ=0
    g39: LineSegment StartX=12.3669 StartY=-0.286113 StartZ=0 EndX=16.4066 EndY=-0.286113 EndZ=0
  constraints (67):
    c: Coincident(g0,g1)
    c: Coincident(g1,g2)
    c: Coincident(g2,g3)
    c: Coincident(g3,g0)
    c: Vertical(g0)
    c: Vertical(g2)
    c: Horizontal(g1)
    c: Horizontal(g3)
    c: Coincident(g4,g5)
    c: Coincident(g5,g6)
    c: Coincident(g6,g7)
    c: Coincident(g7,g4)
    c: Vertical(g4)
    c: Vertical(g6)
    c: Horizontal(g5)
    c: Horizontal(g7)
    c: Coincident(g8,g9)
    c: Coincident(g9,g10)
    c: Coincident(g10,g11)
    c: Coincident(g11,g8)
    c: Vertical(g8)
    c: Vertical(g10)
    c: Horizontal(g9)
    c: Horizontal(g11)
    c: Vertical(g12)
    c: Coincident(g13,g12)
    c: Horizontal(g13)
    c: Coincident(g14,g13)
    c: Coincident(g15,g14)
    c: Coincident(g15,g12)
    c: Horizontal(g15)
    c: Horizontal(g16)
    c: Coincident(g17,g16)
    c: Vertical(g17)
    c: Coincident(g18,g17)
    c: Horizontal(g18)
    c: Coincident(g19,g18)
    c: Coincident(g19,g16)
    c: Coincident(g20,g21)
    c: Coincident(g20,g23)
    c: Coincident(g21,g22)
    c: Coincident(g22,g23)
    c: Coincident(g24,g25)
    c: Coincident(g24,g27)
    c: Coincident(g25,g26)
    c: Coincident(g26,g27)
    c: Coincident(g28,g29)
    c: Coincident(g28,g31)
    c: Coincident(g29,g30)
    c: Coincident(g30,g31)
    c: Coincident(g32,g33)
    c: Coincident(g32,g35)
    c: Coincident(g33,g34)
    c: Coincident(g34,g35)
    c: Coincident(g36,g37)
    c: Coincident(g36,g39)
    c: Coincident(g37,g38)
    c: Coincident(g38,g39)
    c: Horizontal(g39)
    c: Horizontal(g37)
    c: Vertical(g38)
    c: Horizontal(g31)
    c: Horizontal(g29)
    c: Parallel(g14,g25)
    c: Parallel(g25,g36)
    c: Parallel(g36,g19)
    c: Horizontal(g21)
FEATURE [PartDesign::Pocket] Pocket017
  BaseFeature = -> Pad007
  Direction = (-9.3e-15,0,1)
  Length = 0.15
  Length2 = 5
  Profile = -> Sketch025
  ReferenceAxis = -> Sketch025 [N_Axis]
  Refine = true
  Suppressed = false
  Type = 0
FEATURE [Sketcher::SketchObject] Sketch026
  ArcFitTolerance = 1e-06
  AttachmentSupport = -> [Pocket017]
  FullyConstrained = false
  MakeInternals = false
  MapMode = 5
  Placement = pos=(1.111e-13,0,-12) rot=(1,0,0;3.14159rad)
  sketch-geometry (53):
    g0: ArcOfCircle CenterX=17.155 CenterY=-2.66563 CenterZ=0 NormalX=0 NormalY=0 NormalZ=-1 AngleXU=-1.37015 Radius=0.0476057 StartAngle=4.50024 EndAngle=4.67963
    g1: ArcOfCircle CenterX=16.5805 CenterY=-2.56827 CenterZ=0 NormalX=0 NormalY=0 NormalZ=1 AngleXU=0 Radius=0.630237 StartAngle=5.24949 EndAngle=6.11529
    g2: ArcOfCircle CenterX=16.5874 CenterY=-2.5797 CenterZ=0 NormalX=0 NormalY=0 NormalZ=1 AngleXU=0 Radius=0.616931 StartAngle=4.82845 EndAngle=5.24949
    g3: ArcOfCircle CenterX=16.6503 CenterY=-3.11954 CenterZ=0 NormalX=0 NormalY=0 NormalZ=-1 AngleXU=3.03912 Radius=0.0734384 StartAngle=1.5572 EndAngle=1.65545
    g4: LineSegment StartX=16.6516 StartY=-3.19296 StartZ=0 EndX=13.0046 EndY=-3.19296 EndZ=0
    g5: ArcOfCircle CenterX=13.0344 CenterY=-2.20182 CenterZ=0 NormalX=0 NormalY=0 NormalZ=1 AngleXU=0 Radius=0.991587 StartAngle=3.20327 EndAngle=4.68236
    g6: LineSegment StartX=12.0447 StartY=-1.43449 StartZ=0 EndX=12.0447 EndY=-2.26294 EndZ=0
    g7: ArcOfCircle CenterX=12.148 CenterY=-1.43449 CenterZ=0 NormalX=0 NormalY=0 NormalZ=-1 AngleXU=-1.5708 Radius=0.103323 StartAngle=1.5708 EndAngle=1.63337
    g8: ArcOfCircle CenterX=13.2865 CenterY=-1.50583 CenterZ=0 NormalX=0 NormalY=0 NormalZ=1 AngleXU=0 Radius=1.24404 StartAngle=1.62198 EndAngle=3.07902
    g9: ArcOfCircle CenterX=13.2293 CenterY=-0.389682 CenterZ=0 NormalX=0 NormalY=0 NormalZ=-1 AngleXU=-0.0575757 Radius=0.126435 StartAngle=1.57719 EndAngle=1.62837
    g10: LineSegment StartX=13.2293 StartY=-0.263247 StartZ=0 EndX=16.7672 EndY=-0.263247 EndZ=0
    g11: ArcOfCircle CenterX=16.7672 CenterY=-0.354282 CenterZ=0 NormalX=0 NormalY=0 NormalZ=-1 AngleXU=0 Radius=0.091035 StartAngle=1.5708 EndAngle=1.77768
    g12: ArcOfCircle CenterX=16.667 CenterY=-0.831287 CenterZ=0 NormalX=0 NormalY=0 NormalZ=1 AngleXU=0 Radius=0.578433 StartAngle=6.27958 EndAngle=7.6471
    g13: ArcOfCircle CenterX=17.181 CenterY=-0.833139 CenterZ=0 NormalX=0 NormalY=0 NormalZ=-1 AngleXU=1.52038 Radius=0.0645155 StartAngle=1.62482 EndAngle=1.64462
    g14: LineSegment StartX=17.2455 StartY=-0.834649 StartZ=0 EndX=17.2026 EndY=-2.66508 EndZ=0
    g15: ArcOfCircle CenterX=16.6559 CenterY=-0.828014 CenterZ=0 NormalX=0 NormalY=0 NormalZ=1 AngleXU=0 Radius=0.557378 StartAngle=0.0104819 EndAngle=1.38591
    g16: LineSegment StartX=17.2133 StartY=-0.822172 StartZ=0 EndX=17.1869 EndY=-2.6755 EndZ=0
    g17: ArcOfCircle CenterX=16.5945 CenterY=-2.5718 CenterZ=0 NormalX=0 NormalY=0 NormalZ=1 AngleXU=0 Radius=0.601362 StartAngle=5.24796 EndAngle=6.10987
    g18: ArcOfCircle CenterX=16.5944 CenterY=-2.57159 CenterZ=0 NormalX=0 NormalY=0 NormalZ=1 AngleXU=0 Radius=0.601604 StartAngle=4.83627 EndAngle=5.24796
    g19: LineSegment StartX=16.6687 StartY=-3.16859 StartZ=0 EndX=13.0073 EndY=-3.16859 EndZ=0
    g20: ArcOfCircle CenterX=13.0276 CenterY=-2.20345 CenterZ=0 NormalX=0 NormalY=0 NormalZ=1 AngleXU=0 Radius=0.965355 StartAngle=3.20039 EndAngle=4.69137
    g21: LineSegment StartX=12.0639 StartY=-1.42182 StartZ=0 EndX=12.0639 EndY=-2.26017 EndZ=0
    g22: ArcOfCircle CenterX=13.2766 CenterY=-1.49369 CenterZ=0 NormalX=0 NormalY=0 NormalZ=1 AngleXU=0 Radius=1.21487 StartAngle=1.61747 EndAngle=3.0824
    g23: LineSegment StartX=13.22 StartY=-0.280135 StartZ=0 EndX=16.7584 EndY=-0.280135 EndZ=0
    g24: ArcOfCircle CenterX=13.6099 CenterY=-1.84011 CenterZ=0 NormalX=0 NormalY=0 NormalZ=-1 AngleXU=0 Radius=0.00674837 StartAngle=1.5708 EndAngle=4.71239
    g25: LineSegment StartX=12.3893 StartY=-1.84686 StartZ=0 EndX=13.6099 EndY=-1.84686 EndZ=0
    g26: ArcOfCircle CenterX=13.3106 CenterY=-1.88137 CenterZ=0 NormalX=0 NormalY=0 NormalZ=1 AngleXU=0 Radius=0.921968 StartAngle=3.10415 EndAngle=4.61482
    g27: LineSegment StartX=14.9466 StartY=-2.79896 StartZ=0 EndX=13.2208 EndY=-2.79896 EndZ=0
    g28: LineSegment StartX=14.9466 StartY=-2.22184 StartZ=0 EndX=14.9466 EndY=-2.79896 EndZ=0
    g29: ArcOfCircle CenterX=14.9533 CenterY=-2.22184 CenterZ=0 NormalX=0 NormalY=0 NormalZ=-1 AngleXU=-1.5708 Radius=0.00674837 StartAngle=1.5708 EndAngle=4.71239
    g30: LineSegment StartX=14.96 StartY=-2.22184 StartZ=0 EndX=14.96 EndY=-2.8057 EndZ=0
    g31: ArcOfCircle CenterX=14.9533 CenterY=-2.8057 CenterZ=0 NormalX=0 NormalY=0 NormalZ=-1 AngleXU=1.5708 Radius=0.00674837 StartAngle=1.5708 EndAngle=3.14159
    g32: LineSegment StartX=14.9533 StartY=-2.81245 StartZ=0 EndX=13.2204 EndY=-2.81245 EndZ=0
    g33: ArcOfCircle CenterX=13.2204 CenterY=-2.8057 CenterZ=0 NormalX=0 NormalY=0 NormalZ=-1 AngleXU=-3.14159 Radius=0.00674837 StartAngle=1.5708 EndAngle=1.66801
    g34: ArcOfCircle CenterX=13.3106 CenterY=-1.88137 CenterZ=0 NormalX=0 NormalY=0 NormalZ=1 AngleXU=0 Radius=0.935464 StartAngle=3.09715 EndAngle=4.61518
    g35: ArcOfCircle CenterX=12.3828 CenterY=-1.84011 CenterZ=0 NormalX=0 NormalY=0 NormalZ=-1 AngleXU=-1.52635 Radius=0.00674837 StartAngle=1.5708 EndAngle=3.09715
    g36: LineSegment StartX=12.3828 StartY=-1.83336 StartZ=0 EndX=13.6099 EndY=-1.83336 EndZ=0
    g37: ArcOfCircle CenterX=14.9428 CenterY=-1.23077 CenterZ=0 NormalX=0 NormalY=0 NormalZ=-1 AngleXU=1.5708 Radius=0.00527407 StartAngle=1.5708 EndAngle=4.71239
    g38: LineSegment StartX=14.9375 StartY=-1.23077 StartZ=0 EndX=14.9375 EndY=-0.62167 EndZ=0
    g39: LineSegment StartX=14.9375 StartY=-0.62167 StartZ=0 EndX=13.2758 EndY=-0.62167 EndZ=0
    g40: ArcOfCircle CenterX=13.3658 CenterY=-1.6005 CenterZ=0 NormalX=0 NormalY=0 NormalZ=1 AngleXU=0 Radius=0.982959 StartAngle=1.66247 EndAngle=3.00961
    g41: LineSegment StartX=12.3914 StartY=-1.61904 StartZ=0 EndX=12.3914 EndY=-1.47115 EndZ=0
    g42: LineSegment StartX=13.6139 StartY=-1.61904 StartZ=0 EndX=12.3914 EndY=-1.61904 EndZ=0
    g43: ArcOfCircle CenterX=13.6139 CenterY=-1.62432 CenterZ=0 NormalX=0 NormalY=0 NormalZ=-1 AngleXU=0 Radius=0.00527407 StartAngle=1.5708 EndAngle=4.71239
    g44: LineSegment StartX=13.6139 StartY=-1.62959 StartZ=0 EndX=12.3861 EndY=-1.62959 EndZ=0
    g45: ArcOfCircle CenterX=12.3861 CenterY=-1.62432 CenterZ=0 NormalX=0 NormalY=0 NormalZ=-1 AngleXU=-3.14159 Radius=0.00527407 StartAngle=1.5708 EndAngle=3.14159
    g46: LineSegment StartX=12.3809 StartY=-1.62432 StartZ=0 EndX=12.3809 EndY=-1.4708 EndZ=0
    g47: ArcOfCircle CenterX=12.3861 CenterY=-1.4708 CenterZ=0 NormalX=0 NormalY=0 NormalZ=-1 AngleXU=-1.5708 Radius=0.00527407 StartAngle=1.5708 EndAngle=1.70242
    g48: ArcOfCircle CenterX=13.3658 CenterY=-1.6005 CenterZ=0 NormalX=0 NormalY=0 NormalZ=1 AngleXU=0 Radius=0.993507 StartAngle=1.66223 EndAngle=3.00997
    g49: ArcOfCircle CenterX=13.2756 CenterY=-0.616396 CenterZ=0 NormalX=0 NormalY=0 NormalZ=-1 AngleXU=-0.0914287 Radius=0.00527407 StartAngle=1.5708 EndAngle=1.66222
    g50: LineSegment StartX=14.9428 StartY=-0.611121 StartZ=0 EndX=13.2756 EndY=-0.611121 EndZ=0
    g51: ArcOfCircle CenterX=14.9428 CenterY=-0.616396 CenterZ=0 NormalX=0 NormalY=0 NormalZ=-1 AngleXU=0 Radius=0.00527407 StartAngle=1.5708 EndAngle=3.14159
    g52: LineSegment StartX=14.9481 StartY=-1.23077 StartZ=0 EndX=14.9481 EndY=-0.616396 EndZ=0
  constraints (61):
    c: Tangent(g0,g1) = -1.5708
    c: Coincident(g0,g14)
    c: Tangent(g1,g2) = -1.5708
    c: Tangent(g2,g3) = -1.5708
    c: Coincident(g3,g4)
    c: Tangent(g6,g7) = -1.5708
    c: Tangent(g7,g8) = -1.5708
    c: Tangent(g8,g9) = -1.5708
    c: Tangent(g9,g10) = 1.5708
    c: Tangent(g10,g11) = 1.5708
    c: Tangent(g11,g12) = -1.5708
    c: Tangent(g12,g13) = -1.5708
    c: Tangent(g13,g14) = 1.5708
    c: Coincident(g15,g16)
    c: Coincident(g15,g23)
    c: Coincident(g16,g17)
    c: Tangent(g17,g18) = -1.5708
    c: Coincident(g18,g19)
    c: Coincident(g19,g20)
    c: Coincident(g20,g21)
    c: Coincident(g21,g22)
    c: Coincident(g22,g23)
    c: Coincident(g5,g6)
    c: Coincident(g4,g5)
    c: Tangent(g24,g25) = -1.5708
    c: Tangent(g24,g36) = 1.5708
    c: Coincident(g25,g26)
    c: Coincident(g26,g27)
    c: Coincident(g27,g28)
    c: Tangent(g28,g29) = -1.5708
    c: Tangent(g29,g30) = 1.5708
    c: Tangent(g30,g31) = 1.5708
    c: Tangent(g31,g32) = 1.5708
    c: Tangent(g32,g33) = 1.5708
    c: Tangent(g33,g34) = -1.5708
    c: Tangent(g34,g35) = -1.5708
    c: Tangent(g35,g36) = 1.5708
    c: Tangent(g37,g38) = 1.5708
    c: Tangent(g37,g52) = -1.5708
    c: Coincident(g38,g39)
    c: Coincident(g39,g40)
    c: Coincident(g40,g41)
    c: Coincident(g41,g42)
    c: Tangent(g42,g43) = -1.5708
    c: Tangent(g43,g44) = 1.5708
    c: Tangent(g44,g45) = 1.5708
    c: Tangent(g45,g46) = 1.5708
    c: Tangent(g46,g47) = 1.5708
    c: Tangent(g47,g48) = -1.5708
    c: Tangent(g48,g49) = -1.5708
    c: Tangent(g49,g50) = -1.5708
    c: Tangent(g50,g51) = -1.5708
    c: Tangent(g51,g52) = -1.5708
    c: Vertical(g6)
    c: Vertical(g21)
    c: Horizontal(g19)
    c: Horizontal(g4)
    c: Horizontal(g32)
    c: Horizontal(g27)
    c: Horizontal(g23)
    c: Horizontal(g10)
FEATURE [PartDesign::Pocket] Pocket018
  BaseFeature = -> Pocket017
  Direction = (-9.3e-15,0,1)
  Length = 0.15
  Length2 = 5
  Profile = -> Sketch026
  ReferenceAxis = -> Sketch026 [N_Axis]
  Refine = true
  Suppressed = false
  Type = 0
FEATURE [Sketcher::SketchObject] Sketch027
  ArcFitTolerance = 1e-06
  AttachmentSupport = -> [Pocket018]
  FullyConstrained = false
  MakeInternals = false
  MapMode = 5
  Placement = pos=(1.111e-13,0,-12) rot=(1,0,0;3.14159rad)
  sketch-geometry (16):
    g0: ArcOfCircle CenterX=14.953 CenterY=-2.21267 CenterZ=0 NormalX=0 NormalY=0 NormalZ=-1 AngleXU=0 Radius=0.00429963 StartAngle=1.5708 EndAngle=4.71239
    g1: LineSegment StartX=14.8152 StartY=-2.21697 StartZ=0 EndX=14.953 EndY=-2.21697 EndZ=0
    g2: LineSegment StartX=14.6774 StartY=-2.21697 StartZ=0 EndX=14.8152 EndY=-2.21697 EndZ=0
    g3: ArcOfCircle CenterX=14.6568 CenterY=-0.55167 CenterZ=0 NormalX=0 NormalY=0 NormalZ=1 AngleXU=0 Radius=1.66543 StartAngle=4.0287 EndAngle=4.72478
    g4: ArcOfCircle CenterX=13.6075 CenterY=-1.83945 CenterZ=0 NormalX=0 NormalY=0 NormalZ=-1 AngleXU=-2.4579 Radius=0.00429979 StartAngle=1.5708 EndAngle=4.71239
    g5: ArcOfCircle CenterX=14.6568 CenterY=-0.55167 CenterZ=0 NormalX=0 NormalY=0 NormalZ=1 AngleXU=0 Radius=1.65683 StartAngle=4.0287 EndAngle=4.72479
    g6: LineSegment StartX=14.6773 StartY=-2.20837 StartZ=0 EndX=14.8152 EndY=-2.20837 EndZ=0
    g7: LineSegment StartX=14.8152 StartY=-2.20837 StartZ=0 EndX=14.953 EndY=-2.20837 EndZ=0
    g8: ArcOfCircle CenterX=14.9405 CenterY=-1.23634 CenterZ=0 NormalX=0 NormalY=0 NormalZ=-1 AngleXU=0 Radius=0.00430042 StartAngle=1.5708 EndAngle=4.71239
    g9: LineSegment StartX=14.6339 StartY=-1.24064 StartZ=0 EndX=14.9405 EndY=-1.24064 EndZ=0
    g10: ArcOfCircle CenterX=14.5945 CenterY=-2.6955 CenterZ=0 NormalX=0 NormalY=0 NormalZ=1 AngleXU=0 Radius=1.45539 StartAngle=1.54368 EndAngle=1.92951
    g11: ArcOfCircle CenterX=14.5945 CenterY=-2.6955 CenterZ=0 NormalX=0 NormalY=0 NormalZ=1 AngleXU=0 Radius=1.45539 StartAngle=1.92951 EndAngle=2.31525
    g12: ArcOfCircle CenterX=13.6054 CenterY=-1.62196 CenterZ=0 NormalX=0 NormalY=0 NormalZ=-1 AngleXU=2.39714 Radius=0.00429963 StartAngle=1.5708 EndAngle=4.71239
    g13: ArcOfCircle CenterX=14.5945 CenterY=-2.6955 CenterZ=0 NormalX=0 NormalY=0 NormalZ=1 AngleXU=0 Radius=1.46399 StartAngle=1.92951 EndAngle=2.31525
    g14: ArcOfCircle CenterX=14.5945 CenterY=-2.6955 CenterZ=0 NormalX=0 NormalY=0 NormalZ=1 AngleXU=0 Radius=1.46399 StartAngle=1.5438 EndAngle=1.92951
    g15: LineSegment StartX=14.634 StartY=-1.23204 StartZ=0 EndX=14.9405 EndY=-1.23204 EndZ=0
  constraints (16):
    c: Tangent(g0,g1) = -1.5708
    c: Tangent(g0,g7) = 1.5708
    c: Coincident(g1,g2)
    c: Coincident(g2,g3)
    c: Tangent(g3,g4) = -1.5708
    c: Tangent(g4,g5) = 1.5708
    c: Coincident(g6,g7)
    c: Tangent(g8,g9) = -1.5708
    c: Tangent(g8,g15) = 1.5708
    c: Tangent(g10,g11) = -1.5708
    c: Tangent(g11,g12) = 1.5708
    c: Tangent(g12,g13) = -1.5708
    c: Tangent(g13,g14) = -1.5708
    c: Coincident(g14,g15)
    c: Coincident(g6,g5)
    c: Coincident(g9,g10)
FEATURE [PartDesign::Pocket] Pocket019
  BaseFeature = -> Pocket018
  Direction = (-9.3e-15,0,1)
  Length = 0.15
  Length2 = 5
  Profile = -> Sketch027
  ReferenceAxis = -> Sketch027 [N_Axis]
  Refine = true
  Suppressed = false
  Type = 0
FEATURE [Sketcher::SketchObject] Sketch028
  ArcFitTolerance = 1e-06
  AttachmentSupport = -> [Pocket019]
  FullyConstrained = false
  MakeInternals = false
  MapMode = 5
  Placement = pos=(1.111e-13,0,-12) rot=(1,0,0;3.14159rad)
  sketch-geometry (16):
    g0: ArcOfCircle CenterX=13.8432 CenterY=-1.73243 CenterZ=0 NormalX=0 NormalY=0 NormalZ=1 AngleXU=0 Radius=0.0765003 StartAngle=2.4079 EndAngle=3.79146
    g1: ArcOfCircle CenterX=14.5819 CenterY=-2.98678 CenterZ=0 NormalX=0 NormalY=0 NormalZ=1 AngleXU=0 Radius=1.52883 StartAngle=1.516 EndAngle=2.11803
    g2: ArcOfCircle CenterX=14.5538 CenterY=-0.542503 CenterZ=0 NormalX=0 NormalY=0 NormalZ=1 AngleXU=0 Radius=1.45722 StartAngle=4.15444 EndAngle=4.78457
    g3: ArcOfCircle CenterX=16.0106 CenterY=-1.72944 CenterZ=0 NormalX=0 NormalY=0 NormalZ=1 AngleXU=0 Radius=0.0734189 StartAngle=5.2949 EndAngle=7.0739
    g4: ArcOfCircle CenterX=15.2911 CenterY=-2.91114 CenterZ=0 NormalX=0 NormalY=0 NormalZ=1 AngleXU=0 Radius=1.45505 StartAngle=1.01221 EndAngle=1.6463
    g5: ArcOfCircle CenterX=15.2302 CenterY=-0.256644 CenterZ=0 NormalX=0 NormalY=0 NormalZ=1 AngleXU=0 Radius=1.73989 StartAngle=4.68589 EndAngle=5.20367
    g6: LineSegment StartX=15.1813 StartY=-1.46024 StartZ=0 EndX=14.6656 EndY=-1.46024 EndZ=0
    g7: LineSegment StartX=15.1841 StartY=-1.99592 StartZ=0 EndX=14.6589 EndY=-1.99592 EndZ=0
    g8: ArcOfCircle CenterX=16.0106 CenterY=-1.72944 CenterZ=0 NormalX=0 NormalY=0 NormalZ=1 AngleXU=0 Radius=0.0794952 StartAngle=5.29495 EndAngle=7.0764
    g9: LineSegment StartX=15.1822 StartY=-1.45339 StartZ=0 EndX=14.6663 EndY=-1.45339 EndZ=0
    g10: ArcOfCircle CenterX=13.8432 CenterY=-1.73243 CenterZ=0 NormalX=0 NormalY=0 NormalZ=1 AngleXU=0 Radius=0.0804306 StartAngle=2.40576 EndAngle=3.79504
    g11: LineSegment StartX=15.1871 StartY=-2.00427 StartZ=0 EndX=14.6613 EndY=-2.00427 EndZ=0
    g12: ArcOfCircle CenterX=14.5836 CenterY=-2.97279 CenterZ=0 NormalX=0 NormalY=0 NormalZ=1 AngleXU=0 Radius=1.52164 StartAngle=1.51643 EndAngle=2.12443
    g13: ArcOfCircle CenterX=14.5863 CenterY=-0.444849 CenterZ=0 NormalX=0 NormalY=0 NormalZ=1 AngleXU=0 Radius=1.56122 StartAngle=4.16917 EndAngle=4.76044
    g14: ArcOfCircle CenterX=15.2714 CenterY=-2.98503 CenterZ=0 NormalX=0 NormalY=0 NormalZ=1 AngleXU=0 Radius=1.53423 StartAngle=1.02614 EndAngle=1.62895
    g15: ArcOfCircle CenterX=15.2129 CenterY=-0.203328 CenterZ=0 NormalX=0 NormalY=0 NormalZ=1 AngleXU=0 Radius=1.80112 StartAngle=4.69806 EndAngle=5.19847
  constraints (22):
    c: Coincident(g1,g0)
    c: Coincident(g2,g0)
    c: Coincident(g4,g3)
    c: Coincident(g5,g3)
    c: Coincident(g6,g4)
    c: Coincident(g6,g1)
    c: Horizontal(g6)
    c: Coincident(g7,g5)
    c: Coincident(g7,g2)
    c: Horizontal(g7)
    c: Horizontal(g11)
    c: Horizontal(g9)
    c: Coincident(g0,g10)
    c: Coincident(g8,g3)
    c: Coincident(g12,g10)
    c: Coincident(g12,g9)
    c: Coincident(g13,g11)
    c: Coincident(g13,g10)
    c: Coincident(g14,g8)
    c: Coincident(g14,g9)
    c: Coincident(g15,g11)
    c: Coincident(g15,g8)
FEATURE [PartDesign::Pocket] Pocket020
  BaseFeature = -> Pocket019
  Direction = (-9.3e-15,0,1)
  Length = 0.15
  Length2 = 5
  Profile = -> Sketch028
  ReferenceAxis = -> Sketch028 [N_Axis]
  Refine = true
  Suppressed = false
  Type = 0
FEATURE [Sketcher::SketchObject] Sketch029
  ArcFitTolerance = 1e-06
  AttachmentSupport = -> [Pocket020]
  FullyConstrained = false
  MakeInternals = false
  MapMode = 5
  Placement = pos=(1.111e-13,0,-12) rot=(1,0,0;3.14159rad)
  sketch-geometry (32):
    g0: ArcOfCircle CenterX=16.6453 CenterY=-2.30654 CenterZ=0 NormalX=0 NormalY=0 NormalZ=-1 AngleXU=-1.41867 Radius=0.0108031 StartAngle=4.54877 EndAngle=4.71239
    g1: ArcOfCircle CenterX=16.0527 CenterY=-2.2157 CenterZ=0 NormalX=0 NormalY=0 NormalZ=1 AngleXU=0 Radius=0.610279 StartAngle=5.31797 EndAngle=6.13106
    g2: ArcOfCircle CenterX=16.0527 CenterY=-2.2157 CenterZ=0 NormalX=0 NormalY=0 NormalZ=1 AngleXU=0 Radius=0.610279 StartAngle=4.91142 EndAngle=5.31797
    g3: ArcOfCircle CenterX=16.0527 CenterY=-2.2157 CenterZ=0 NormalX=0 NormalY=0 NormalZ=1 AngleXU=0 Radius=0.588673 StartAngle=4.91142 EndAngle=5.31797
    g4: ArcOfCircle CenterX=16.0527 CenterY=-2.2157 CenterZ=0 NormalX=0 NormalY=0 NormalZ=1 AngleXU=0 Radius=0.588673 StartAngle=5.31797 EndAngle=6.13128
    g5: ArcOfCircle CenterX=16.6453 CenterY=-2.30654 CenterZ=0 NormalX=0 NormalY=0 NormalZ=-1 AngleXU=1.5708 Radius=0.0108031 StartAngle=4.71239 EndAngle=4.87626
    g6: LineSegment StartX=16.6345 StartY=-2.30654 StartZ=0 EndX=16.6345 EndY=-0.953738 EndZ=0
    g7: ArcOfCircle CenterX=16.1748 CenterY=-1.08604 CenterZ=0 NormalX=0 NormalY=0 NormalZ=1 AngleXU=0 Radius=0.478365 StartAngle=0.280234 EndAngle=1.39052
    g8: LineSegment StartX=15.1791 StartY=-0.615431 StartZ=0 EndX=16.2605 EndY=-0.615431 EndZ=0
    g9: LineSegment StartX=15.1791 StartY=-1.22929 StartZ=0 EndX=15.1791 EndY=-0.615431 EndZ=0
    g10: ArcOfCircle CenterX=15.2183 CenterY=-3.02298 CenterZ=0 NormalX=0 NormalY=0 NormalZ=1 AngleXU=0 Radius=1.79412 StartAngle=0.931995 EndAngle=1.59267
    g11: ArcOfCircle CenterX=16.2816 CenterY=-1.59131 CenterZ=0 NormalX=0 NormalY=0 NormalZ=-1 AngleXU=0.638801 Radius=0.0108031 StartAngle=1.5708 EndAngle=1.79131
    g12: ArcOfCircle CenterX=16.1202 CenterY=-1.73046 CenterZ=0 NormalX=0 NormalY=0 NormalZ=1 AngleXU=0 Radius=0.223905 StartAngle=5.45105 EndAngle=6.99467
    g13: ArcOfCircle CenterX=16.2637 CenterY=-1.88802 CenterZ=0 NormalX=0 NormalY=0 NormalZ=-1 AngleXU=2.40293 Radius=0.0108031 StartAngle=1.5708 EndAngle=1.70159
    g14: ArcOfCircle CenterX=15.2143 CenterY=-0.379691 CenterZ=0 NormalX=0 NormalY=0 NormalZ=1 AngleXU=0 Radius=1.84828 StartAngle=4.694 EndAngle=5.32026
    g15: LineSegment StartX=15.1803 StartY=-2.22766 StartZ=0 EndX=15.1803 EndY=-2.79254 EndZ=0
    g16: LineSegment StartX=15.1803 StartY=-2.79254 StartZ=0 EndX=16.1691 EndY=-2.79275 EndZ=0
    g17: LineSegment StartX=15.1695 StartY=-2.81414 StartZ=0 EndX=16.1734 EndY=-2.81393 EndZ=0
    g18: ArcOfCircle CenterX=15.1695 CenterY=-2.80334 CenterZ=0 NormalX=0 NormalY=0 NormalZ=-1 AngleXU=-3.14159 Radius=0.0108008 StartAngle=1.57059 EndAngle=3.14159
    g19: LineSegment StartX=15.1587 StartY=-2.21662 StartZ=0 EndX=15.1587 EndY=-2.80334 EndZ=0
    g20: ArcOfCircle CenterX=15.1695 CenterY=-2.21662 CenterZ=0 NormalX=0 NormalY=0 NormalZ=-1 AngleXU=-1.5708 Radius=0.0108031 StartAngle=1.5708 EndAngle=3.16597
    g21: ArcOfCircle CenterX=15.2143 CenterY=-0.379691 CenterZ=0 NormalX=0 NormalY=0 NormalZ=1 AngleXU=0 Radius=1.82668 StartAngle=4.68801 EndAngle=5.31986
    g22: ArcOfCircle CenterX=16.1202 CenterY=-1.73046 CenterZ=0 NormalX=0 NormalY=0 NormalZ=1 AngleXU=0 Radius=0.202299 StartAngle=5.4545 EndAngle=6.98882
    g23: ArcOfCircle CenterX=15.2183 CenterY=-3.02298 CenterZ=0 NormalX=0 NormalY=0 NormalZ=1 AngleXU=0 Radius=1.77252 StartAngle=0.932678 EndAngle=1.59886
    g24: ArcOfCircle CenterX=15.1683 CenterY=-1.24036 CenterZ=0 NormalX=0 NormalY=0 NormalZ=-1 AngleXU=3.11352 Radius=0.0108031 StartAngle=1.5708 EndAngle=3.16966
    g25: LineSegment StartX=15.1575 StartY=-1.24036 StartZ=0 EndX=15.1575 EndY=-0.604628 EndZ=0
    g26: ArcOfCircle CenterX=15.1683 CenterY=-0.604628 CenterZ=0 NormalX=0 NormalY=0 NormalZ=-1 AngleXU=-1.5708 Radius=0.0108031 StartAngle=1.5708 EndAngle=3.14159
    g27: LineSegment StartX=15.1683 StartY=-0.593825 StartZ=0 EndX=16.2615 EndY=-0.593825 EndZ=0
    g28: ArcOfCircle CenterX=16.2615 CenterY=-0.604628 CenterZ=0 NormalX=0 NormalY=0 NormalZ=-1 AngleXU=0 Radius=0.0108031 StartAngle=1.5708 EndAngle=1.74907
    g29: ArcOfCircle CenterX=16.1748 CenterY=-1.08604 CenterZ=0 NormalX=0 NormalY=0 NormalZ=1 AngleXU=0 Radius=0.499971 StartAngle=0.277102 EndAngle=1.39253
    g30: ArcOfCircle CenterX=16.6453 CenterY=-0.952223 CenterZ=0 NormalX=0 NormalY=0 NormalZ=-1 AngleXU=1.29369 Radius=0.0108031 StartAngle=1.5708 EndAngle=1.8479
    g31: LineSegment StartX=16.6561 StartY=-2.30642 StartZ=0 EndX=16.6561 EndY=-0.952223 EndZ=0
  constraints (32):
    c: Tangent(g0,g1) = -1.5708
    c: Coincident(g0,g31)
    c: Tangent(g1,g2) = -1.5708
    c: Tangent(g3,g4) = -1.5708
    c: Coincident(g4,g5)
    c: Tangent(g5,g6) = 1.5708
    c: Coincident(g6,g7)
    c: Coincident(g7,g8)
    c: Coincident(g8,g9)
    c: Coincident(g9,g10)
    c: Tangent(g10,g11) = -1.5708
    c: Tangent(g11,g12) = -1.5708
    c: Tangent(g12,g13) = -1.5708
    c: Tangent(g13,g14) = -1.5708
    c: Coincident(g14,g15)
    c: Coincident(g15,g16)
    c: Tangent(g17,g18) = -1.5708
    c: Tangent(g18,g19) = -1.5708
    c: Tangent(g19,g20) = -1.5708
    c: Tangent(g20,g21) = 1.5708
    c: Coincident(g21,g22)
    c: Coincident(g22,g23)
    c: Tangent(g23,g24) = 1.5708
    c: Tangent(g24,g25) = 1.5708
    c: Tangent(g25,g26) = 1.5708
    c: Tangent(g26,g27) = 1.5708
    c: Tangent(g27,g28) = 1.5708
    c: Tangent(g28,g29) = -1.5708
    c: Tangent(g29,g30) = -1.5708
    c: Tangent(g30,g31) = -1.5708
    c: Coincident(g16,g3)
    c: Coincident(g2,g17)
FEATURE [PartDesign::Pocket] Pocket021
  BaseFeature = -> Pocket020
  Direction = (-9.3e-15,0,1)
  Length = 0.15
  Length2 = 5
  Profile = -> Sketch029
  ReferenceAxis = -> Sketch029 [N_Axis]
  Refine = true
  Suppressed = false
  Type = 0
FEATURE [PartDesign::Body] Body011  label="Mixmaster_Sticker9"
  AllowCompound = false
  Group = -> [Binder007,Sketch024,Pad007,Sketch025,Pocket017,Sketch026,Pocket018,Sketch027,Pocket019,Sketch028,Pocket020,Sketch029,Pocket021]
  Origin = -> Origin012
  Tip = -> Pocket021
